FCSTD DOCUMENT  (FreeCAD 0.18R4 (GitTag))
Label: clinica_nuevo_monterreyp1
License: All rights reserved
LicenseURL: http://en.wikipedia.org/wiki/All_rights_reserved
objects: Part::Part2DObjectPython×355, App::Part×206, App::FeaturePython×159, App::DocumentObjectGroup×10, Part::FeaturePython×4
note: 359 computed .brp shape members not serialized (recipe doc carries the construction recipe); baked Part::Feature solids carry a one-line shape summary decoded from their .brp

FEATURE [Part::Part2DObjectPython] Line164  # Draft 2D object (typed FeaturePython)
  ChamferSize = 0
  Closed = false
  End = (0,-100,0)
  FilletRadius = 0
  Length = 200
  MakeFace = true
  Placement = pos=(0,100,0) rot=(0,0,1;0rad)
  Points = (2) [(0,0,0),(0,-200,0)]
  Start = (0,100,0)
  Subdivisions = 0
FEATURE [Part::Part2DObjectPython] Line157  # Draft 2D object (typed FeaturePython)
  ChamferSize = 0
  Closed = false
  End = (-100,3.8e-15,0)
  FilletRadius = 0
  Length = 200
  MakeFace = true
  Placement = pos=(100,1.8e-14,0) rot=(0,0,1;0rad)
  Points = (2) [(0,0,0),(-200,-1.42109e-14,0)]
  Start = (100,1.8e-14,0)
  Subdivisions = 0
FEATURE [Part::Part2DObjectPython] Line156  # Draft 2D object (typed FeaturePython)
  ChamferSize = 0
  Closed = false
  End = (0,-100,0)
  FilletRadius = 0
  Length = 200
  MakeFace = true
  Placement = pos=(0,100,0) rot=(0,0,1;0rad)
  Points = (2) [(0,0,0),(0,-200,0)]
  Start = (0,100,0)
  Subdivisions = 0
FEATURE [Part::Part2DObjectPython] Line166  # Draft 2D object (typed FeaturePython)
  ChamferSize = 0
  Closed = false
  End = (0,-100,0)
  FilletRadius = 0
  Length = 200
  MakeFace = true
  Placement = pos=(0,100,0) rot=(0,0,1;0rad)
  Points = (2) [(0,0,0),(0,-200,0)]
  Start = (0,100,0)
  Subdivisions = 0
FEATURE [Part::Part2DObjectPython] Line161  # Draft 2D object (typed FeaturePython)
  ChamferSize = 0
  Closed = false
  End = (-100,3.8e-15,0)
  FilletRadius = 0
  Length = 200
  MakeFace = true
  Placement = pos=(100,1.8e-14,0) rot=(0,0,1;0rad)
  Points = (2) [(0,0,0),(-200,-1.42109e-14,0)]
  Start = (100,1.8e-14,0)
  Subdivisions = 0
FEATURE [Part::Part2DObjectPython] Circle083  # Draft 2D object (typed FeaturePython)
  FirstAngle = 0
  LastAngle = 0
  MakeFace = true
  Radius = 100
FEATURE [Part::Part2DObjectPython] Line173  # Draft 2D object (typed FeaturePython)
  ChamferSize = 0
  Closed = false
  End = (-100,3.8e-15,0)
  FilletRadius = 0
  Length = 200
  MakeFace = true
  Placement = pos=(100,1.8e-14,0) rot=(0,0,1;0rad)
  Points = (2) [(0,0,0),(-200,-1.42109e-14,0)]
  Start = (100,1.8e-14,0)
  Subdivisions = 0
FEATURE [Part::Part2DObjectPython] Line152  # Draft 2D object (typed FeaturePython)
  ChamferSize = 0
  Closed = false
  End = (0,-100,0)
  FilletRadius = 0
  Length = 200
  MakeFace = true
  Placement = pos=(0,100,0) rot=(0,0,1;0rad)
  Points = (2) [(0,0,0),(0,-200,0)]
  Start = (0,100,0)
  Subdivisions = 0
FEATURE [Part::Part2DObjectPython] Line165  # Draft 2D object (typed FeaturePython)
  ChamferSize = 0
  Closed = false
  End = (-100,3.8e-15,0)
  FilletRadius = 0
  Length = 200
  MakeFace = true
  Placement = pos=(100,1.8e-14,0) rot=(0,0,1;0rad)
  Points = (2) [(0,0,0),(-200,-1.42109e-14,0)]
  Start = (100,1.8e-14,0)
  Subdivisions = 0
FEATURE [Part::Part2DObjectPython] Line170  # Draft 2D object (typed FeaturePython)
  ChamferSize = 0
  Closed = false
  End = (0,-100,0)
  FilletRadius = 0
  Length = 200
  MakeFace = true
  Placement = pos=(0,100,0) rot=(0,0,1;0rad)
  Points = (2) [(0,0,0),(0,-200,0)]
  Start = (0,100,0)
  Subdivisions = 0
FEATURE [Part::Part2DObjectPython] Line158  # Draft 2D object (typed FeaturePython)
  ChamferSize = 0
  Closed = false
  End = (0,-100,0)
  FilletRadius = 0
  Length = 200
  MakeFace = true
  Placement = pos=(0,100,0) rot=(0,0,1;0rad)
  Points = (2) [(0,0,0),(0,-200,0)]
  Start = (0,100,0)
  Subdivisions = 0
FEATURE [Part::Part2DObjectPython] Line155  # Draft 2D object (typed FeaturePython)
  ChamferSize = 0
  Closed = false
  End = (-100,3.8e-15,0)
  FilletRadius = 0
  Length = 200
  MakeFace = true
  Placement = pos=(100,1.8e-14,0) rot=(0,0,1;0rad)
  Points = (2) [(0,0,0),(-200,-1.42109e-14,0)]
  Start = (100,1.8e-14,0)
  Subdivisions = 0
FEATURE [Part::Part2DObjectPython] Circle077  # Draft 2D object (typed FeaturePython)
  FirstAngle = 0
  LastAngle = 0
  MakeFace = true
  Radius = 100
FEATURE [Part::Part2DObjectPython] Line168  # Draft 2D object (typed FeaturePython)
  ChamferSize = 0
  Closed = false
  End = (0,-100,0)
  FilletRadius = 0
  Length = 200
  MakeFace = true
  Placement = pos=(0,100,0) rot=(0,0,1;0rad)
  Points = (2) [(0,0,0),(0,-200,0)]
  Start = (0,100,0)
  Subdivisions = 0
FEATURE [Part::Part2DObjectPython] Circle081  # Draft 2D object (typed FeaturePython)
  FirstAngle = 0
  LastAngle = 0
  MakeFace = true
  Radius = 100
FEATURE [Part::Part2DObjectPython] Line153  # Draft 2D object (typed FeaturePython)
  ChamferSize = 0
  Closed = false
  End = (-100,3.8e-15,0)
  FilletRadius = 0
  Length = 200
  MakeFace = true
  Placement = pos=(100,1.8e-14,0) rot=(0,0,1;0rad)
  Points = (2) [(0,0,0),(-200,-1.42109e-14,0)]
  Start = (100,1.8e-14,0)
  Subdivisions = 0
FEATURE [Part::Part2DObjectPython] Line135  # Draft 2D object (typed FeaturePython)
  ChamferSize = 0
  Closed = false
  End = (-100,3.8e-15,0)
  FilletRadius = 0
  Length = 200
  MakeFace = true
  Placement = pos=(100,1.8e-14,0) rot=(0,0,1;0rad)
  Points = (2) [(0,0,0),(-200,-1.42109e-14,0)]
  Start = (100,1.8e-14,0)
  Subdivisions = 0
FEATURE [Part::Part2DObjectPython] Circle063  # Draft 2D object (typed FeaturePython)
  FirstAngle = 0
  LastAngle = 0
  MakeFace = false
  Radius = 50
FEATURE [Part::Part2DObjectPython] Line074  # Draft 2D object (typed FeaturePython)
  ChamferSize = 0
  Closed = false
  End = (100,100,0)
  FilletRadius = 0
  Length = 91.7357
  MakeFace = false
  Placement = pos=(35.1355,35.1306,0) rot=(0,0,1;0rad)
  Points = (2) [(0,0,0),(64.8645,64.8694,0)]
  Start = (35.1355,35.1306,0)
  Subdivisions = 0
FEATURE [Part::Part2DObjectPython] Line137  # Draft 2D object (typed FeaturePython)
  ChamferSize = 0
  Closed = false
  End = (-100,3.8e-15,0)
  FilletRadius = 0
  Length = 200
  MakeFace = true
  Placement = pos=(100,1.8e-14,0) rot=(0,0,1;0rad)
  Points = (2) [(0,0,0),(-200,-1.42109e-14,0)]
  Start = (100,1.8e-14,0)
  Subdivisions = 0
FEATURE [Part::Part2DObjectPython] Line133  # Draft 2D object (typed FeaturePython)
  ChamferSize = 0
  Closed = false
  End = (-100,3.8e-15,0)
  FilletRadius = 0
  Length = 200
  MakeFace = true
  Placement = pos=(100,1.8e-14,0) rot=(0,0,1;0rad)
  Points = (2) [(0,0,0),(-200,-1.42109e-14,0)]
  Start = (100,1.8e-14,0)
  Subdivisions = 0
FEATURE [Part::Part2DObjectPython] Circle064  # Draft 2D object (typed FeaturePython)
  FirstAngle = 0
  LastAngle = 0
  MakeFace = false
  Radius = 50
FEATURE [Part::Part2DObjectPython] Line130  # Draft 2D object (typed FeaturePython)
  ChamferSize = 0
  Closed = false
  End = (100,100,0)
  FilletRadius = 0
  Length = 91.7357
  MakeFace = false
  Placement = pos=(35.1355,35.1306,0) rot=(0,0,1;0rad)
  Points = (2) [(0,0,0),(64.8645,64.8694,0)]
  Start = (35.1355,35.1306,0)
  Subdivisions = 0
FEATURE [Part::Part2DObjectPython] Line134  # Draft 2D object (typed FeaturePython)
  ChamferSize = 0
  Closed = false
  End = (0,-100,0)
  FilletRadius = 0
  Length = 200
  MakeFace = true
  Placement = pos=(0,100,0) rot=(0,0,1;0rad)
  Points = (2) [(0,0,0),(0,-200,0)]
  Start = (0,100,0)
  Subdivisions = 0
FEATURE [Part::Part2DObjectPython] Line131  # Draft 2D object (typed FeaturePython)
  ChamferSize = 0
  Closed = false
  End = (100,100,0)
  FilletRadius = 0
  Length = 91.7357
  MakeFace = false
  Placement = pos=(35.1355,35.1306,0) rot=(0,0,1;0rad)
  Points = (2) [(0,0,0),(64.8645,64.8694,0)]
  Start = (35.1355,35.1306,0)
  Subdivisions = 0
FEATURE [Part::Part2DObjectPython] Circle066  # Draft 2D object (typed FeaturePython)
  FirstAngle = 0
  LastAngle = 0
  MakeFace = true
  Radius = 100
FEATURE [Part::Part2DObjectPython] Line075  # Draft 2D object (typed FeaturePython)
  ChamferSize = 0
  Closed = false
  End = (100,100,0)
  FilletRadius = 0
  Length = 91.7357
  MakeFace = false
  Placement = pos=(35.1355,35.1306,0) rot=(0,0,1;0rad)
  Points = (2) [(0,0,0),(64.8645,64.8694,0)]
  Start = (35.1355,35.1306,0)
  Subdivisions = 0
FEATURE [Part::Part2DObjectPython] Line139  # Draft 2D object (typed FeaturePython)
  ChamferSize = 0
  Closed = false
  End = (-100,3.8e-15,0)
  FilletRadius = 0
  Length = 200
  MakeFace = true
  Placement = pos=(100,1.8e-14,0) rot=(0,0,1;0rad)
  Points = (2) [(0,0,0),(-200,-1.42109e-14,0)]
  Start = (100,1.8e-14,0)
  Subdivisions = 0
FEATURE [Part::Part2DObjectPython] Line149  # Draft 2D object (typed FeaturePython)
  ChamferSize = 0
  Closed = false
  End = (-100,3.8e-15,0)
  FilletRadius = 0
  Length = 200
  MakeFace = true
  Placement = pos=(100,1.8e-14,0) rot=(0,0,1;0rad)
  Points = (2) [(0,0,0),(-200,-1.42109e-14,0)]
  Start = (100,1.8e-14,0)
  Subdivisions = 0
FEATURE [Part::Part2DObjectPython] Line138  # Draft 2D object (typed FeaturePython)
  ChamferSize = 0
  Closed = false
  End = (0,-100,0)
  FilletRadius = 0
  Length = 200
  MakeFace = true
  Placement = pos=(0,100,0) rot=(0,0,1;0rad)
  Points = (2) [(0,0,0),(0,-200,0)]
  Start = (0,100,0)
  Subdivisions = 0
FEATURE [Part::Part2DObjectPython] Line136  # Draft 2D object (typed FeaturePython)
  ChamferSize = 0
  Closed = false
  End = (0,-100,0)
  FilletRadius = 0
  Length = 200
  MakeFace = true
  Placement = pos=(0,100,0) rot=(0,0,1;0rad)
  Points = (2) [(0,0,0),(0,-200,0)]
  Start = (0,100,0)
  Subdivisions = 0
FEATURE [Part::Part2DObjectPython] Line132  # Draft 2D object (typed FeaturePython)
  ChamferSize = 0
  Closed = false
  End = (0,-100,0)
  FilletRadius = 0
  Length = 200
  MakeFace = true
  Placement = pos=(0,100,0) rot=(0,0,1;0rad)
  Points = (2) [(0,0,0),(0,-200,0)]
  Start = (0,100,0)
  Subdivisions = 0
FEATURE [App::Part] Part095  label="contenido004"
  Group = -> [Circle066,Line132,Line133]
  Origin = -> Origin095
FEATURE [Part::Part2DObjectPython] Circle069  # Draft 2D object (typed FeaturePython)
  FirstAngle = 0
  LastAngle = 0
  MakeFace = true
  Radius = 100
FEATURE [Part::Part2DObjectPython] Circle062  # Draft 2D object (typed FeaturePython)
  FirstAngle = 0
  LastAngle = 0
  MakeFace = false
  Radius = 50
FEATURE [App::Part] Part180  label="contenido048"
  Group = -> [Line074,Circle062]
  Origin = -> Origin179
FEATURE [App::Part] Part189  label="contenido053"
  Group = -> [Circle069,Line138,Line139]
  Origin = -> Origin190
FEATURE [Part::Part2DObjectPython] Circle070  # Draft 2D object (typed FeaturePython)
  FirstAngle = 0
  LastAngle = 0
  MakeFace = true
  Radius = 100
FEATURE [Part::Part2DObjectPython] Line146  # Draft 2D object (typed FeaturePython)
  ChamferSize = 0
  Closed = false
  End = (0,-100,0)
  FilletRadius = 0
  Length = 200
  MakeFace = true
  Placement = pos=(0,100,0) rot=(0,0,1;0rad)
  Points = (2) [(0,0,0),(0,-200,0)]
  Start = (0,100,0)
  Subdivisions = 0
FEATURE [Part::Part2DObjectPython] Circle065  # Draft 2D object (typed FeaturePython)
  FirstAngle = 0
  LastAngle = 0
  MakeFace = false
  Radius = 50
FEATURE [Part::Part2DObjectPython] Rectangle050  label="luz_60x60_cuerpo001"  # Draft 2D object (typed FeaturePython)
  ChamferSize = 0
  Columns = 1
  FilletRadius = 0
  Height = 600
  Length = 600
  MakeFace = true
  Rows = 1
FEATURE [Part::Part2DObjectPython] Circle068  # Draft 2D object (typed FeaturePython)
  FirstAngle = 0
  LastAngle = 0
  MakeFace = true
  Radius = 100
FEATURE [App::Part] Part187  label="contenido052"
  Group = -> [Circle068,Line136,Line137]
  Origin = -> Origin188
FEATURE [App::Part] Part182  label="contenido049"
  Group = -> [Line075,Circle063]
  Origin = -> Origin181
FEATURE [Part::Part2DObjectPython] Circle067  # Draft 2D object (typed FeaturePython)
  FirstAngle = 0
  LastAngle = 0
  MakeFace = true
  Radius = 100
FEATURE [App::Part] Part185  label="contenido051"
  Group = -> [Circle067,Line134,Line135]
  Origin = -> Origin186
FEATURE [Part::Part2DObjectPython] Rectangle051  label="luz_60x60_cuerpo002"  # Draft 2D object (typed FeaturePython)
  ChamferSize = 0
  Columns = 1
  FilletRadius = 0
  Height = 600
  Length = 600
  MakeFace = true
  Rows = 1
FEATURE [App::Part] Part193  label="contenido054"
  Group = -> [Rectangle051]
  Origin = -> Origin193
FEATURE [App::Part] Part184  label="contenido050"
  Group = -> [Line131,Circle065]
  Origin = -> Origin183
FEATURE [Part::Part2DObjectPython] Circle072  # Draft 2D object (typed FeaturePython)
  FirstAngle = 0
  LastAngle = 0
  MakeFace = true
  Radius = 100
FEATURE [Part::Part2DObjectPython] Circle073  # Draft 2D object (typed FeaturePython)
  FirstAngle = 0
  LastAngle = 0
  MakeFace = true
  Radius = 100
FEATURE [Part::Part2DObjectPython] ShapeString068  label="rotulo_dibujo_tecnico__068"  # Draft 2D object (typed FeaturePython)
  FontFile = <path>
  Placement = pos=(0,100,0) rot=(0,0,1;0rad)
  Size = 50
  String = 5
  Tracking = 0
FEATURE [Part::Part2DObjectPython] ShapeString070  label="rotulo_dibujo_tecnico__070"  # Draft 2D object (typed FeaturePython)
  FontFile = <path>
  Placement = pos=(0,100,0) rot=(0,0,1;0rad)
  Size = 50
  String = 10
  Tracking = 0
FEATURE [Part::Part2DObjectPython] ShapeString028  label="rotulo_dibujo_tecnico__028"  # Draft 2D object (typed FeaturePython)
  FontFile = <path>
  Placement = pos=(0,100,0) rot=(0,0,1;0rad)
  Size = 50
  String = 35
  Tracking = 0
FEATURE [Part::Part2DObjectPython] ShapeString065  label="rotulo_dibujo_tecnico__065"  # Draft 2D object (typed FeaturePython)
  FontFile = <path>
  Placement = pos=(0,100,0) rot=(0,0,1;0rad)
  Size = 50
  String = 15
  Tracking = 0
FEATURE [Part::Part2DObjectPython] ShapeString007  label="rotulo_dibujo_tecnico__007"  # Draft 2D object (typed FeaturePython)
  FontFile = <path>
  Placement = pos=(0,150,0) rot=(0,0,1;3.14159rad)
  Size = 50
  String = 10
  Tracking = 0
FEATURE [Part::Part2DObjectPython] Line141  # Draft 2D object (typed FeaturePython)
  ChamferSize = 0
  Closed = false
  End = (-100,3.8e-15,0)
  FilletRadius = 0
  Length = 200
  MakeFace = true
  Placement = pos=(100,1.8e-14,0) rot=(0,0,1;0rad)
  Points = (2) [(0,0,0),(-200,-1.42109e-14,0)]
  Start = (100,1.8e-14,0)
  Subdivisions = 0
FEATURE [Part::Part2DObjectPython] Line145  # Draft 2D object (typed FeaturePython)
  ChamferSize = 0
  Closed = false
  End = (-100,3.8e-15,0)
  FilletRadius = 0
  Length = 200
  MakeFace = true
  Placement = pos=(100,1.8e-14,0) rot=(0,0,1;0rad)
  Points = (2) [(0,0,0),(-200,-1.42109e-14,0)]
  Start = (100,1.8e-14,0)
  Subdivisions = 0
FEATURE [Part::Part2DObjectPython] Rectangle052  label="luz_60x60_cuerpo003"  # Draft 2D object (typed FeaturePython)
  ChamferSize = 0
  Columns = 1
  FilletRadius = 0
  Height = 600
  Length = 600
  MakeFace = true
  Rows = 1
FEATURE [App::Part] Part195  label="contenido055"
  Group = -> [Rectangle052]
  Origin = -> Origin195
FEATURE [Part::Part2DObjectPython] ShapeString018  label="rotulo_dibujo_tecnico__018"  # Draft 2D object (typed FeaturePython)
  FontFile = <path>
  Placement = pos=(0,100,0) rot=(0,0,1;0rad)
  Size = 50
  String = 20
  Tracking = 0
FEATURE [Part::Part2DObjectPython] ShapeString014  label="rotulo_dibujo_tecnico__014"  # Draft 2D object (typed FeaturePython)
  FontFile = <path>
  Placement = pos=(0,100,0) rot=(0,0,1;0rad)
  Size = 50
  String = -
  Tracking = 0
FEATURE [Part::Part2DObjectPython] Line163  # Draft 2D object (typed FeaturePython)
  ChamferSize = 0
  Closed = false
  End = (-100,3.8e-15,0)
  FilletRadius = 0
  Length = 200
  MakeFace = true
  Placement = pos=(100,1.8e-14,0) rot=(0,0,1;0rad)
  Points = (2) [(0,0,0),(-200,-1.42109e-14,0)]
  Start = (100,1.8e-14,0)
  Subdivisions = 0
FEATURE [Part::Part2DObjectPython] Circle080  # Draft 2D object (typed FeaturePython)
  FirstAngle = 0
  LastAngle = 0
  MakeFace = true
  Radius = 100
FEATURE [Part::Part2DObjectPython] Circle086  # Draft 2D object (typed FeaturePython)
  FirstAngle = 0
  LastAngle = 0
  MakeFace = true
  Radius = 100
FEATURE [Part::Part2DObjectPython] Circle082  # Draft 2D object (typed FeaturePython)
  FirstAngle = 0
  LastAngle = 0
  MakeFace = true
  Radius = 100
FEATURE [Part::Part2DObjectPython] ShapeString040  label="rotulo_dibujo_tecnico__040"  # Draft 2D object (typed FeaturePython)
  FontFile = <path>
  Placement = pos=(0,100,0) rot=(0,0,1;0rad)
  Size = 50
  String = 33
  Tracking = 0
FEATURE [Part::Part2DObjectPython] Line183  # Draft 2D object (typed FeaturePython)
  ChamferSize = 0
  Closed = false
  End = (-100,3.8e-15,0)
  FilletRadius = 0
  Length = 200
  MakeFace = true
  Placement = pos=(100,1.8e-14,0) rot=(0,0,1;0rad)
  Points = (2) [(0,0,0),(-200,-1.42109e-14,0)]
  Start = (100,1.8e-14,0)
  Subdivisions = 0
FEATURE [App::FeaturePython] InternalObjectName087  label="smi_propiedades"  # WARN: FeaturePython — macro-defined, semantics opaque (R4)
  altura_desde_piso = 0
  corriente_max_int_a = 7
  estado = ok
  fuente = 0xf14623025ac55d36651701217b5500468671db5aece4180de1e397691b516df76385c49eda21b289d108adb05feff80badbb931b03b018717ff431ab7f54e52b
  id_fuente = 0x324bf51e3ef5d4e0f3fe3b1eeba68c0344bf68769c3a0983c5ffaed9b3cb489a302b4d803ea4e73a8b5257f138b90adbb94e8408ade3e9cefe988441e3d20777
  id_pieza_electronica = 0x2bdee77ba7d76b92ce56d5254b00cfa898381ee476245d19efe06ec407f09a4fa0eb1ba56ac66c04c3f8d748c79be5bb09f0ed32f9261e3d76be9c109a6f5ad5
  nombre_propiedad_exportable = sensor_movimiento_interruptor_propiedades
  tipo_interruptor = Ordinario sencillo
  voltaje_max_ctrl_v = 130
  voltaje_max_int_v = 130
  voltaje_min_ctrl_v = 110
  voltaje_nominal_ctrl_v = 120
FEATURE [App::FeaturePython] InternalObjectName094  label="cbk_propiedades003"  # WARN: FeaturePython — macro-defined, semantics opaque (R4)
  corriente_max_a = 30
  id_fuente = 0xd8f18255180944202b46e0746b77681301b8ee1827dde12bb09dfc227b8e2b7aa3e32cb36b35f2f5ea21653418a074966d5950270e013ac8b44cc1e51a4064aa
  id_pieza_electronica = 0x776b016cecfcf13c1d6d100137757931a6a1d289bd06493bb7e94b538f06d114879d181e063709bddc563f3a421251663f8630c61a62ee22fd9a7ad951ec3dc0
  nombre_propiedad_exportable = disyuntor_propiedades
  num_circuito = B5
  num_tablero_distribucion = 1
  voltaje_max_v = 600
FEATURE [App::FeaturePython] InternalObjectName077  label="luz_8in_props026"  # WARN: FeaturePython — macro-defined, semantics opaque (R4)
  altura_desde_piso = 0
  fuente = 0x77c2f575a9e1860d16eeb77845606b36640c42c814c25ce4582d16db626eb3350dcd1ca6545a4fa9685324c00d2a5d50b3f390506bd7b1112e1a4a206ffe652e
  id_pieza_electronica = 0x21a78dc71108e1883de38b3c6660c0ce4df41a076f2fb97842f82d433e1c8b45aed11dec3fc12d9003cf3404e1ede2f23b5ded1c06c04d94d7887c89e7cd6286
  nombre_propiedad_exportable = luz_propiedades
  potencia_w = 18
  rotulo_dibujo_tecnico = 1
  tipo_luz = Led
  voltaje_max_v = 130
  voltaje_min_v = 95
  voltaje_nominal_v = 110
FEATURE [App::FeaturePython] InternalObjectName019  label="tc_props017"  # WARN: FeaturePython — macro-defined, semantics opaque (R4)
  altura_desde_piso = 1460
  cantidad_puertos = 2
  corriente_max_a = 15
  estado = L, N, G.
  id_fuente = 0xfccb5268be57a3458fe0dacdcb08adef477e64af0ea2a134f7ad34c230bdb54ee052b17ffb07b6f537157d03287af2a27a7c8566c7efd6afa40829e98de8394e
  id_pieza_electronica = 0x896640573fd1b1a4cff97813da3840b8aacd126b0e11d8834f163ccd2acb5a636f8a368cd82d8640d7f44ab5f7e1f1314108d88f894faeb934a75b57b339fe22
  nombre_propiedad_exportable = tomacorriente_propiedades
  num_circuito = A4
  num_tablero_distribucion = 1
  observaciones = Debe ser GFCI.
  rotulo_dibujo_tecnico = 1
  tipo = NEMA 5-15R
  voltaje_max_v = 125
FEATURE [App::FeaturePython] InternalObjectName086  label="cbk_propiedades"  # WARN: FeaturePython — macro-defined, semantics opaque (R4)
  corriente_max_a = 30
  estado = ok
  id_fuente = 0xf14623025ac55d36651701217b5500468671db5aece4180de1e397691b516df76385c49eda21b289d108adb05feff80badbb931b03b018717ff431ab7f54e52b
  id_pieza_electronica = 0x8d4e96eb3a850b9e14bd50efe1ec9cb199d73561933df684fabdf9f62e93ebe301d165a7338d921d131adbbbb1abbb93918a4f032ee787971f13e095ed5221ab
  nombre_propiedad_exportable = disyuntor_propiedades
  num_circuito = B6
  num_tablero_distribucion = 1
  voltaje_max_v = 240
FEATURE [App::FeaturePython] InternalObjectName079  label="luz_8in_props028"  # WARN: FeaturePython — macro-defined, semantics opaque (R4)
  altura_desde_piso = 0
  fuente = 0x4691e5377baf05716203601fc41c00b6afecc1767ec40715de46e7d1d07508fc757dcb58bfd3060d788207d0709fcb2d94a4c594f1d8f44bc2891cf2806e2f10
  id_pieza_electronica = 0x287a68b6af31000f0cabc12a1509fec047bfe37ed8001fadd896d4169b2a171901036650087eb6be7f07f13ec818a69402b0f099375cbb20947a043f7c533692
  nombre_propiedad_exportable = luz_propiedades
  potencia_w = 18
  rotulo_dibujo_tecnico = 2
  tipo_luz = Led
  voltaje_max_v = 130
  voltaje_min_v = 95
  voltaje_nominal_v = 110
FEATURE [App::FeaturePython] InternalObjectName075  label="luz_8in_props024"  # WARN: FeaturePython — macro-defined, semantics opaque (R4)
  altura_desde_piso = 0
  fuente = 0x77c2f575a9e1860d16eeb77845606b36640c42c814c25ce4582d16db626eb3350dcd1ca6545a4fa9685324c00d2a5d50b3f390506bd7b1112e1a4a206ffe652e
  id_pieza_electronica = 0x49f479e12199b4cee3d2b5b5994cacc775549c0e1d225f65596251ba84bd43da0973c88059b5adad9f14404f2a50d42df9def80444c8898f4990c394ade2cd77
  nombre_propiedad_exportable = luz_propiedades
  potencia_w = 18
  rotulo_dibujo_tecnico = 3
  tipo_luz = Led
  voltaje_max_v = 130
  voltaje_min_v = 95
  voltaje_nominal_v = 110
FEATURE [App::FeaturePython] InternalObjectName091  label="cbk_propiedades001"  # WARN: FeaturePython — macro-defined, semantics opaque (R4)
  corriente_max_a = 20
  id_fuente = 0x315a1ca519087612d13fea687ed104ad9e82552b55f78e571223afa4046e4dad2bb5dcb2a475dd9031990531d1454d3ea2dd9a8c6f1f01dd58c93674f19f4e33
  id_pieza_electronica = 0x7a5b1c9c952b25825b5f0d2f75da007d3198afc15604896d64148ec2f645987a60f5976f117effc0c26b18ec179cf9f614b5850eb5c22f90f5bc95e22c7e72fd
  nombre_propiedad_exportable = disyuntor_propiedades
  num_circuito = B8
  num_tablero_distribucion = 1
  voltaje_max_v = 240
FEATURE [App::FeaturePython] InternalObjectName081  label="luz_8in_props030"  # WARN: FeaturePython — macro-defined, semantics opaque (R4)
  altura_desde_piso = 0
  fuente = 0x77c2f575a9e1860d16eeb77845606b36640c42c814c25ce4582d16db626eb3350dcd1ca6545a4fa9685324c00d2a5d50b3f390506bd7b1112e1a4a206ffe652e
  id_pieza_electronica = 0x7bc494f8ef4bef8b21ff157f1f1fe86e624351819009fc23e15904f12a88fd4a55aa0798ca35a2d8a19b50651605767044211e512db4fa317cb047113990f6f4
  nombre_propiedad_exportable = luz_propiedades
  potencia_w = 18
  rotulo_dibujo_tecnico = 4
  tipo_luz = Led
  voltaje_max_v = 130
  voltaje_min_v = 95
  voltaje_nominal_v = 110
FEATURE [App::FeaturePython] InternalObjectName084  label="luz_8in_props033"  # WARN: FeaturePython — macro-defined, semantics opaque (R4)
  altura_desde_piso = 0
  fuente = 0x4691e5377baf05716203601fc41c00b6afecc1767ec40715de46e7d1d07508fc757dcb58bfd3060d788207d0709fcb2d94a4c594f1d8f44bc2891cf2806e2f10
  id_pieza_electronica = 0x118195bce68d95d6d2d6a0d7a95d53ddfdfb6f579e9408626bdf0a5eaf6f86fb0c044407f73211d38c82946fe2dd471e834e1deb0a6f6a5890e490821058715d
  nombre_propiedad_exportable = luz_propiedades
  potencia_w = 18
  rotulo_dibujo_tecnico = 5
  tipo_luz = Led
  voltaje_max_v = 130
  voltaje_min_v = 95
  voltaje_nominal_v = 110
FEATURE [App::FeaturePython] InternalObjectName089  label="extractor_aire_props001"  # WARN: FeaturePython — macro-defined, semantics opaque (R4)
  altura_desde_piso = 0
  id_pieza_electronica = 0x7912be09939a93fcd0adc71f553116b3080f3171aa5dbc748c1be12adb20d2976378cb8b80bcbe50f22ec9bd34862c2a72775d0aa8188ead3dfc40bcfe2dc3a5
  nombre_propiedad_exportable = extractor_aire_propiedades
  potencia_w = 60
  rotulo_dibujo_tecnico = 1
  tipo = Extractor de aire
  voltaje_max_v = 130
  voltaje_min_v = 95
  voltaje_nominal_v = 110
FEATURE [App::FeaturePython] InternalObjectName069  label="luz_8in_props018"  # WARN: FeaturePython — macro-defined, semantics opaque (R4)
  altura_desde_piso = 0
  fuente = 0xe278294e5fd594ca5bf1db021ee32b4f9714d6e66f847416ed29239ba0d5edb499c2a05fb43f4d3d2588dbcc4f87afd6fc02970743af0882acb5c9efd440cf89
  id_pieza_electronica = 0x745c9f994b37b0ed2eb92dc77283523a244d45a178a204e68c429a7ce06f4730fe279fbcc370936ff0f79e35598570529114bc797e1d8d73664249e73107d404
  nombre_propiedad_exportable = luz_propiedades
  potencia_w = 18
  rotulo_dibujo_tecnico = 6
  tipo_luz = Led
  voltaje_max_v = 130
  voltaje_min_v = 95
  voltaje_nominal_v = 110
FEATURE [App::FeaturePython] InternalObjectName080  label="luz_8in_props029"  # WARN: FeaturePython — macro-defined, semantics opaque (R4)
  altura_desde_piso = 0
  fuente = 0x4691e5377baf05716203601fc41c00b6afecc1767ec40715de46e7d1d07508fc757dcb58bfd3060d788207d0709fcb2d94a4c594f1d8f44bc2891cf2806e2f10
  id_pieza_electronica = 0x786115346131de3bf2f695756c40451e3b903d38da54eb249269855a43d66ef62a31289e2d35645762afb0fd45906eba0b380407ca0b438e71c33c91e0a7b621
  nombre_propiedad_exportable = luz_propiedades
  potencia_w = 18
  rotulo_dibujo_tecnico = 7
  tipo_luz = Led
  voltaje_max_v = 130
  voltaje_min_v = 95
  voltaje_nominal_v = 110
FEATURE [App::FeaturePython] InternalObjectName078  label="luz_8in_props027"  # WARN: FeaturePython — macro-defined, semantics opaque (R4)
  altura_desde_piso = 0
  fuente = 0xedfc5bb3aa30eb8bd0709db342119f4dde92e71105b250b3161ed4f19e3a93e66b6ad4c2c072d329844ca216b74895e70a9c625ca2b1a1a934e3f21c3a35e75b
  id_pieza_electronica = 0x2e10ab01b01568ec5cb4e7728bf3dd48955f867596b5eaabfc04348dada0a0fff4ce592f79b6c3e4ec1c4399721d3a9a1161ebd5c8217b2e5cc315f49f3f117d
  nombre_propiedad_exportable = luz_propiedades
  potencia_w = 18
  rotulo_dibujo_tecnico = 8
  tipo_luz = Led
  voltaje_max_v = 130
  voltaje_min_v = 95
  voltaje_nominal_v = 110
FEATURE [App::FeaturePython] InternalObjectName067  label="luz_8in_props016"  # WARN: FeaturePython — macro-defined, semantics opaque (R4)
  altura_desde_piso = 0
  fuente = 0x324bf51e3ef5d4e0f3fe3b1eeba68c0344bf68769c3a0983c5ffaed9b3cb489a302b4d803ea4e73a8b5257f138b90adbb94e8408ade3e9cefe988441e3d20777
  id_pieza_electronica = 0x5bec87812850074afd535c1d395f8999888d0a6512ee2311e19896391ecaa9dc89b51334839adb8231889e5b0858f7fa123e6725f984af79506e3d2c13c219ba
  nombre_propiedad_exportable = luz_propiedades
  potencia_w = 18
  rotulo_dibujo_tecnico = 9
  tipo_luz = Led
  voltaje_max_v = 130
  voltaje_min_v = 95
  voltaje_nominal_v = 110
FEATURE [App::FeaturePython] InternalObjectName074  label="luz_8in_props023"  # WARN: FeaturePython — macro-defined, semantics opaque (R4)
  altura_desde_piso = 0
  fuente = 0xedfc5bb3aa30eb8bd0709db342119f4dde92e71105b250b3161ed4f19e3a93e66b6ad4c2c072d329844ca216b74895e70a9c625ca2b1a1a934e3f21c3a35e75b
  id_pieza_electronica = 0x6b8c940b3c3d0ea73f77986623b2d1adc875618d197224665e553ab96d6a7c997def007ef6ca7471bd7426a188029043793e1bb3b4325d0d128bbe229e6d943d
  nombre_propiedad_exportable = luz_propiedades
  potencia_w = 18
  rotulo_dibujo_tecnico = 10
  tipo_luz = Led
  voltaje_max_v = 130
  voltaje_min_v = 95
  voltaje_nominal_v = 110
FEATURE [App::FeaturePython] InternalObjectName073  label="luz_8in_props022"  # WARN: FeaturePython — macro-defined, semantics opaque (R4)
  altura_desde_piso = 0
  fuente = 0x4691e5377baf05716203601fc41c00b6afecc1767ec40715de46e7d1d07508fc757dcb58bfd3060d788207d0709fcb2d94a4c594f1d8f44bc2891cf2806e2f10
  id_pieza_electronica = 0x749c5c3d34be6d944cfa6f98e263edf4b0f508022a8e361af4f9fdee0290246b2ac584a3f0b9b7c686008aeb3f55ff87737d5baad44bef9e1bcf6c7dfdf28ab1
  nombre_propiedad_exportable = luz_propiedades
  potencia_w = 18
  rotulo_dibujo_tecnico = 11
  tipo_luz = Led
  voltaje_max_v = 130
  voltaje_min_v = 95
  voltaje_nominal_v = 110
FEATURE [App::FeaturePython] InternalObjectName016  label="tc_props014"  # WARN: FeaturePython — macro-defined, semantics opaque (R4)
  altura_desde_piso = 610
  cantidad_puertos = 2
  corriente_max_a = 15
  estado = L, N, G.
  id_fuente = 0x4d33412d6822039de5d946b8e8b4c7d83a32e714f77763e145b40d8f592fc91dcf4427a02de90ac493abeaf956e60ab64302d564398f85eb0db037eef44968cf
  id_pieza_electronica = 0x84cdce75dd914e4356f47bfcc1d4834616b10f37b71a4b02da52a3c03d590bf123dd1b94f256abd95148be140796bc64f996a26565544f6f8d77b6d29d57b35e
  nombre_propiedad_exportable = tomacorriente_propiedades
  num_circuito = B6
  num_tablero_distribucion = 1
  rotulo_dibujo_tecnico = 2
  tipo = NEMA 5-15R
  voltaje_max_v = 125
FEATURE [App::FeaturePython] InternalObjectName083  label="luz_8in_props032"  # WARN: FeaturePython — macro-defined, semantics opaque (R4)
  altura_desde_piso = 0
  fuente = 0xedfc5bb3aa30eb8bd0709db342119f4dde92e71105b250b3161ed4f19e3a93e66b6ad4c2c072d329844ca216b74895e70a9c625ca2b1a1a934e3f21c3a35e75b
  id_pieza_electronica = 0x7073da146feec7d9f17735a9269ed8244c988779a5ee85df9f0d1d1f8bef79c8416aa9d004cee1f98a305085f9f38df06babc34dcaa567ec99b7066d4826ae77
  nombre_propiedad_exportable = luz_propiedades
  potencia_w = 18
  rotulo_dibujo_tecnico = 12
  tipo_luz = Led
  voltaje_max_v = 130
  voltaje_min_v = 95
  voltaje_nominal_v = 110
FEATURE [App::FeaturePython] Text005  # WARN: FeaturePython — macro-defined, semantics opaque (R4)
  Placement = pos=(-12.7272,-15.1048,0) rot=(0,0,1;0rad)
  Text = F
FEATURE [App::FeaturePython] InternalObjectName085  label="luz_8in_props034"  # WARN: FeaturePython — macro-defined, semantics opaque (R4)
  altura_desde_piso = 0
  fuente = 0x4691e5377baf05716203601fc41c00b6afecc1767ec40715de46e7d1d07508fc757dcb58bfd3060d788207d0709fcb2d94a4c594f1d8f44bc2891cf2806e2f10
  id_pieza_electronica = 0x9fb950b3e0bdda4b855aff4f5a00b0b208447d6ac72d6351a1162bb74e40297ba27bcdef01598b7d191dc74c1d6cf8051f8cc44dad81fe7f05f2fd4b3212e58c
  nombre_propiedad_exportable = luz_propiedades
  potencia_w = 18
  rotulo_dibujo_tecnico = 13
  tipo_luz = Led
  voltaje_max_v = 130
  voltaje_min_v = 95
  voltaje_nominal_v = 110
FEATURE [App::FeaturePython] InternalObjectName093  label="cbk3_propiedades"  # WARN: FeaturePython — macro-defined, semantics opaque (R4)
  corriente_max_a = 60
  id_fuente_polo1 = 0x405b3148a8ff4f1b4ec136794db6c0f5b08c3fbbe3f8c8a9e2fba99b06f9e3a6ab165f2cda5d1f05aae373ca95feb573e6ce4fef7b8a3c44642327fe3c198483
  id_fuente_polo2 = 0x1a72ca3048cbadf6e45b2c8ed2ce1c21e39e2f59b8e5711eb97f80a9695fdfa4eec7e7253c0d68ee683f47e71854345346d3d82afebb69b7a22fa319e1c3d7b5
  id_fuente_polo3 = 0xe8e6b78c5a938a970d4cc480ecec14b01a5876ac7c0eb775438375278826207f6c076f58d7d56d2f5648415434c900e795a7921d6b7136612fc837a2d6211b48
  id_pieza_electronica = 0xb76b353265e1667a6b78b2ddcd9180e99eaf5dc75c58403103de631f89d1da2ebcbe582a40d0cae18c4b6d7559c9928ac7af3cdaf981ccee05fc933ad75ddbc2
  nombre_propiedad_exportable = disyuntor3_propiedades
  num_circuito_polo1 = B1
  num_circuito_polo2 = B2
  num_circuito_polo3 = B3
  num_tablero_distribucion = 1
  voltaje_max_v = 240
FEATURE [App::FeaturePython] InternalObjectName088  label="extractor_aire_props"  # WARN: FeaturePython — macro-defined, semantics opaque (R4)
  altura_desde_piso = 0
  id_pieza_electronica = 0x12dadb5d0a557b034b7eba62c244979383a5ed27a10b8b0f9d76adafbee7375c2b9cd0e8c87e8b3f04f2d0d832b2c9c7fbf955bb82227614ae1c000485285949
  nombre_propiedad_exportable = extractor_aire_propiedades
  potencia_w = 60
  rotulo_dibujo_tecnico = 2
  tipo = Extractor de aire
  voltaje_max_v = 130
  voltaje_min_v = 95
  voltaje_nominal_v = 110
FEATURE [App::FeaturePython] InternalObjectName082  label="luz_8in_props031"  # WARN: FeaturePython — macro-defined, semantics opaque (R4)
  altura_desde_piso = 0
  fuente = 0x77c2f575a9e1860d16eeb77845606b36640c42c814c25ce4582d16db626eb3350dcd1ca6545a4fa9685324c00d2a5d50b3f390506bd7b1112e1a4a206ffe652e
  id_pieza_electronica = 0xd9420f45d67526f34a0f09fce3a20a30b01f62064df9196289eb154308eb49371ba9d18f1a7d39d1740cd21ba4c8663cff3c2e5c8ed27ef0b177559e466582a0
  nombre_propiedad_exportable = luz_propiedades
  potencia_w = 18
  rotulo_dibujo_tecnico = 14
  tipo_luz = Led
  voltaje_max_v = 130
  voltaje_min_v = 95
  voltaje_nominal_v = 110
FEATURE [App::FeaturePython] InternalObjectName092  label="cbk_propiedades002"  # WARN: FeaturePython — macro-defined, semantics opaque (R4)
  corriente_max_a = 30
  id_fuente = 0xd9845370d3c69e528b94f2727eb5cb90450e8d50bc3c7b3d1007b105133cddb3e45a481e72977f99cb649fe44c4de4b9b8ee976a16ec875e7ec12c7da3fbeb59
  id_pieza_electronica = 0x37379ab0baeb69e4bbdb22e0bbf0fda528a147077015dc4644cc3955c6b4042808c6b55fe638b3001b949a266e1fd7bcfdf388ca483d9554cba00d0d8b0cd6bf
  nombre_propiedad_exportable = disyuntor_propiedades
  num_circuito = B4
  num_tablero_distribucion = 1
  voltaje_max_v = 240
FEATURE [App::FeaturePython] Text009  # WARN: FeaturePython — macro-defined, semantics opaque (R4)
  Placement = pos=(-12.7272,-15.1048,0) rot=(0,0,1;0rad)
  Text = F
FEATURE [App::FeaturePython] InternalObjectName076  label="luz_8in_props025"  # WARN: FeaturePython — macro-defined, semantics opaque (R4)
  altura_desde_piso = 0
  fuente = 0x77c2f575a9e1860d16eeb77845606b36640c42c814c25ce4582d16db626eb3350dcd1ca6545a4fa9685324c00d2a5d50b3f390506bd7b1112e1a4a206ffe652e
  id_pieza_electronica = 0xa82b3d71f1c4efc3ea603037cf661b8f68e8c92d261b7d87eb686568395f9ed3491218f3a36ba7970544ce0cdb58a0cd19f4b1396137036a4410b10ab9647982
  nombre_propiedad_exportable = luz_propiedades
  potencia_w = 18
  rotulo_dibujo_tecnico = 15
  tipo_luz = Led
  voltaje_max_v = 130
  voltaje_min_v = 95
  voltaje_nominal_v = 110
FEATURE [App::FeaturePython] Dimension035  # Draft dimension (typed FeaturePython)
  Diameter = false
  Dimline = (5300,4500,0)
  Direction = (0,0,0)
  Distance = 1415
  End = (5600,5915,0)
  Normal = (0,0,1)
  Start = (5600,4500,0)
  expr: End.y = Rectangle017.Placement.Base.y
  expr: Start.y = Rectangle016.Placement.Base.y + Rectangle016.Height
FEATURE [App::FeaturePython] InternalObjectName014  label="tc_props012"  # WARN: FeaturePython — macro-defined, semantics opaque (R4)
  altura_desde_piso = 300
  cantidad_puertos = 2
  corriente_max_a = 15
  estado = L, N, sin G.
  id_fuente = 0x3dd4e762a20efd98b3a3b370291335c9b26ee223e5f353bcf6ba7c9603051cb564954890272eebb3a331b24acd0c4bd7740a40ad7a6ba66950ae1b45d0650307
  id_pieza_electronica = 0xe204d680c99eba862ad96ccfb7ee4e4d5296c8e8b7f494943a99e4503ad0a6098d97beedf0e628c6e384872144f13cf28d092e515cd7d0f839e976529e4666de
  nombre_propiedad_exportable = tomacorriente_propiedades
  num_circuito = A1
  num_tablero_distribucion = 1
  rotulo_dibujo_tecnico = 3
  tipo = NEMA 5-15R
  voltaje_max_v = 125
FEATURE [App::FeaturePython] InternalObjectName055  label="luz_6.5in_props"  # WARN: FeaturePython — macro-defined, semantics opaque (R4)
  altura_desde_piso = 0
  id_pieza_electronica = 0xfdc7dd70c12219df1677205de8737aeb7746eec182e965d01889e0d060edc7e4da24c067b6f24bf5051012388a0a22ce1d34e74d873a56d1be55e032f318b34e
  nombre_propiedad_exportable = luz_propiedades
  potencia_w = 18
  rotulo_dibujo_tecnico = 16
  tipo_luz = Led
  voltaje_max_v = 130
  voltaje_min_v = 95
  voltaje_nominal_v = 110
FEATURE [App::FeaturePython] Dimension023  # Draft dimension (typed FeaturePython)
  Diameter = false
  Dimline = (22203.5,4031.5,0)
  Direction = (0,0,0)
  Distance = 4907
  End = (22250,3307,0)
  Normal = (0,0,1)
  Start = (17343,3307,0)
  expr: End.x = Rectangle.Placement.Base.x + Rectangle.Length
  expr: Start.x = Rectangle007.Placement.Base.x + Rectangle007.Length
FEATURE [App::FeaturePython] InternalObjectName020  label="tc_props018"  # WARN: FeaturePython — macro-defined, semantics opaque (R4)
  altura_desde_piso = 1450
  cantidad_puertos = 2
  corriente_max_a = 15
  estado = L, N, G.
  id_fuente = 0xf14522bc9cb87ff6ac08e4d3595e87cc8402391cad286cdc968dfafc2a4b5dc298c451a97e866045cda84f044d0440fbdb9f54b922d203c2ca75718c1a71f01
  id_pieza_electronica = 0xa1f68b6e6c01046839d0e99019d1522a58fb2f0805ef3b7b690919c9d7eb80abb3be3069f2c974caa8b0089fc70d2755ddb0f68825d76764e4bd6125e6bcb8db
  nombre_propiedad_exportable = tomacorriente_propiedades
  num_circuito = A4
  num_tablero_distribucion = 1
  rotulo_dibujo_tecnico = 4
  tipo = NEMA 5-15R
  voltaje_max_v = 125
FEATURE [App::FeaturePython] InternalObjectName013  label="tc_props011"  # WARN: FeaturePython — macro-defined, semantics opaque (R4)
  altura_desde_piso = 310
  cantidad_puertos = 2
  corriente_max_a = 15
  estado = L, N, G.
  id_fuente = 0x874eed9b51bc1fe7d61575ec539bebd42a2265bddafae5e95cb483d897ee958c2790080c2c5cca061fd49379158c2aa2189feef5be8c0f369b63b2205f3f9df2
  id_pieza_electronica = 0xfb4f2502a1a6b925c37e72cec96adbb37e93dfe94711c0ef28ed0328313e7e5efa458a6b0b2a59504850194aed6aa968661228608d987653728708b88cf1e92a
  nombre_propiedad_exportable = tomacorriente_propiedades
  num_circuito = A1
  num_tablero_distribucion = 1
  rotulo_dibujo_tecnico = 5
  tipo = NEMA 5-15R
  voltaje_max_v = 125
FEATURE [App::FeaturePython] Dimension037  # Draft dimension (typed FeaturePython)
  Diameter = false
  Dimline = (6800,4100,0)
  Direction = (0,0,0)
  Distance = 930
  End = (7080,4330,0)
  Normal = (0,0,1)
  Start = (6150,4330,0)
  expr: End.x = Rectangle003.Placement.Base.x + Rectangle003.Length
  expr: Start.x = Rectangle016.Placement.Base.x + Rectangle016.Length
FEATURE [App::FeaturePython] Dimension025  # Draft dimension (typed FeaturePython)
  Diameter = false
  Dimline = (17703.5,8131.5,0)
  Direction = (0,0,0)
  Distance = 22250
  End = (22250,6037,0)
  Normal = (0,0,1)
  Start = (0,6037,0)
FEATURE [App::FeaturePython] Dimension026  # Draft dimension (typed FeaturePython)
  Diameter = false
  Dimline = (0,2050,0)
  Direction = (0,0,0)
  Distance = 2400
  End = (2400,1650,0)
  Normal = (0,0,1)
  Start = (0,1650,0)
  expr: Dimline.y = Rectangle002.Placement.Base.y + Rectangle002.Height + 0.4m
  expr: Dimline.x = 0
  expr: End.x = Rectangle002.Placement.Base.x + Rectangle002.Length
  expr: Start.x = Rectangle002.Placement.Base.x
FEATURE [App::FeaturePython] Dimension033  # Draft dimension (typed FeaturePython)
  Diameter = false
  Dimline = (4200,6300,0)
  Direction = (0,0,0)
  Distance = 1040
  End = (4240,5025,0)
  Normal = (0,0,1)
  Start = (3200,5025,0)
  expr: Start.x = Rectangle014.Placement.Base.x
  expr: End.x = Rectangle013.Placement.Base.x
FEATURE [App::FeaturePython] Dimension006  # Draft dimension (typed FeaturePython)
  Diameter = false
  Dimline = (9210,0,0)
  Direction = (0,0,0)
  Distance = 3560
  End = (9657,3560,0)
  Normal = (0,0,1)
  Start = (9657,0,0)
  expr: Start.y = Rectangle.Placement.Base.y
  expr: Dimline.x = Rectangle004.Placement.Base.x + Rectangle004.Length - 0.4m
  expr: End.y = Rectangle004.Placement.Base.y
  expr: Start.z = 0
FEATURE [App::FeaturePython] InternalObjectName017  label="tc_props015"  # WARN: FeaturePython — macro-defined, semantics opaque (R4)
  altura_desde_piso = 560
  cantidad_puertos = 2
  corriente_max_a = 15
  estado = L, N, G.
  id_fuente = 0xbcf388a876ad59e150db9e649778259711ae8ae001e35f2e9a573368e7d245dbdc751069158494868d8ecadcc65f5e515f1f001bb60d15e2f0a893148ba9819e
  id_pieza_electronica = 0xbb15a5ad5f6e6a70bdc7926645a3a34638abdd15e1b340f6c4f3a0aeb083990bdb8da51e923ce124200ffe66046ae641dd73d9db16f1325a7aa20f4b112c22a4
  nombre_propiedad_exportable = tomacorriente_propiedades
  num_circuito = B6
  num_tablero_distribucion = 1
  rotulo_dibujo_tecnico = 6
  tipo = NEMA 5-15R
  voltaje_max_v = 125
FEATURE [App::FeaturePython] InternalObjectName018  label="tc_props016"  # WARN: FeaturePython — macro-defined, semantics opaque (R4)
  altura_desde_piso = 1460
  cantidad_puertos = 2
  corriente_max_a = 15
  estado = L, N, G.
  id_fuente = 0x65781d0bdb813b1c4541573e93bcf8093fee21c5aa408b90d56de048cf344b8e79b2116f8aeb34d2c38ead9b9912930cd4b151840caf48cb2c07843523b01167
  id_pieza_electronica = 0x3a7e157db590dc06ae7d0872e7fce9f46039487f99c964d4a49b9feb205f8f945f86b5484409a93ca5fd96b8d6cf95ce872e5059485cf4faf984a5b3c669634a
  nombre_propiedad_exportable = tomacorriente_propiedades
  num_circuito = A4
  num_tablero_distribucion = 1
  observaciones = Debe estar concatenada a GFCI tomacorriente__016
  rotulo_dibujo_tecnico = 7
  tipo = NEMA 5-15R
  voltaje_max_v = 125
FEATURE [App::FeaturePython] InternalObjectName002  label="td_props"  # WARN: FeaturePython — macro-defined, semantics opaque (R4)
  altura_desde_piso = 1500
  corriente_max_fase_a = 300
  id_pieza_electronica = 0xc8eb5b6456095df6fce49f58b56a04ebef77d51c42289577dce8e649cbe8494e8bca16199b9c944a3311ba747a9cc8f5a22a85165ec1c01a2fee0261f0afd909
  nombre_propiedad_exportable = tablero_distribucion_propiedades
  num_circuitos = 42
  num_fases = 3
  num_tablero_distribucion = 1
  rotulo_dibujo_tecnico = 1
  voltaje_max_fase_v = 600
FEATURE [App::FeaturePython] Dimension039  # Draft dimension (typed FeaturePython)
  Diameter = false
  Dimline = (8800,3800,0)
  Direction = (0,0,0)
  Distance = 920
  End = (9500,3560,0)
  Normal = (0,0,1)
  Start = (8580,3560,0)
  expr: End.x = Rectangle020.Placement.Base.x
  expr: Start.x = Rectangle021.Placement.Base.x + Rectangle021.Length
FEATURE [App::FeaturePython] InternalObjectName009  label="tc_props007"  # WARN: FeaturePython — macro-defined, semantics opaque (R4)
  altura_desde_piso = 1940
  cantidad_puertos = 2
  corriente_max_a = 15
  estado = L, N, G.
  id_fuente = 0xd7cd30a301d0bcfad3d0d09c11467a3b4d9712a8cba5f0407f809b4594ecb3e498d92282a094c016cfbb7283a7c3b13a77b24c9ce5ccf875f09f666a7010f318
  id_pieza_electronica = 0x2907803bccff507046d2dd98f6cee4191174b9855e80c58d2a661a9da465e506a31e417e556250f6926cc4b505c2c1b08f9bd61682bf2c78c68f60c136512c95
  nombre_propiedad_exportable = tomacorriente_propiedades
  num_circuito = B4
  num_tablero_distribucion = 1
  rotulo_dibujo_tecnico = 8
  tipo = NEMA 5-15R
  voltaje_max_v = 125
FEATURE [App::FeaturePython] InternalObjectName012  label="tc_props010"  # WARN: FeaturePython — macro-defined, semantics opaque (R4)
  altura_desde_piso = 1130
  cantidad_puertos = 2
  corriente_max_a = 15
  estado = L, N, G.
  id_fuente = 0x391af6861389109aca2b8a86a2413ae5f3b028a301bf15e8b66257a3511780bd13f7415946f1e29bf7df61f64158b954dcdc894433adecfe77c90b9c5890a44e
  id_pieza_electronica = 0x2fbb9b132334c07e3c6f573c437eb3c4be08e064c106e9ca926ef32874296023231f59e3dfb1e498e24da17ceb7b56a9a83c08481db3a50a366fa6ea4e60443e
  nombre_propiedad_exportable = tomacorriente_propiedades
  num_circuito = A1
  num_tablero_distribucion = 1
  rotulo_dibujo_tecnico = 9
  tipo = NEMA 5-15R
  voltaje_max_v = 125
FEATURE [App::FeaturePython] Dimension031  # Draft dimension (typed FeaturePython)
  Diameter = false
  Dimline = (21600,400,0)
  Direction = (0,0,0)
  Distance = 4947
  End = (22250,0,0)
  Normal = (0,0,1)
  Start = (17303,0,0)
  expr: End.x = Rectangle.Placement.Base.x + Rectangle.Length
  expr: Start.x = Rectangle010.Placement.Base.x + Rectangle010.Length
FEATURE [App::FeaturePython] Dimension040  # Draft dimension (typed FeaturePython)
  Diameter = false
  Dimline = (8240,3750,0)
  Direction = (0,0,0)
  Distance = 770
  End = (8580,4430,0)
  Normal = (0,0,1)
  Start = (8580,3660,0)
  expr: End.y = Dimension040.Start.y + 0.77m
  expr: Start.y = Rectangle019.Placement.Base.y + Rectangle019.Height
FEATURE [App::FeaturePython] InternalObjectName015  label="tc_props013"  # WARN: FeaturePython — macro-defined, semantics opaque (R4)
  altura_desde_piso = 400
  cantidad_puertos = 2
  corriente_max_a = 15
  estado = L, N, G.
  id_fuente = 0x46eb679a504e8abedad1842e3a9827fa19a1d845559e8ae3a4991782692c715efe55cdb3c58fc8f2c4e585536260dfae30b388fa00295b52a21152e35e55aed8
  id_pieza_electronica = 0xd6b18e7417508fc1700778bf6043c8a204fd115031e719d429036ad5d5eee64575a6171721977c26654ac1b3565d284d231e21da56f692511ad8c527c7a7974c
  nombre_propiedad_exportable = tomacorriente_propiedades
  num_circuito = B6
  num_tablero_distribucion = 1
  rotulo_dibujo_tecnico = 10
  tipo = NEMA 5-15R
  voltaje_max_v = 125
FEATURE [App::FeaturePython] Dimension036  # Draft dimension (typed FeaturePython)
  Diameter = false
  Dimline = (4600,4100,0)
  Direction = (0,0,0)
  Distance = 930
  End = (5300,4330,0)
  Normal = (0,0,1)
  Start = (4370,4330,0)
  expr: End.x = Rectangle013.Placement.Base.x + Rectangle013.Length + 0.93m
  expr: Start.x = Rectangle013.Placement.Base.x + Rectangle013.Length
FEATURE [App::FeaturePython] InternalObjectName008  label="tc_props006"  # WARN: FeaturePython — macro-defined, semantics opaque (R4)
  altura_desde_piso = 330
  cantidad_puertos = 2
  corriente_max_a = 15
  estado = L y N invertidos; G.
  id_fuente = 0xc82bb2e658b0c0870d9e1fe12326ea2e6711b7d61fbeaee59a3e0408c0f863a6d3a007e5beebb8f2f9335436cf782ea32d3dbcbf4bbb4224406d2d8abb27e254
  id_pieza_electronica = 0x8cedbed9f03a11e81b852e0a818513551fe26d7549b02d6d2d57a6efc1f154b8a0e8635c999515e5389d3a8c3900fd33cec0e9ae243b3dceb667594e31ff73b1
  nombre_propiedad_exportable = tomacorriente_propiedades
  num_circuito = A8
  num_tablero_distribucion = 1
  rotulo_dibujo_tecnico = 11
  tipo = NEMA 5-15R
  voltaje_max_v = 125
FEATURE [App::FeaturePython] Dimension032  # Draft dimension (typed FeaturePython)
  Diameter = false
  Dimline = (505,3060,0)
  Direction = (0,0,0)
  Distance = 7080
  End = (7080,3560,0)
  Normal = (0,0,1)
  Start = (0,3560,0)
  expr: End.x = Rectangle004.Placement.Base.x
  expr: Start.x = Rectangle.Placement.Base.x
FEATURE [App::FeaturePython] InternalObjectName021  label="tc_props019"  # WARN: FeaturePython — macro-defined, semantics opaque (R4)
  altura_desde_piso = 1450
  cantidad_puertos = 2
  corriente_max_a = 15
  estado = L, N, G.
  id_fuente = 0x7ab3a101f201de8b218fe28001b359e20ab514fba8d854cb75c0cf63d74699e0cf9d079a2931bb712a8c5a6ee14f164659745af6931058698da72e616e6f505b
  id_pieza_electronica = 0x218d84c6cd05a2575a118b9d529d49268000bbda99ff104bb9ca94c9a4d77f47b4629d1883cdb8abfcd0ec6d918e41dd3cb9ea4d7360c3712dcd7ca890928c67
  nombre_propiedad_exportable = tomacorriente_propiedades
  num_circuito = A4
  num_tablero_distribucion = 1
  rotulo_dibujo_tecnico = 12
  tipo = NEMA 5-15R
  voltaje_max_v = 125
FEATURE [App::FeaturePython] Dimension034  # Draft dimension (typed FeaturePython)
  Diameter = false
  Dimline = (5300,5700,0)
  Direction = (0,0,0)
  Distance = 1260
  End = (5630,5985,0)
  Normal = (0,0,1)
  Start = (4370,5985,0)
  expr: End.x = Rectangle015.Placement.Base.x
  expr: Start.x = Rectangle013.Placement.Base.x + Rectangle013.Length
FEATURE [App::FeaturePython] Dimension038  # Draft dimension (typed FeaturePython)
  Diameter = false
  Dimline = (6900,5600,0)
  Direction = (0,0,0)
  Distance = 1280
  End = (7080,5915,0)
  Normal = (0,0,1)
  Start = (5800,5915,0)
  expr: End.x = Rectangle003.Placement.Base.x + Rectangle003.Length
  expr: Start.x = Rectangle015.Placement.Base.x + Rectangle015.Length
FEATURE [App::FeaturePython] Dimension  # Draft dimension (typed FeaturePython)
  Diameter = false
  Dimline = (4000,5500,0)
  Direction = (0,0,0)
  Distance = 960
  End = (4240,5985,0)
  Normal = (0,0,1)
  Start = (4240,5025,0)
  expr: End.y = Rectangle003.Placement.Base.y + Rectangle003.Height
  expr: Start.y = Rectangle014.Placement.Base.y + Rectangle014.Height
FEATURE [App::FeaturePython] InternalObjectName006  label="tc_props004"  # WARN: FeaturePython — macro-defined, semantics opaque (R4)
  altura_desde_piso = 320
  cantidad_puertos = 2
  corriente_max_a = 15
  estado = L y N invertidos, G.
  id_fuente = 0xfeb35e884f74d422bcd14078d8de34cf825495bc0775f18f06fda2645f8f99639860ee31012fd3ddeb11bf8aa981b506fabce6fa7de41c8e7fbad1322792d227
  id_pieza_electronica = 0xeeffbd10854baaf7f3e64d1a56fcf5cf7913d06dd9fecc448c6c206e7f6e3e6a85bdefb8706aaafc807f5aa2217b7f88f564ae6ba1d23e2aeb1f77d90d41483
  nombre_propiedad_exportable = tomacorriente_propiedades
  num_circuito = B4
  num_tablero_distribucion = 1
  rotulo_dibujo_tecnico = 13
  tipo = NEMA 5-15R
  voltaje_max_v = 125
FEATURE [App::FeaturePython] InternalObjectName003  label="tc_props001"  # WARN: FeaturePython — macro-defined, semantics opaque (R4)
  altura_desde_piso = 330
  cantidad_puertos = 2
  corriente_max_a = 15
  estado = L, N, G
  id_fuente = 0xf5db690303be48231b605651f768d6bac08fe16e07165d508897d6925a6e770ccf0644fced992dd8f38d19914443c5e19313a84c87d8546359154120b8fbf64
  id_pieza_electronica = 0x6ec3591f9aa899c47aafab0921fddc225459d2369249050c8490030ebaa9c0e55f244d4f31af4ef9e53275a11ddf35dea2ff1105acfac40cc303d82886ad2d73
  nombre_propiedad_exportable = tomacorriente_propiedades
  num_circuito = B8
  num_tablero_distribucion = 1
  rotulo_dibujo_tecnico = 14
  tipo = NEMA 5-15R
  voltaje_max_v = 125
FEATURE [App::FeaturePython] InternalObjectName010  label="tc_props008"  # WARN: FeaturePython — macro-defined, semantics opaque (R4)
  altura_desde_piso = 2000
  cantidad_puertos = 2
  corriente_max_a = 15
  estado = L, N, G.
  id_fuente = 0x5e97cbe3fd32d58b4557b161e4c08c111d7f097c1a4b51c6234f1778537cc7bfa57ba3adce652a83ca4642e97e61f5abdd0a071e2491e09196f90621f5156ee9
  id_pieza_electronica = 0x34cd1024556017df514a7c24524733a14391ff35dd5e89ab4aa2c570a026fa6b2f3e4e7aaa955320f517a46ef1a65b604ba62abf201de062aa6ed917ead93c40
  nombre_propiedad_exportable = tomacorriente_propiedades
  num_circuito = B7
  num_tablero_distribucion = 1
  rotulo_dibujo_tecnico = 15
  tipo = NEMA 5-15R
  voltaje_max_v = 125
FEATURE [App::FeaturePython] InternalObjectName005  label="tc_props003"  # WARN: FeaturePython — macro-defined, semantics opaque (R4)
  altura_desde_piso = 330
  cantidad_puertos = 2
  corriente_max_a = 15
  estado = L, N, G
  id_fuente = 0x81f14184a2a4a30d95475c68da8cbd7524e3b82a8c93a557d76401401dc2c9838e7e5af2541cb8f9395928b5ed0d25392655fbb26fe03817e67d673ceb1af445
  id_pieza_electronica = 0x766e4a73579b40b46775585ca4c42fdda5c5a379b29c92b5aaf3a2378ef10f6f09fedf02c0fcae53e7d5032ab12e00193a3bf377616e09ecaa1d9b771313e2ee
  nombre_propiedad_exportable = tomacorriente_propiedades
  num_circuito = B8
  num_tablero_distribucion = 1
  rotulo_dibujo_tecnico = 16
  tipo = NEMA 5-15R
  voltaje_max_v = 125
FEATURE [App::FeaturePython] InternalObjectName007  label="tc_props005"  # WARN: FeaturePython — macro-defined, semantics opaque (R4)
  altura_desde_piso = 410
  cantidad_puertos = 2
  corriente_max_a = 15
  estado = L, N, G.
  id_fuente = 0x665097ff78f46b57a6125891b64b68ca06b431f47543bf54ae6f6808aecf090320c95089b7e84d78fec075a385d7312619f1d9174b0ec80732b238c224be7af5
  id_pieza_electronica = 0x5e45cba10b988935387b2740fd61d080a8f9d3d7eb066e0a2e099b6139bd34dac0f13c20e87a58d33f61391c641cb1d716bc7c9130d0af228a49f05ef9d50f37
  nombre_propiedad_exportable = tomacorriente_propiedades
  num_circuito = B6
  num_tablero_distribucion = 1
  rotulo_dibujo_tecnico = 17
  tipo = NEMA 5-15R
  voltaje_max_v = 125
FEATURE [App::FeaturePython] InternalObjectName  label="tc_props"  # WARN: FeaturePython — macro-defined, semantics opaque (R4)
  altura_desde_piso = 330
  cantidad_puertos = 2
  corriente_max_a = 15
  estado = L, N, G
  id_fuente = 0xfd4944d92f3c6049cdd6926a99967659a9bb1adf1c51b8385cd095234acb666ff5545af3ee4a1f6200dd54c66a2cfac21cf4c99e1da2717207288bfe2d91292b
  id_pieza_electronica = 0xbd44f305e6f17ee24c27be025f6b310706d490e13664639e95096e2e46f3c6c437a012ce6d740acd7b4113321514fa3871599287d92a5dbc4884eb94a4dc209a
  nombre_propiedad_exportable = tomacorriente_propiedades
  num_circuito = B8
  num_tablero_distribucion = 1
  rotulo_dibujo_tecnico = 18
  tipo = NEMA 5-15R
  voltaje_max_v = 125
FEATURE [App::FeaturePython] InternalObjectName011  label="tc_props009"  # WARN: FeaturePython — macro-defined, semantics opaque (R4)
  altura_desde_piso = 330
  cantidad_puertos = 2
  corriente_max_a = 15
  estado = L, N, G.
  id_fuente = 0x5ef3e909c8d3d0a83fbd561c78ea5d1a91853290c2b1fa7fbf866f871238b6684eb1d65d1cf4964a10fa76569c4e534c2e2394a67fd80d5e6dfebbbaa1da4465
  id_pieza_electronica = 0xaa309e69d4a5665d92167e1c602cc2a36fa08646a2ff4768467acc3baa554c3f2c4b0be34b1cb266c0d2cd3784b27bef7eb0938416154e5306cdd2b0f8636629
  nombre_propiedad_exportable = tomacorriente_propiedades
  num_circuito = A1
  num_tablero_distribucion = 1
  rotulo_dibujo_tecnico = 19
  tipo = NEMA 5-15R
  voltaje_max_v = 125
FEATURE [Part::FeaturePython] Point  # WARN: FeaturePython — macro-defined, semantics opaque (R4)
  X = -20
  Y = 10
  Z = 0
FEATURE [Part::FeaturePython] Point002  # WARN: FeaturePython — macro-defined, semantics opaque (R4)
  X = -10
  Y = 0
  Z = 0
FEATURE [Part::FeaturePython] Point003  # WARN: FeaturePython — macro-defined, semantics opaque (R4)
  X = -40
  Y = 0
  Z = 0
FEATURE [Part::FeaturePython] Point001  # WARN: FeaturePython — macro-defined, semantics opaque (R4)
  X = -20
  Y = 0
  Z = 0
FEATURE [Part::Part2DObjectPython] Circle088  # Draft 2D object (typed FeaturePython)
  FirstAngle = 0
  LastAngle = 0
  MakeFace = true
  Radius = 100
FEATURE [Part::Part2DObjectPython] Circle093  # Draft 2D object (typed FeaturePython)
  FirstAngle = 0
  LastAngle = 0
  MakeFace = true
  Radius = 100
FEATURE [Part::Part2DObjectPython] Line182  # Draft 2D object (typed FeaturePython)
  ChamferSize = 0
  Closed = false
  End = (0,-100,0)
  FilletRadius = 0
  Length = 200
  MakeFace = true
  Placement = pos=(0,100,0) rot=(0,0,1;0rad)
  Points = (2) [(0,0,0),(0,-200,0)]
  Start = (0,100,0)
  Subdivisions = 0
FEATURE [Part::Part2DObjectPython] Line197  # Draft 2D object (typed FeaturePython)
  ChamferSize = 0
  Closed = false
  End = (-100,3.8e-15,0)
  FilletRadius = 0
  Length = 200
  MakeFace = true
  Placement = pos=(100,1.8e-14,0) rot=(0,0,1;0rad)
  Points = (2) [(0,0,0),(-200,-1.42109e-14,0)]
  Start = (100,1.8e-14,0)
  Subdivisions = 0
FEATURE [Part::Part2DObjectPython] Line196  # Draft 2D object (typed FeaturePython)
  ChamferSize = 0
  Closed = false
  End = (0,-100,0)
  FilletRadius = 0
  Length = 200
  MakeFace = true
  Placement = pos=(0,100,0) rot=(0,0,1;0rad)
  Points = (2) [(0,0,0),(0,-200,0)]
  Start = (0,100,0)
  Subdivisions = 0
FEATURE [Part::Part2DObjectPython] Line186  # Draft 2D object (typed FeaturePython)
  ChamferSize = 0
  Closed = false
  End = (0,-100,0)
  FilletRadius = 0
  Length = 200
  MakeFace = true
  Placement = pos=(0,100,0) rot=(0,0,1;0rad)
  Points = (2) [(0,0,0),(0,-200,0)]
  Start = (0,100,0)
  Subdivisions = 0
FEATURE [Part::Part2DObjectPython] Circle087  # Draft 2D object (typed FeaturePython)
  FirstAngle = 0
  LastAngle = 0
  MakeFace = true
  Radius = 100
FEATURE [Part::Part2DObjectPython] Circle090  # Draft 2D object (typed FeaturePython)
  FirstAngle = 0
  LastAngle = 0
  MakeFace = true
  Radius = 100
FEATURE [Part::Part2DObjectPython] Line185  # Draft 2D object (typed FeaturePython)
  ChamferSize = 0
  Closed = false
  End = (-100,3.8e-15,0)
  FilletRadius = 0
  Length = 200
  MakeFace = true
  Placement = pos=(100,1.8e-14,0) rot=(0,0,1;0rad)
  Points = (2) [(0,0,0),(-200,-1.42109e-14,0)]
  Start = (100,1.8e-14,0)
  Subdivisions = 0
FEATURE [Part::Part2DObjectPython] Line179  # Draft 2D object (typed FeaturePython)
  ChamferSize = 0
  Closed = false
  End = (-100,3.8e-15,0)
  FilletRadius = 0
  Length = 200
  MakeFace = true
  Placement = pos=(100,1.8e-14,0) rot=(0,0,1;0rad)
  Points = (2) [(0,0,0),(-200,-1.42109e-14,0)]
  Start = (100,1.8e-14,0)
  Subdivisions = 0
FEATURE [Part::Part2DObjectPython] Line178  # Draft 2D object (typed FeaturePython)
  ChamferSize = 0
  Closed = false
  End = (0,-100,0)
  FilletRadius = 0
  Length = 200
  MakeFace = true
  Placement = pos=(0,100,0) rot=(0,0,1;0rad)
  Points = (2) [(0,0,0),(0,-200,0)]
  Start = (0,100,0)
  Subdivisions = 0
FEATURE [Part::Part2DObjectPython] Circle089  # Draft 2D object (typed FeaturePython)
  FirstAngle = 0
  LastAngle = 0
  MakeFace = true
  Radius = 100
FEATURE [App::Part] Part237  label="contenido076"
  Group = -> [Circle089,Line178,Line179]
  Origin = -> Origin237
  Placement = pos=(0,0,0) rot=(0,0,1;0.785398rad)
FEATURE [Part::Part2DObjectPython] Circle099  # Draft 2D object (typed FeaturePython)
  FirstAngle = 0
  LastAngle = 0
  MakeFace = true
  Radius = 100
FEATURE [Part::Part2DObjectPython] Line184  # Draft 2D object (typed FeaturePython)
  ChamferSize = 0
  Closed = false
  End = (0,-100,0)
  FilletRadius = 0
  Length = 200
  MakeFace = true
  Placement = pos=(0,100,0) rot=(0,0,1;0rad)
  Points = (2) [(0,0,0),(0,-200,0)]
  Start = (0,100,0)
  Subdivisions = 0
FEATURE [Part::Part2DObjectPython] Circle092  # Draft 2D object (typed FeaturePython)
  FirstAngle = 0
  LastAngle = 0
  MakeFace = true
  Radius = 100
FEATURE [Part::Part2DObjectPython] Line198  # Draft 2D object (typed FeaturePython)
  ChamferSize = 0
  Closed = false
  End = (0,-100,0)
  FilletRadius = 0
  Length = 200
  MakeFace = true
  Placement = pos=(0,100,0) rot=(0,0,1;0rad)
  Points = (2) [(0,0,0),(0,-200,0)]
  Start = (0,100,0)
  Subdivisions = 0
FEATURE [Part::Part2DObjectPython] Line169  # Draft 2D object (typed FeaturePython)
  ChamferSize = 0
  Closed = false
  End = (-100,3.8e-15,0)
  FilletRadius = 0
  Length = 200
  MakeFace = true
  Placement = pos=(100,1.8e-14,0) rot=(0,0,1;0rad)
  Points = (2) [(0,0,0),(-200,-1.42109e-14,0)]
  Start = (100,1.8e-14,0)
  Subdivisions = 0
FEATURE [Part::Part2DObjectPython] Line176  # Draft 2D object (typed FeaturePython)
  ChamferSize = 0
  Closed = false
  End = (0,-100,0)
  FilletRadius = 0
  Length = 200
  MakeFace = true
  Placement = pos=(0,100,0) rot=(0,0,1;0rad)
  Points = (2) [(0,0,0),(0,-200,0)]
  Start = (0,100,0)
  Subdivisions = 0
FEATURE [Part::Part2DObjectPython] Line160  # Draft 2D object (typed FeaturePython)
  ChamferSize = 0
  Closed = false
  End = (0,-100,0)
  FilletRadius = 0
  Length = 200
  MakeFace = true
  Placement = pos=(0,100,0) rot=(0,0,1;0rad)
  Points = (2) [(0,0,0),(0,-200,0)]
  Start = (0,100,0)
  Subdivisions = 0
FEATURE [App::Part] Part219  label="contenido067"
  Group = -> [Circle080,Line160,Line161]
  Origin = -> Origin219
  Placement = pos=(0,0,0) rot=(0,0,1;0.785398rad)
FEATURE [Part::Part2DObjectPython] Circle084  # Draft 2D object (typed FeaturePython)
  FirstAngle = 0
  LastAngle = 0
  MakeFace = true
  Radius = 100
FEATURE [Part::Part2DObjectPython] Circle091  # Draft 2D object (typed FeaturePython)
  FirstAngle = 0
  LastAngle = 0
  MakeFace = true
  Radius = 100
FEATURE [App::Part] Part241  label="contenido078"
  Group = -> [Circle091,Line182,Line183]
  Origin = -> Origin241
  Placement = pos=(0,0,0) rot=(0,0,1;0.785398rad)
FEATURE [Part::Part2DObjectPython] Line174  # Draft 2D object (typed FeaturePython)
  ChamferSize = 0
  Closed = false
  End = (0,-100,0)
  FilletRadius = 0
  Length = 200
  MakeFace = true
  Placement = pos=(0,100,0) rot=(0,0,1;0rad)
  Points = (2) [(0,0,0),(0,-200,0)]
  Start = (0,100,0)
  Subdivisions = 0
FEATURE [App::Part] Part227  label="contenido071"
  Group = -> [Circle084,Line168,Line169]
  Origin = -> Origin227
  Placement = pos=(0,0,0) rot=(0,0,1;0.785398rad)
FEATURE [Part::Part2DObjectPython] Line181  # Draft 2D object (typed FeaturePython)
  ChamferSize = 0
  Closed = false
  End = (-100,3.8e-15,0)
  FilletRadius = 0
  Length = 200
  MakeFace = true
  Placement = pos=(100,1.8e-14,0) rot=(0,0,1;0rad)
  Points = (2) [(0,0,0),(-200,-1.42109e-14,0)]
  Start = (100,1.8e-14,0)
  Subdivisions = 0
FEATURE [Part::Part2DObjectPython] Line180  # Draft 2D object (typed FeaturePython)
  ChamferSize = 0
  Closed = false
  End = (0,-100,0)
  FilletRadius = 0
  Length = 200
  MakeFace = true
  Placement = pos=(0,100,0) rot=(0,0,1;0rad)
  Points = (2) [(0,0,0),(0,-200,0)]
  Start = (0,100,0)
  Subdivisions = 0
FEATURE [App::Part] Part239  label="contenido077"
  Group = -> [Circle090,Line180,Line181]
  Origin = -> Origin239
  Placement = pos=(0,0,0) rot=(0,0,1;0.785398rad)
FEATURE [Part::Part2DObjectPython] Line172  # Draft 2D object (typed FeaturePython)
  ChamferSize = 0
  Closed = false
  End = (0,-100,0)
  FilletRadius = 0
  Length = 200
  MakeFace = true
  Placement = pos=(0,100,0) rot=(0,0,1;0rad)
  Points = (2) [(0,0,0),(0,-200,0)]
  Start = (0,100,0)
  Subdivisions = 0
FEATURE [App::Part] Part231  label="contenido073"
  Group = -> [Circle086,Line172,Line173]
  Origin = -> Origin231
  Placement = pos=(0,0,0) rot=(0,0,1;0.785398rad)
FEATURE [Part::Part2DObjectPython] Line175  # Draft 2D object (typed FeaturePython)
  ChamferSize = 0
  Closed = false
  End = (-100,3.8e-15,0)
  FilletRadius = 0
  Length = 200
  MakeFace = true
  Placement = pos=(100,1.8e-14,0) rot=(0,0,1;0rad)
  Points = (2) [(0,0,0),(-200,-1.42109e-14,0)]
  Start = (100,1.8e-14,0)
  Subdivisions = 0
FEATURE [App::Part] Part233  label="contenido074"
  Group = -> [Circle087,Line174,Line175]
  Origin = -> Origin233
  Placement = pos=(0,0,0) rot=(0,0,1;0.785398rad)
FEATURE [Part::Part2DObjectPython] Line167  # Draft 2D object (typed FeaturePython)
  ChamferSize = 0
  Closed = false
  End = (-100,3.8e-15,0)
  FilletRadius = 0
  Length = 200
  MakeFace = true
  Placement = pos=(100,1.8e-14,0) rot=(0,0,1;0rad)
  Points = (2) [(0,0,0),(-200,-1.42109e-14,0)]
  Start = (100,1.8e-14,0)
  Subdivisions = 0
FEATURE [App::Part] Part225  label="contenido070"
  Group = -> [Circle083,Line166,Line167]
  Origin = -> Origin225
  Placement = pos=(0,0,0) rot=(0,0,1;0.785398rad)
FEATURE [App::Part] Part223  label="contenido069"
  Group = -> [Circle082,Line164,Line165]
  Origin = -> Origin223
  Placement = pos=(0,0,0) rot=(0,0,1;0.785398rad)
FEATURE [Part::Part2DObjectPython] Line162  # Draft 2D object (typed FeaturePython)
  ChamferSize = 0
  Closed = false
  End = (0,-100,0)
  FilletRadius = 0
  Length = 200
  MakeFace = true
  Placement = pos=(0,100,0) rot=(0,0,1;0rad)
  Points = (2) [(0,0,0),(0,-200,0)]
  Start = (0,100,0)
  Subdivisions = 0
FEATURE [App::Part] Part221  label="contenido068"
  Group = -> [Circle081,Line162,Line163]
  Origin = -> Origin221
  Placement = pos=(0,0,0) rot=(0,0,1;0.785398rad)
FEATURE [Part::Part2DObjectPython] Line171  # Draft 2D object (typed FeaturePython)
  ChamferSize = 0
  Closed = false
  End = (-100,3.8e-15,0)
  FilletRadius = 0
  Length = 200
  MakeFace = true
  Placement = pos=(100,1.8e-14,0) rot=(0,0,1;0rad)
  Points = (2) [(0,0,0),(-200,-1.42109e-14,0)]
  Start = (100,1.8e-14,0)
  Subdivisions = 0
FEATURE [Part::Part2DObjectPython] Line177  # Draft 2D object (typed FeaturePython)
  ChamferSize = 0
  Closed = false
  End = (-100,3.8e-15,0)
  FilletRadius = 0
  Length = 200
  MakeFace = true
  Placement = pos=(100,1.8e-14,0) rot=(0,0,1;0rad)
  Points = (2) [(0,0,0),(-200,-1.42109e-14,0)]
  Start = (100,1.8e-14,0)
  Subdivisions = 0
FEATURE [Part::Part2DObjectPython] Circle085  # Draft 2D object (typed FeaturePython)
  FirstAngle = 0
  LastAngle = 0
  MakeFace = true
  Radius = 100
FEATURE [App::Part] Part229  label="contenido072"
  Group = -> [Circle085,Line170,Line171]
  Origin = -> Origin229
  Placement = pos=(0,0,0) rot=(0,0,1;0.785398rad)
FEATURE [App::Part] Part243  label="contenido079"
  Group = -> [Circle092,Line184,Line185]
  Origin = -> Origin243
  Placement = pos=(0,0,0) rot=(0,0,1;0.785398rad)
FEATURE [Part::Part2DObjectPython] Line187  # Draft 2D object (typed FeaturePython)
  ChamferSize = 0
  Closed = false
  End = (-100,3.8e-15,0)
  FilletRadius = 0
  Length = 200
  MakeFace = true
  Placement = pos=(100,1.8e-14,0) rot=(0,0,1;0rad)
  Points = (2) [(0,0,0),(-200,-1.42109e-14,0)]
  Start = (100,1.8e-14,0)
  Subdivisions = 0
FEATURE [App::Part] Part235  label="contenido075"
  Group = -> [Circle088,Line176,Line177]
  Origin = -> Origin235
  Placement = pos=(0,0,0) rot=(0,0,1;0.785398rad)
FEATURE [App::FeaturePython] InternalObjectName064  label="luz_8in_props013"  # WARN: FeaturePython — macro-defined, semantics opaque (R4)
  altura_desde_piso = 0
  fuente = 0xf14623025ac55d36651701217b5500468671db5aece4180de1e397691b516df76385c49eda21b289d108adb05feff80badbb931b03b018717ff431ab7f54e52b
  id_pieza_electronica = 0x722ebd42f727bc84af8664655eeccbaab1a7e75be228a74c17e4be0e5c624fb4c3772c0a94adb449e3576c9a5c54f6d96052198aa774f4e4fba3205929a74f71
  nombre_propiedad_exportable = luz_propiedades
  potencia_w = 18
  rotulo_dibujo_tecnico = 17
  tipo_luz = Led
  voltaje_max_v = 130
  voltaje_min_v = 95
  voltaje_nominal_v = 110
FEATURE [App::FeaturePython] Text010  # WARN: FeaturePython — macro-defined, semantics opaque (R4)
  Placement = pos=(-12.7272,-15.1048,0) rot=(0,0,1;0rad)
  Text = F
FEATURE [App::FeaturePython] InternalObjectName031  label="tc_props029"  # WARN: FeaturePython — macro-defined, semantics opaque (R4)
  altura_desde_piso = 1460
  cantidad_puertos = 2
  corriente_max_a = 15
  estado = L, N, G.
  id_fuente = 0x8d29896774e416358b3d8bcde893cc70d1fcfd539cab34334f9687549bd7943b4734d231bfb63d16a8cdbfb269dd33458c9fe34f3a3003148e417b1b5182aa1f
  id_pieza_electronica = 0xe305c9b2b9026b46589e4d65fb8df1b84f69eb9a03e51fb328af6296a700f3a0990a92a5b3ea76460b36a277b24cb3fb143be819e9724f5592996e77612f49f0
  nombre_propiedad_exportable = tomacorriente_propiedades
  num_circuito = A4
  num_tablero_distribucion = 1
  rotulo_dibujo_tecnico = 20
  tipo = NEMA 5-15R
  voltaje_max_v = 125
FEATURE [App::FeaturePython] InternalObjectName036  label="i1_propiedades001"  # WARN: FeaturePython — macro-defined, semantics opaque (R4)
  altura_desde_piso = 0
  corriente_max_a = 10
  id_fuente = 0x2e683104a577ce0fb36871dbdc6e69fd6e2ba2171efbcb94766a2679e0037e1f7f0aabcef172b7ad9b437440c65f5852d16d0ee2640fb58a6a9501282559becc
  id_pieza_electronica = 0x7f7a78e97dd208c283cf3c17d35bf91514e53c57256924beb20f68331696ace733aedabdb8386c453e0040712097f728c385fa071799bef12114d8d5a54995cd
  nombre_propiedad_exportable = interruptor_propiedades
  rotulo_dibujo_tecnico = 1
  tipo_interruptor = Ordinario sencillo
  voltaje_max_v = 250
FEATURE [App::FeaturePython] InternalObjectName022  label="tc_props020"  # WARN: FeaturePython — macro-defined, semantics opaque (R4)
  altura_desde_piso = 380
  cantidad_puertos = 2
  corriente_max_a = 15
  estado = L, N, sin G.
  id_fuente = 0x900598c312b6e5f3661b67b87bae7c3d6b4c311721025ef33a18a1cd1e50908e8c9956ab695e032c4f27f5362eb475296a2e04f3c81046d089705f7bd7c24526
  id_pieza_electronica = 0xf1aee878073f9df26a8339284b8ed00c969d03b9ae246d20a23d9495cd4ae02e7981ec3c04a3f629f0c84f00b819d0e27827f57566ace19fba03a2955f458c3b
  nombre_propiedad_exportable = tomacorriente_propiedades
  num_circuito = A4
  num_tablero_distribucion = 1
  rotulo_dibujo_tecnico = 21
  tipo = NEMA 5-15R
  voltaje_max_v = 125
FEATURE [App::FeaturePython] InternalObjectName024  label="tc_props022"  # WARN: FeaturePython — macro-defined, semantics opaque (R4)
  altura_desde_piso = 1450
  cantidad_puertos = 2
  corriente_max_a = 15
  estado = L, N; G débil.
  id_fuente = 0xa6e041fb1ebee132d4bc163e92e9c2a429c2ddad3535bcce09ee14cef530f12a9f3723f9f26e2cc08bf58b9bc2d33b71651a17aa8ed2211a4f4eb372089ebf28
  id_pieza_electronica = 0x79805402daa96690e85a44d2ff0a48bdf4622da61303b5c967dce4d02bebeffcedbaee6ee65678edfdffb054750b3ff67f4cab566c68b546fafb63d77419629d
  nombre_propiedad_exportable = tomacorriente_propiedades
  num_circuito = A5
  num_tablero_distribucion = 1
  rotulo_dibujo_tecnico = 22
  tipo = NEMA 5-15R
  voltaje_max_v = 125
FEATURE [App::FeaturePython] InternalObjectName090  label="extractor_aire_props002"  # WARN: FeaturePython — macro-defined, semantics opaque (R4)
  altura_desde_piso = 0
  fuente = 0xef58752039e4a8f0acecb384f0379304976ef84bd278df85f9b58796f06915d30a1e06d9f628ea5e7d7381c4c95167e2dcd6510dd05e7b11c94ed1ffee9fd841
  id_pieza_electronica = 0x65179ff9fdb64c97c83ac05a7a1e39b6c5f531598e0b8d1b8d9ac632597a99af083414cbf3810481b1c7783489dec89b4bbfd7334ddd2900c6c116fff35d3e7f
  nombre_propiedad_exportable = extractor_aire_propiedades
  potencia_w = 60
  rotulo_dibujo_tecnico = 3
  tipo = Extractor de aire
  voltaje_max_v = 130
  voltaje_min_v = 95
  voltaje_nominal_v = 110
FEATURE [App::FeaturePython] Dimension042  # Draft dimension (typed FeaturePython)
  Diameter = false
  Dimline = (16940,250,0)
  Direction = (0,0,0)
  Distance = 1190
  End = (17193,0,0)
  Normal = (0,0,1)
  Start = (16003,0,0)
  expr: End.x = Rectangle024.Placement.Base.x
  expr: Start.x = Rectangle008.Placement.Base.x + Rectangle008.Length
FEATURE [App::FeaturePython] Dimension043  # Draft dimension (typed FeaturePython)
  Diameter = false
  Dimline = (15640,150,0)
  Direction = (0,0,0)
  Distance = 1120
  End = (16003,0,0)
  Normal = (0,0,1)
  Start = (16003,1120,0)
FEATURE [App::FeaturePython] InternalObjectName038  label="i1_propiedades003"  # WARN: FeaturePython — macro-defined, semantics opaque (R4)
  altura_desde_piso = 0
  corriente_max_a = 10
  id_fuente = 0xcf824308c26b4bc49cd993cbc13ed6852bca3eb1d5bab61a409d8072f694631f5ab20ce62c70424b32a7c0207ae948de3ca1d420f4f2de424a60ad834f8b6e45
  id_pieza_electronica = 0x83d92db75970a29bc798abc1465725255540ece830c242efcfb55aa3d22c6767ff2361f2fe9beb449db8bc9dab12fa4eee8d835aa050335c3495fa4e15cfea2c
  nombre_propiedad_exportable = interruptor_propiedades
  rotulo_dibujo_tecnico = 2
  tipo_interruptor = Ordinario sencillo
  voltaje_max_v = 250
FEATURE [App::FeaturePython] InternalObjectName004  label="i1_propiedades"  # WARN: FeaturePython — macro-defined, semantics opaque (R4)
  altura_desde_piso = 0
  corriente_max_a = 10
  id_fuente = 0x8ed5687683202fcaf4b553b8e1250b5ab0801d50a7dee0820185398325bcd132da3e54b34761ea7b2630f278496c20a566a0e9e8aef6fa40adb70d12986dca36
  id_pieza_electronica = 0x114bfb3fd8442330b17bad5aab63d5af7edd18c4cb1a11418142d24e4a9fe441b731f2f9b3020081b4b5084b91d083f962951e9a0138ce86737e2b0148b74b62
  nombre_propiedad_exportable = interruptor_propiedades
  rotulo_dibujo_tecnico = 3
  tipo_interruptor = Ordinario sencillo
  voltaje_max_v = 250
FEATURE [App::FeaturePython] InternalObjectName026  label="tc_props024"  # WARN: FeaturePython — macro-defined, semantics opaque (R4)
  altura_desde_piso = 1460
  cantidad_puertos = 2
  corriente_max_a = 15
  estado = L, N, G.
  id_fuente = 0x92b7e1da718fa4a7e7c145fbcaa3a955d9e3b4d82d6bf386e3484a26ce74255e19af689467c6d054cda93f1e12e5ff323079ca2d86debccfbc2a5ae14aee79d5
  id_pieza_electronica = 0xeea2432cf1fc712e3de5b04683f7bdc8fd0eab6e522d360ceae81539624cdaf2a20b668e2a870948dc7b3b53321222f9f23d34bdd32f6613252a322477f4b5b3
  nombre_propiedad_exportable = tomacorriente_propiedades
  num_circuito = A5
  num_tablero_distribucion = 1
  rotulo_dibujo_tecnico = 23
  tipo = NEMA 5-15R
  voltaje_max_v = 125
FEATURE [App::FeaturePython] InternalObjectName027  label="tc_props025"  # WARN: FeaturePython — macro-defined, semantics opaque (R4)
  altura_desde_piso = 1460
  cantidad_puertos = 2
  corriente_max_a = 15
  estado = L y N invertidos, G.
  id_fuente = 0xde6c1d7c4d542a625ac05d158f7647a3599b8efebe960a69a4779beff67891243677f45ef24c7cc6b735407c7a889d3803aeee21abc980408bf6cbc691cba65a
  id_pieza_electronica = 0x9dfccd3ef849611e4e2f1035831deccd55fed9847c25acc3bc524c6cac75df157f40918734cf2c57b9662df1110fea13198a0519d9c671c7e4ab5f2ddd845c35
  nombre_propiedad_exportable = tomacorriente_propiedades
  num_circuito = A5
  num_tablero_distribucion = 1
  rotulo_dibujo_tecnico = 24
  tipo = NEMA 5-15R
  voltaje_max_v = 125
FEATURE [App::FeaturePython] InternalObjectName029  label="tc_props027"  # WARN: FeaturePython — macro-defined, semantics opaque (R4)
  altura_desde_piso = 1460
  cantidad_puertos = 2
  corriente_max_a = 15
  estado = L, N; sin G.
  id_fuente = 0x5af78fb257b3afccc5359254e398c4d88f332e26fa727365b7f9133ae29558a7f649f90333bf4bb0406ff6b7076b56c87e149f28af671d34663fd59b9f30f9da
  id_pieza_electronica = 0xc61dd55b852742e8358247cde2e1c300e2f4f92448ecb0a9c95e03a267710fd0b125fd05704210ee9f8fea4a09393b44732859be77703a5137a950b3bef4b14e
  nombre_propiedad_exportable = tomacorriente_propiedades
  num_circuito = A5
  num_tablero_distribucion = 1
  rotulo_dibujo_tecnico = 25
  tipo = NEMA 5-15R
  voltaje_max_v = 125
FEATURE [App::FeaturePython] InternalObjectName028  label="tc_props026"  # WARN: FeaturePython — macro-defined, semantics opaque (R4)
  altura_desde_piso = 1460
  cantidad_puertos = 2
  corriente_max_a = 15
  estado = L, N, G.
  id_fuente = 0x4af4f3df5f4c5b93f19ffbf3bcc3733f5181d8c9f2b38531642c33b4530cf4ed6545cdb8f9965e6be9446edaa7ce6fc165775c7131f2af02ee448cb84b80a45f
  id_pieza_electronica = 0x3e8d771f0e8f3b4ca9ac649291f126221d1c354505e761000b3ecbe31d92356902e29b8e991ecb3854761f6567946f6ca4b2c449f1c6232ff947849bda94c6ac
  nombre_propiedad_exportable = tomacorriente_propiedades
  num_circuito = A5
  num_tablero_distribucion = 1
  rotulo_dibujo_tecnico = 26
  tipo = NEMA 5-15R
  voltaje_max_v = 125
FEATURE [App::FeaturePython] InternalObjectName043  label="i1_propiedades008"  # WARN: FeaturePython — macro-defined, semantics opaque (R4)
  altura_desde_piso = 0
  corriente_max_a = 10
  id_fuente = 0xef58752039e4a8f0acecb384f0379304976ef84bd278df85f9b58796f06915d30a1e06d9f628ea5e7d7381c4c95167e2dcd6510dd05e7b11c94ed1ffee9fd841
  id_pieza_electronica = 0xe203afa9d4d2ca7606c1764f10ed9b93c7a5b14c551ea66a7dd2f0a1b5a9211445ba00bc84a2db279d28daca22dd42532b37a8b18501b2696aeae9492b0731dd
  nombre_propiedad_exportable = interruptor_propiedades
  rotulo_dibujo_tecnico = 4
  tipo_interruptor = Ordinario sencillo
  voltaje_max_v = 250
FEATURE [App::FeaturePython] InternalObjectName035  label="i2_props"  # WARN: FeaturePython — macro-defined, semantics opaque (R4)
  altura_desde_piso = 0
  corriente_max_int1_a = 0
  corriente_max_int2_a = 0
  id_fuente_int1 = 0xa6b747dd543425b3fddbc71975ed6f6c790c91f17e2eeea383e70be2b568e8bfd080fa52381a5773a3fd7c6516a0ce04d2bec9aa10d5f26d3fe61067149434ea
  id_fuente_int2 = 0x2a5ef6aad8df837cd1e8773eee2ea5a31ed24f6fdf59a5283df9cc645620957a7c6dc3a1d72d187bc2b47b420547c8c248d6e1f972ccddad9e0611697ad8f5e
  id_pieza_electronica = 0xa56c510a1a554dc5eeda6ce771e2dec2e31e2d6172213c54be0a4c76c050563e9feda018c93fd5fbdf41ac9f126dcdcb28296fac264e81e5cb1b18dfc1cb0f63
  nombre_propiedad_exportable = interruptor2_propiedades
  rotulo_dibujo_tecnico = 5
  voltaje_max_int1_v = 0
  voltaje_max_int2_v = 0
FEATURE [App::FeaturePython] Dimension041  # Draft dimension (typed FeaturePython)
  Diameter = false
  Dimline = (18840,5750,0)
  Direction = (0,0,0)
  Distance = 1780
  End = (19123,6037,0)
  Normal = (0,0,1)
  Start = (17343,6037,0)
  expr: End.x = Rectangle023.Placement.Base.x
  expr: Start.x = Rectangle007.Placement.Base.x + Rectangle007.Length
FEATURE [App::DocumentObjectGroup] Group004  label="dim_piso1_div"
  Group = -> [Dimension,Dimension033,Dimension034,Dimension035,Dimension036,Dimension037,Dimension038,Dimension039,Dimension040,Dimension041,Dimension042,Dimension043]
FEATURE [App::FeaturePython] InternalObjectName065  label="luz_8in_props014"  # WARN: FeaturePython — macro-defined, semantics opaque (R4)
  altura_desde_piso = 0
  fuente = 0x324bf51e3ef5d4e0f3fe3b1eeba68c0344bf68769c3a0983c5ffaed9b3cb489a302b4d803ea4e73a8b5257f138b90adbb94e8408ade3e9cefe988441e3d20777
  id_pieza_electronica = 0xdfcea24428ed9b672d74a6679325cc9712040a8c9ca1538bd6dcb8e0b5ae4f3746b69f01af7ed5ded724fabe0f87ef106629480a0bd2878843b3b2e71c31d0b2
  nombre_propiedad_exportable = luz_propiedades
  potencia_w = 18
  rotulo_dibujo_tecnico = 18
  tipo_luz = Led
  voltaje_max_v = 130
  voltaje_min_v = 95
  voltaje_nominal_v = 110
FEATURE [App::FeaturePython] InternalObjectName023  label="tc_props021"  # WARN: FeaturePython — macro-defined, semantics opaque (R4)
  altura_desde_piso = 330
  cantidad_puertos = 2
  corriente_max_a = 15
  estado = L, N, G.
  id_fuente = 0x3c00a0776292d81da5cab8f4e0a17d6922922c1ca44b7d4c051b9220bb000d42fc4de96eade343ada9251ab457f0ffa4473dfd25134b08224456cb32e5e189ec
  id_pieza_electronica = 0x259d4ba09154a6b384bddcba824761cd41797cd3b603b4362ef9b731a17e5207b063e919fd59e8cd2c5f13e10eac8d1b74550ec9d431fa63503fd6717dee961f
  nombre_propiedad_exportable = tomacorriente_propiedades
  num_circuito = A4
  num_tablero_distribucion = 1
  rotulo_dibujo_tecnico = 27
  tipo = NEMA 5-15R
  voltaje_max_v = 125
FEATURE [App::FeaturePython] InternalObjectName030  label="tc_props028"  # WARN: FeaturePython — macro-defined, semantics opaque (R4)
  altura_desde_piso = 1460
  cantidad_puertos = 2
  corriente_max_a = 15
  estado = L, N, G.
  id_fuente = 0x73a4b3db56ee835767c67a50425c5e21375cce61da5aef2f4603d8ea07821065ec3c926877f9e3d17d10e0ed00aa981fcc27da7c3e5ed3006a4049348e066c5b
  id_pieza_electronica = 0x34017a964dd063bd4afca7906514bbb7154da9e5d3d0bd2268f8b05fdffe8d2c16de739ed46d540ee41af1fd45a48212936d1863e275932b1058c65dc9f147e0
  nombre_propiedad_exportable = tomacorriente_propiedades
  num_circuito = A4
  num_tablero_distribucion = 1
  rotulo_dibujo_tecnico = 28
  tipo = NEMA 5-15R
  voltaje_max_v = 125
FEATURE [App::FeaturePython] InternalObjectName025  label="tc_props023"  # WARN: FeaturePython — macro-defined, semantics opaque (R4)
  altura_desde_piso = 1450
  cantidad_puertos = 2
  corriente_max_a = 15
  estado = L, N, G.
  id_fuente = 0x8a1dcc3e29fa7c48a88239e3575d2b8ca99f1b4c346697787a56b30526787e403d24790a6612aeb908b3d8d437b2a964eec31d336fad53fa65b6d299f8b38be3
  id_pieza_electronica = 0x49a38a2968f64d856d5fd7524ec53f5f86da1ae080d350117085e13b9e42fbed5b5aef93f5f26757ccbf94e7c4ab9a5a37e196aa4a1ed51693e13e6d87f8b705
  nombre_propiedad_exportable = tomacorriente_propiedades
  num_circuito = A5
  num_tablero_distribucion = 1
  rotulo_dibujo_tecnico = 29
  tipo = NEMA 5-15R
  voltaje_max_v = 125
FEATURE [App::FeaturePython] InternalObjectName034  label="tc_props032"  # WARN: FeaturePython — macro-defined, semantics opaque (R4)
  altura_desde_piso = 330
  cantidad_puertos = 2
  corriente_max_a = 15
  estado = L, N, G.
  id_fuente = 0xdcd0f227c349705158e018758dc05623024dc27524540a34d65e0523d7e3c2f85bd8968ff5dc051573f3e386d5ce708dca2b7ee5c868e9c6978b9168ad386219
  id_pieza_electronica = 0xa78ebe09f65c93a7059c98f675d735b2a7f3e51df4dada2e004eb025effb4abd04c7d8dbfad163c45ded0924ae8b613840f7f41ce1449bfb8ae23a507682b259
  nombre_propiedad_exportable = tomacorriente_propiedades
  num_circuito = A5
  num_tablero_distribucion = 1
  rotulo_dibujo_tecnico = 30
  tipo = NEMA 5-15R
  voltaje_max_v = 125
FEATURE [App::FeaturePython] InternalObjectName101  label="cbk_propiedades010"  # WARN: FeaturePython — macro-defined, semantics opaque (R4)
  corriente_max_a = 20
  id_fuente = 0x27294f90193d014635c04ea591c2a96fdfe65c3c986f27f233f19e31e30b65147e58e37c77dbef785a3502e786fb3c284dd2fc1fa59e2e4cb1ade3b4afdb1344
  id_pieza_electronica = 0xa76a2c54644282cfb5bc0e8adf21923dccec8ed1752c1dce9843cfdf3d49fff344dca86f855909a63e33101d2d7046bbb69d4446fbd81ca53cd143abf86d9534
  nombre_propiedad_exportable = disyuntor_propiedades
  num_circuito = B14
  num_tablero_distribucion = 1
  voltaje_max_v = 240
FEATURE [App::FeaturePython] InternalObjectName048  label="luz_8in_props002"  # WARN: FeaturePython — macro-defined, semantics opaque (R4)
  altura_desde_piso = 0
  id_pieza_electronica = 0xaa4b80f4ac73126ddf5cc19aee38e02b20a7f41e4b70bb08e2ada3dd82ffcf7c5c33c13012bf6d0a84d6c736ac07b88af273e35ef80d750b32796fdca822ab5f
  nombre_propiedad_exportable = luz_propiedades
  potencia_w = 18
  rotulo_dibujo_tecnico = 19
  tipo_luz = Led
  voltaje_max_v = 130
  voltaje_min_v = 95
  voltaje_nominal_v = 110
FEATURE [App::FeaturePython] InternalObjectName049  label="luz_8in_props003"  # WARN: FeaturePython — macro-defined, semantics opaque (R4)
  altura_desde_piso = 0
  id_pieza_electronica = 0xe2b3b845620f4e17e36eecbd08209db9f34c1fad5866b6adacb72eb28fe79f245d2745cc4a373e5a9ac0f6d67a07ff90b2fffb4692ae409bbd21ea0217750d98
  nombre_propiedad_exportable = luz_propiedades
  potencia_w = 18
  rotulo_dibujo_tecnico = 20
  tipo_luz = Led
  voltaje_max_v = 130
  voltaje_min_v = 95
  voltaje_nominal_v = 110
FEATURE [App::Part] Part190  label="luz_8in__003"
  Group = -> [InternalObjectName049,Part189,ShapeString018]
  Origin = -> Origin189
  Placement = pos=(2330,5040,0) rot=(0,0,1;0.785398rad)
  expr: Placement.Base.y = Rectangle002.Placement.Base.y + Rectangle002.Height + 339cm
  expr: Placement.Base.x = Rectangle.Placement.Base.x + 233cm
FEATURE [App::FeaturePython] InternalObjectName109  label="cbk_propiedades018"  # WARN: FeaturePython — macro-defined, semantics opaque (R4)
  corriente_max_a = 10
  id_fuente = 0xdc2c9400ceea300459fc0bbc2f3e61302184d4b722518312a9116abfacd82265b808c3d333ef6add3efbda8760545a7bc2ca4ab06f531230690979a2c221e8df
  id_pieza_electronica = 0x8fd4618657afe198802cb51414a7e8b5661496891a25216d049ac32d0fcb0d86816e8f1be82fcfeeea9d1f32389161b6078263275e478dc764febf1130b775a1
  nombre_propiedad_exportable = disyuntor_propiedades
  num_circuito = A6
  num_tablero_distribucion = 1
  voltaje_max_v = 240
FEATURE [App::FeaturePython] InternalObjectName099  label="cbk_propiedades008"  # WARN: FeaturePython — macro-defined, semantics opaque (R4)
  corriente_max_a = 20
  id_fuente = 0xa9a77dd1f92524feba5814ac2fbf7f8be872f02a4be909fba4d82ae49fa48e6825a9a2c6b30459faa4f7f5107a7b4ea6a81f55e6ed1ad09d8de6ba31292843ee
  id_pieza_electronica = 0x6b16f1f55fa6522ae2888149b520fb1de3839c7b5f8e8bdf3d1eaa6798104089b679f53bd883bbca1cc833408a0c0afc5c7792e7f59a9815aea15c204f2ba2e4
  nombre_propiedad_exportable = disyuntor_propiedades
  num_circuito = B12
  num_tablero_distribucion = 1
  voltaje_max_v = 240
FEATURE [App::FeaturePython] InternalObjectName106  label="cbk_propiedades015"  # WARN: FeaturePython — macro-defined, semantics opaque (R4)
  corriente_max_a = 10
  id_fuente = 0x3e1bffc4e85c7e6d3b0a7aca413956e50e523939b968639bff40170567262aeac32b1faca6131eebe102c215ce97a4e97aa0ed493f2c6df2555748fa3c39990d
  id_pieza_electronica = 0xe5455cb033194872e6d72824b953fa416e347642384497a082d9ad1448a07c75af65562f6eaf1b263b1efa8e62d0fc8d501f2bfeb8aa1597e150da51317a32d0
  nombre_propiedad_exportable = disyuntor_propiedades
  num_circuito = A3
  num_tablero_distribucion = 1
  voltaje_max_v = 240
FEATURE [App::FeaturePython] InternalObjectName095  label="cbk_propiedades004"  # WARN: FeaturePython — macro-defined, semantics opaque (R4)
  corriente_max_a = 20
  id_fuente = 0x178bc69bbf2285e322ca909c3247dffb26130b5d0d07d2c6627075581541f101ce48f6f14b134468dc0d8e1b17852ff06023b1322b39651a4cd7a58ca1f4b8b0
  id_pieza_electronica = 0xc93d7b6cef5bad231111f9e78e996d2b81be50f04041ebe7aa0d0b8cb32211b0f6e7d07d6734414d622e9d95493f322be1419c65e1ba858c87dfc440f878378a
  nombre_propiedad_exportable = disyuntor_propiedades
  num_circuito = B7
  num_tablero_distribucion = 1
  voltaje_max_v = 240
FEATURE [App::FeaturePython] InternalObjectName050  label="luz_60x60_props"  # WARN: FeaturePython — macro-defined, semantics opaque (R4)
  altura_desde_piso = 0
  id_pieza_electronica = 0x165428dd9ab5cafd0e3293b8546c01314fd58ffac1e9f85f85fe9a783c74b2bce08111f96193331006740e303f714a7b69acf8468cbcaed41265877a79cc3593
  nombre_propiedad_exportable = luz_propiedades
  potencia_w = 0
  rotulo_dibujo_tecnico = 21
  voltaje_max_v = 130
  voltaje_min_v = 95
  voltaje_nominal_v = 110
FEATURE [App::FeaturePython] InternalObjectName114  label="cbk2_propiedades002"  # WARN: FeaturePython — macro-defined, semantics opaque (R4)
  corriente_max_a = 30
  id_fuente_polo1 = 0xd4d80834d1a795b1360f173edac4b983cfdc9000df524021d992745a8307e2cfe1f2f10f4724b435301d14beee14db63c4488a32840234cad267c59a36da312d
  id_fuente_polo2 = 0x32686a20a51c87b172ba3198303d1647aa673f41f2bae0ac72c80bdcf32a85a8cbf61019c902845f3aae3b71bbcd0b0dc4acfbb1e762b637ccd0c33fc12dd44d
  id_pieza_electronica = 0x820253bfeab3acd8f8303dfd13177940833d7a917cf816230fdf7313cda440536a23f015a101963f969bd2f8aa27dfb297f004e99348b3ac5a6b6d324205fd8
  nombre_propiedad_exportable = disyuntor2_propiedades
  num_circuito_polo1 = A13
  num_circuito_polo2 = A14
  num_tablero_distribucion = 1
  voltaje_max_v = 240
FEATURE [App::FeaturePython] InternalObjectName096  label="cbk_propiedades005"  # WARN: FeaturePython — macro-defined, semantics opaque (R4)
  corriente_max_a = 20
  id_fuente = 0xd83da0b5fcfc5403499050e69312e104d9319948fde5f10ed8d10f05b125de48b3cdc323a086e839701be18dcb8b7ab118495ce323847dc0d5b4554812b179b3
  id_pieza_electronica = 0xdff1eb74c0f05d50bc49926fc36c41d8b52e1d8f2cd7a51a9f961907706785b58f114ada5d4ff48a592fbc3201d877f77326cf82fea32b6227af569d5ab79f68
  nombre_propiedad_exportable = disyuntor_propiedades
  num_circuito = B9
  num_tablero_distribucion = 1
  voltaje_max_v = 240
FEATURE [App::FeaturePython] InternalObjectName102  label="cbk_propiedades011"  # WARN: FeaturePython — macro-defined, semantics opaque (R4)
  corriente_max_a = 20
  id_fuente = 0xc3bffb5c95566877bd76eaa02eba8418ce475a4040a120fe713e42c981b544278a8c278c818fdf3780b3222a9cb90e0e0cf38b04783b47ade46b9603e1763c21
  id_pieza_electronica = 0xf1f43acca193a4ad707a631ec4b20ab90792214504c5252e29846e88489cf47e4d891958e49aeade9c14a8b682a03ab1f2929981267cf1493a84714838f02ffd
  nombre_propiedad_exportable = disyuntor_propiedades
  num_circuito = B15
  num_tablero_distribucion = 1
  voltaje_max_v = 240
FEATURE [App::FeaturePython] InternalObjectName097  label="cbk_propiedades006"  # WARN: FeaturePython — macro-defined, semantics opaque (R4)
  corriente_max_a = 20
  id_fuente = 0xb61717ccb59cff8d1431799d961dbfd3f1ca7e863d5be129a818c7d354a11b85e1486f914bc702a56b0bdddea1f37104f92d665d0d755b44f4dd1cb02b87c908
  id_pieza_electronica = 0xde36751806653536a3a0d696307b421c6e8af64b93f3a1b4526cf812a51184ab08939e93648bf3c8ba165d2c851669ad6ffbcf3cb9ca7b146b2748bfd1b194cd
  nombre_propiedad_exportable = disyuntor_propiedades
  num_circuito = B10
  num_tablero_distribucion = 1
  voltaje_max_v = 240
FEATURE [App::FeaturePython] InternalObjectName115  label="cbk2_propiedades003"  # WARN: FeaturePython — macro-defined, semantics opaque (R4)
  corriente_max_a = 30
  id_fuente_polo1 = 0x81b49181a829d0c338b14a3764c65e4cae71b44b6fdcbb2b9cc488f9475155d85fa9eb96f6702f05df47a8f28effe1854aed298196c9802814a516c1c97140f4
  id_fuente_polo2 = 0xe0fc066be1fc9ee6a258c2b089cd0c17a42c59a0776def932afcec8468ba4327fc554b63a88610923b2689c741448fc7feab0eb3f7429b189688ee5ebad618ba
  id_pieza_electronica = 0xa9ac2973da61cf9d2bf01965138c505b1d47b41c266546f65ba688468f9a2323aa9435cbf7eb474db91f9920a8bd2295a9eb3350e944a1fcc75bc32f4276dae8
  nombre_propiedad_exportable = disyuntor2_propiedades
  num_circuito_polo1 = A15
  num_circuito_polo2 = A16
  num_tablero_distribucion = 1
  voltaje_max_v = 240
FEATURE [App::FeaturePython] InternalObjectName110  label="cbk_propiedades019"  # WARN: FeaturePython — macro-defined, semantics opaque (R4)
  corriente_max_a = 10
  id_fuente = 0x1737b04c9f544aad42719ee9cbaa8cf3a899acb5285a1aa41459e4d4d96d0fc5bffa1ee0cfa3e3ca4874a51eb7c949020915ba5f610f88ed93b7d2715611361a
  id_pieza_electronica = 0x7a086f683ec6db7a092a7ca5c6a47649f461a0a72e6a29bc18866e2ddc32d0f89e15937ff3072c8d691a38b374d126f3317188cd56966868c08bbf21ea87c140
  nombre_propiedad_exportable = disyuntor_propiedades
  num_circuito = A7
  num_tablero_distribucion = 1
  voltaje_max_v = 240
FEATURE [App::FeaturePython] InternalObjectName047  label="luz_8in_props001"  # WARN: FeaturePython — macro-defined, semantics opaque (R4)
  altura_desde_piso = 0
  id_pieza_electronica = 0x8eceb58fc409f117b4640a662594d64559c1b62f57fc33b03e27c7e661c0da6441494c4ec05179e0781cf6fa713aa878ece3c4a193ee675b3c0270060ad7ac86
  nombre_propiedad_exportable = luz_propiedades
  potencia_w = 18
  rotulo_dibujo_tecnico = 22
  tipo_luz = Led
  voltaje_max_v = 130
  voltaje_min_v = 95
  voltaje_nominal_v = 110
FEATURE [App::FeaturePython] InternalObjectName108  label="cbk_propiedades017"  # WARN: FeaturePython — macro-defined, semantics opaque (R4)
  corriente_max_a = 10
  id_fuente = 0x1b8d3d24cb9c25610dbf13c16406f83eb168fefacaab2a1851a88911f67ddcb33d1e812987dafbd9cf6efac8df656a96d4ef239b093d608bfce4f475b3e7e4f5
  id_pieza_electronica = 0x8632bd938c22cc79e0e78515a6cf626c4c3f517355b50a1ebce801a7b808101b1058fe238d446c8125e6e694e07962282c9b1be806f172773776680284c9e201
  nombre_propiedad_exportable = disyuntor_propiedades
  num_circuito = A5
  num_tablero_distribucion = 1
  voltaje_max_v = 240
FEATURE [App::FeaturePython] InternalObjectName113  label="cbk2_propiedades001"  # WARN: FeaturePython — macro-defined, semantics opaque (R4)
  corriente_max_a = 30
  id_fuente_polo1 = 0x880af842e503cafa2ad5e7242a8156e49bbf456ff04269fea7dab06e7d9c2f2d8bdfa68350a357262fbbef40b40d678a6ef31277012ebc70107847ffaffe285
  id_fuente_polo2 = 0x248e07292ddeb9cbb491720d539fd115ce41a68089789ce3ad49bbaf7e9e88993d3ad74d43da17e99dcc1f06618791d9899cd3eb93540b62af699bc632a6e3bc
  id_pieza_electronica = 0xc0cacf327b53a50560027bcfed865d7732c996ed08b4f0487b117441b20dc7d899442375c8a0bc07685517f21a59918e474187882402e7294b7860f85880fe00
  nombre_propiedad_exportable = disyuntor2_propiedades
  num_circuito_polo1 = A11
  num_circuito_polo2 = A12
  num_tablero_distribucion = 1
  voltaje_max_v = 240
FEATURE [App::FeaturePython] InternalObjectName051  label="luz_60x60_props001"  # WARN: FeaturePython — macro-defined, semantics opaque (R4)
  altura_desde_piso = 0
  id_pieza_electronica = 0x4ec1a6cb89f15bc64418ce53d63b2d34dea636dc71435fecf858ef5eba671358a988247c2009f979f484e788202ba9ebb53e74ec4255c319b584a844848f46c2
  nombre_propiedad_exportable = luz_propiedades
  potencia_w = 0
  rotulo_dibujo_tecnico = 23
  voltaje_max_v = 130
  voltaje_min_v = 95
  voltaje_nominal_v = 110
FEATURE [App::FeaturePython] InternalObjectName111  label="cbk_propiedades020"  # WARN: FeaturePython — macro-defined, semantics opaque (R4)
  corriente_max_a = 10
  id_fuente = 0xa6c0e23f74b4f600a0e99a9452e376d053a1706a74673c33f95801a7954969fab2cf7b5e3d0e9e27ab940a7947e466641ff17125f8c40a11bccf56d45d1ced47
  id_pieza_electronica = 0x5023a6c4803e6b3ff4436713d6002f3213880d0b252c0fd61500ea4e001f8c4ce9cee77ada6e3f03a1d5cbdc40a54a6778b2ebb951e053c7ad7dcc64e9c032e5
  nombre_propiedad_exportable = disyuntor_propiedades
  num_circuito = A8
  num_tablero_distribucion = 1
  voltaje_max_v = 240
FEATURE [App::FeaturePython] InternalObjectName112  label="cbk2_propiedades"  # WARN: FeaturePython — macro-defined, semantics opaque (R4)
  corriente_max_a = 30
  id_fuente_polo1 = 0x2717c838997e670334477659d68e9f3acb5bdae1a56b617ffb349e56db5947d4ce21a7ae33f6e319cb57227552cabe4c2c14b2d858602aa68e7d35bedf5a4b6c
  id_fuente_polo2 = 0x57f80e2886f9d6363eed0b7fb81e9ce7272b1fdb89ada728a4c8ab8925fd57ccd4759a881ae725e1360e97d9770e06358c0ca4f6453912ba1263c831bb0fb8db
  id_pieza_electronica = 0x60449310fc24e632d167ec2968a3b84ac024f515ab8456bb26296fe238b5df957289da2a2cc28639881c59256958b9ca8d98569fb4f9d368d94e46e9f00f2b1f
  nombre_propiedad_exportable = disyuntor2_propiedades
  num_circuito_polo1 = A9
  num_circuito_polo2 = A10
  num_tablero_distribucion = 1
  voltaje_max_v = 240
FEATURE [App::FeaturePython] InternalObjectName104  label="cbk_propiedades013"  # WARN: FeaturePython — macro-defined, semantics opaque (R4)
  corriente_max_a = 10
  id_fuente = 0x259d67b3b3f0d6580eca533897155e5ea2e965de68a868bc3e8ce93daef8426fb094e85b86cc8386af3762ae01c32767658998477d6358bcebad6a6490f82106
  id_pieza_electronica = 0xdb8332d752c9e48281371f3542bf60758c345c79033a8b5343afcda2690fc1f76f7be309f16a0fd1c0ec358a0892060be21c3aedbed4e5f636ea5e5f72bb717d
  nombre_propiedad_exportable = disyuntor_propiedades
  num_circuito = A1
  num_tablero_distribucion = 1
  voltaje_max_v = 240
FEATURE [App::FeaturePython] InternalObjectName116  label="cbk2_propiedades004"  # WARN: FeaturePython — macro-defined, semantics opaque (R4)
  corriente_max_a = 30
  id_fuente_polo1 = 0x66adeb836b8c3b17b30a247274fd7e3d65c850cc170c8f80294f6536be4bcd3317d98fce48e6ea147c15d25b0408453e10ef1a222568bed24ca985a39ddc98ea
  id_fuente_polo2 = 0x536f7a78430960068564f81233f67170859e8cf842443ece3869579d92d8b6ab005a3341e565de111a017b619208f48be20f09cf168e0abbaf5b49ddbda73133
  id_pieza_electronica = 0x6c5564b398258bfd426f055596ec26918b52cc7357d38cb88b0e70524e9ab509bb4cf3bdf4ae40785c7a56759683c41d5985470470a69150cccd8ba7b568ffb8
  nombre_propiedad_exportable = disyuntor2_propiedades
  num_circuito_polo1 = A17
  num_circuito_polo2 = A18
  num_tablero_distribucion = 1
  voltaje_max_v = 240
FEATURE [App::FeaturePython] InternalObjectName100  label="cbk_propiedades009"  # WARN: FeaturePython — macro-defined, semantics opaque (R4)
  corriente_max_a = 20
  id_fuente = 0xb8eb1c8bfae92ccfd1bafc5d9759b03895172c8ecc605e62a24d5100758021c1876595ac29a3582ed1fc07b859233d2abc1b45690b6c1ac7cb01c67fefc65204
  id_pieza_electronica = 0xc797bcfb84c239412433a1350c82c02759b7af6aa0002f7fbd50976d0c4d9809200b9bbb2fc4d3d268b93c36e7ed98db837fea277e1eed4d4c466fb85ffdf13
  nombre_propiedad_exportable = disyuntor_propiedades
  num_circuito = B13
  num_tablero_distribucion = 1
  voltaje_max_v = 240
FEATURE [App::FeaturePython] InternalObjectName041  label="i1_propiedades006"  # WARN: FeaturePython — macro-defined, semantics opaque (R4)
  altura_desde_piso = 0
  corriente_max_a = 10
  id_fuente = 0xe278294e5fd594ca5bf1db021ee32b4f9714d6e66f847416ed29239ba0d5edb499c2a05fb43f4d3d2588dbcc4f87afd6fc02970743af0882acb5c9efd440cf89
  id_pieza_electronica = 0x8f9993d40f814ac8235d4bc800df7f5ecd1d522dc2326359b0f802cb1c76249a15ce110fa4b65712e2404b06110a95b0a731db3b2c56327cb3333bbb3eede8d6
  nombre_propiedad_exportable = interruptor_propiedades
  rotulo_dibujo_tecnico = 6
  tipo_interruptor = Ordinario sencillo
  voltaje_max_v = 250
FEATURE [App::FeaturePython] InternalObjectName042  label="i1_propiedades007"  # WARN: FeaturePython — macro-defined, semantics opaque (R4)
  altura_desde_piso = 0
  corriente_max_a = 10
  id_fuente = 0x3f58199353572579cb4edf0d783a01fe4952d764e93c7abe8f9dd57f115134142b8936b760b40752c463bc1ec981e6385621361a064444e71a59002ca4ecffcd
  id_pieza_electronica = 0x34900d09b8fb9279194c77bfb14e7abe39a2c70ac5a69efc1413fcb5928ff09f820edf6e5ad15f0350d463387514aa63c42ceba5fc9b628e33040f37cea7b124
  nombre_propiedad_exportable = interruptor_propiedades
  rotulo_dibujo_tecnico = 7
  tipo_interruptor = Ordinario sencillo
  voltaje_max_v = 250
FEATURE [App::FeaturePython] InternalObjectName107  label="cbk_propiedades016"  # WARN: FeaturePython — macro-defined, semantics opaque (R4)
  corriente_max_a = 10
  id_fuente = 0xe826a53abd9c5b464145e8423820204017ddb96200dbda0e28b314f9be76f14d0c6e10cbaf16d2795310a2d745dab5d41402b0e3afb15a4d83faf7f8831998b8
  id_pieza_electronica = 0xa8fb9d798b357577050efc6767add72abc1c851cf4a09a85961995949ad26bba7d74a2925e82ed4ae61ad1b70371f25449781fb4ae034610c0c67e1967da47e3
  nombre_propiedad_exportable = disyuntor_propiedades
  num_circuito = A4
  num_tablero_distribucion = 1
  voltaje_max_v = 240
FEATURE [App::FeaturePython] InternalObjectName103  label="cbk_propiedades012"  # WARN: FeaturePython — macro-defined, semantics opaque (R4)
  corriente_max_a = 20
  id_fuente = 0x1b978a44dcb72fdcb74f8a6e37d7825d4dfbf8b52fe6b1ede3759aa70a9848cfa62795024085ad6e3a8b4d9758547fb35ed8f437ebfb19837bcca222b8cf7e6f
  id_pieza_electronica = 0xadfc4f1158a92daf17f0adac030a7ee0331369cdcf3bc56506023295252bb05a2778b4efb989e7c3e609da973ebe91f7ad83dc654f71539e0238af0d8c719855
  nombre_propiedad_exportable = disyuntor_propiedades
  num_circuito = B16
  num_tablero_distribucion = 1
  voltaje_max_v = 240
FEATURE [App::FeaturePython] InternalObjectName098  label="cbk_propiedades007"  # WARN: FeaturePython — macro-defined, semantics opaque (R4)
  corriente_max_a = 20
  id_fuente = 0x495358514e10ac99aeca343bbe1313f7be11651fab91a9af974ddcb45922c56f7002d5d38e7263d6ee366affd4129691818f7faa4a877b0c453f2a0011f2523
  id_pieza_electronica = 0x8bd1af9cf3d6fd36c4a3b20bcc786bca6af8c40952b03272e9916f4d3c3d14d88b9b6544ef28b8da1a2807ea72c48852d94ab769200999714a9f16305f292270
  nombre_propiedad_exportable = disyuntor_propiedades
  num_circuito = B11
  num_tablero_distribucion = 1
  voltaje_max_v = 240
FEATURE [App::FeaturePython] InternalObjectName105  label="cbk_propiedades014"  # WARN: FeaturePython — macro-defined, semantics opaque (R4)
  corriente_max_a = 10
  id_fuente = 0x4a8341e1cac148c7a63cdc3a0c9155171862dcd18a29a6bd917ce0ccc4a66bd926f81b5e2446978894ce72f928dfdce4f706b96c73c1e41d05d41e60636a201a
  id_pieza_electronica = 0xa9ce3300848357d433071196d32696031371cabdce269c73f445ef5b622ca519eaf59c051808792ec018c97eec2d7d61dbb9b1fff5ae53b559c7c05aa05af429
  nombre_propiedad_exportable = disyuntor_propiedades
  num_circuito = A2
  num_tablero_distribucion = 1
  voltaje_max_v = 240
FEATURE [App::FeaturePython] InternalObjectName062  label="luz_8in_props011"  # WARN: FeaturePython — macro-defined, semantics opaque (R4)
  altura_desde_piso = 0
  fuente = 0x3f58199353572579cb4edf0d783a01fe4952d764e93c7abe8f9dd57f115134142b8936b760b40752c463bc1ec981e6385621361a064444e71a59002ca4ecffcd
  id_pieza_electronica = 0x1a1f5fd6fda22ba7b3702195fdb47f303620717d21f7fb9e8a1926aee7c41de86994efa4f016c9475d2df5b6c7e328a63685e5e5c6f629caa61aabbd9d040383
  nombre_propiedad_exportable = luz_propiedades
  potencia_w = 18
  rotulo_dibujo_tecnico = 24
  tipo_luz = Led
  voltaje_max_v = 130
  voltaje_min_v = 95
  voltaje_nominal_v = 110
FEATURE [App::FeaturePython] InternalObjectName072  label="luz_8in_props021"  # WARN: FeaturePython — macro-defined, semantics opaque (R4)
  altura_desde_piso = 0
  fuente = 0xef58752039e4a8f0acecb384f0379304976ef84bd278df85f9b58796f06915d30a1e06d9f628ea5e7d7381c4c95167e2dcd6510dd05e7b11c94ed1ffee9fd841
  id_pieza_electronica = 0xb019d177801a49bd4a749b72393295e58661d94981609144b3f112bfb5dcef1fa3cc7230a57789adca3b9ba4f916e8a0ccf9bcc0634540936faa47d4ac8cb21b
  nombre_propiedad_exportable = luz_propiedades
  potencia_w = 18
  rotulo_dibujo_tecnico = 25
  tipo_luz = Led
  voltaje_max_v = 130
  voltaje_min_v = 95
  voltaje_nominal_v = 110
FEATURE [App::FeaturePython] InternalObjectName070  label="luz_8in_props019"  # WARN: FeaturePython — macro-defined, semantics opaque (R4)
  altura_desde_piso = 0
  fuente = 0xe278294e5fd594ca5bf1db021ee32b4f9714d6e66f847416ed29239ba0d5edb499c2a05fb43f4d3d2588dbcc4f87afd6fc02970743af0882acb5c9efd440cf89
  id_pieza_electronica = 0x8c22128c8667199233f10d708df0574ded4139a0c94601653d4458549c77d1e725b55753360a57d248ada8602acd589337b683f691929a18d1fd2bd7eca01a88
  nombre_propiedad_exportable = luz_propiedades
  potencia_w = 18
  rotulo_dibujo_tecnico = 26
  tipo_luz = Led
  voltaje_max_v = 130
  voltaje_min_v = 95
  voltaje_nominal_v = 110
FEATURE [App::FeaturePython] InternalObjectName066  label="luz_8in_props015"  # WARN: FeaturePython — macro-defined, semantics opaque (R4)
  altura_desde_piso = 0
  fuente = 0x324bf51e3ef5d4e0f3fe3b1eeba68c0344bf68769c3a0983c5ffaed9b3cb489a302b4d803ea4e73a8b5257f138b90adbb94e8408ade3e9cefe988441e3d20777
  id_pieza_electronica = 0xc8e187b3645f87fea3f0795ecfb3f8c6ae993948fdb3af7959a38c29e2e219d98c8a16a65fcdca991c857318b3748b8541c8bd1fab33904548d531a005f6e684
  nombre_propiedad_exportable = luz_propiedades
  potencia_w = 18
  rotulo_dibujo_tecnico = 27
  tipo_luz = Led
  voltaje_max_v = 130
  voltaje_min_v = 95
  voltaje_nominal_v = 110
FEATURE [App::FeaturePython] InternalObjectName063  label="luz_8in_props012"  # WARN: FeaturePython — macro-defined, semantics opaque (R4)
  altura_desde_piso = 0
  fuente = 0x3f58199353572579cb4edf0d783a01fe4952d764e93c7abe8f9dd57f115134142b8936b760b40752c463bc1ec981e6385621361a064444e71a59002ca4ecffcd
  id_pieza_electronica = 0x66b9c3b81827d9175ab9f1c6a62c3e1f9169e239ed8521cf42dfad32e56b8678c5165663c4663e4bd202802c1771b63b68114eb04cd5207a6ce005c1d78b4ba5
  nombre_propiedad_exportable = luz_propiedades
  potencia_w = 18
  rotulo_dibujo_tecnico = 28
  tipo_luz = Led
  voltaje_max_v = 130
  voltaje_min_v = 95
  voltaje_nominal_v = 110
FEATURE [App::FeaturePython] InternalObjectName068  label="luz_8in_props017"  # WARN: FeaturePython — macro-defined, semantics opaque (R4)
  altura_desde_piso = 0
  fuente = 0xe278294e5fd594ca5bf1db021ee32b4f9714d6e66f847416ed29239ba0d5edb499c2a05fb43f4d3d2588dbcc4f87afd6fc02970743af0882acb5c9efd440cf89
  id_pieza_electronica = 0xeb5a3238681a338c5badd48159a42692b85b4be5039c34b9ed203ae6a1ec14e7392acd44734ace74859d48c0b1adb5f87cc3895e6cb688f2475e40190ce65b91
  nombre_propiedad_exportable = luz_propiedades
  potencia_w = 18
  rotulo_dibujo_tecnico = 29
  tipo_luz = Led
  voltaje_max_v = 130
  voltaje_min_v = 95
  voltaje_nominal_v = 110
FEATURE [App::FeaturePython] Dimension021  # Draft dimension (typed FeaturePython)
  Diameter = false
  Dimline = (15473,831.5,0)
  Direction = (0,0,0)
  Distance = 2110
  End = (15873,2110,0)
  Normal = (0,0,1)
  Start = (15873,0,0)
  expr: Dimline.x = Rectangle008.Placement.Base.x - 0.4m
  expr: End.y = Rectangle008.Placement.Base.y + Rectangle008.Height
  expr: Start.y = Rectangle008.Placement.Base.y
FEATURE [App::FeaturePython] Text004  # WARN: FeaturePython — macro-defined, semantics opaque (R4)
  Placement = pos=(100,0,0) rot=(0,0,1;0rad)
  Text = x3
FEATURE [App::DocumentObjectGroup] Group016  label="interruptor_gen003"
  Group = -> [Line130,Text004,Circle064]
FEATURE [App::FeaturePython] Dimension009  # Draft dimension (typed FeaturePython)
  Diameter = false
  Dimline = (10010,3900,0)
  Direction = (0,0,0)
  Distance = 1000
  End = (9657,3560,0)
  Normal = (0,0,1)
  Start = (9657,4560,0)
  expr: Dimline.x = Rectangle004.Placement.Base.x + Rectangle004.Length + 0.4m
  expr: Start.y = Rectangle004.Placement.Base.y + Rectangle004.Height
  expr: End.y = Rectangle004.Placement.Base.y
FEATURE [App::FeaturePython] InternalObjectName060  label="luz_8in_props009"  # WARN: FeaturePython — macro-defined, semantics opaque (R4)
  altura_desde_piso = 0
  fuente = 0x55876f5196a1cfafdc1a24a0ed5cce5b592f0984a4dac79d6670435344794837f9f85b65072aa5fab7988351a30da20644ba8dd4323cb0aa3a3fdc18d423a51f
  id_pieza_electronica = 0x2f414f9e6d2b72f146f36eb2336759bed212e80d9c434103fe5bb93f6148061fe19bac46caef6fb02a55f4e52c08fadb6aeb1d01ccf971516346c3bc9c369259
  nombre_propiedad_exportable = luz_propiedades
  potencia_w = 18
  rotulo_dibujo_tecnico = 30
  tipo_luz = Led
  voltaje_max_v = 130
  voltaje_min_v = 95
  voltaje_nominal_v = 110
FEATURE [App::FeaturePython] Dimension024  # Draft dimension (typed FeaturePython)
  Diameter = false
  Dimline = (23303.5,1031.5,0)
  Direction = (0,0,0)
  Distance = 6037
  End = (22250,0,0)
  Normal = (0,0,1)
  Start = (22250,6037,0)
FEATURE [App::FeaturePython] Dimension027  # Draft dimension (typed FeaturePython)
  Diameter = false
  Dimline = (2800,500,0)
  Direction = (0,0,0)
  Distance = 1650
  End = (2400,1650,0)
  Normal = (0,0,1)
  Start = (2400,0,0)
  expr: Dimline.x = Rectangle002.Placement.Base.x + Rectangle002.Length + 0.4m
  expr: End.x = Rectangle002.Placement.Base.x + Rectangle002.Length
  expr: End.y = Rectangle002.Placement.Base.y + Rectangle002.Height
  expr: Start.y = Rectangle002.Placement.Base.y
  expr: Start.x = Rectangle002.Placement.Base.x + Rectangle002.Length
FEATURE [App::FeaturePython] Dimension019  # Draft dimension (typed FeaturePython)
  Diameter = false
  Dimline = (17603.5,5610,0)
  Direction = (0,0,0)
  Distance = 4430
  End = (17220,6000,0)
  Normal = (0,0,1)
  Start = (12790,6000,0)
  expr: Dimline.y = Rectangle005.Placement.Base.y + Rectangle005.Height - 0.4m
  expr: End.x = Rectangle007.Placement.Base.x
  expr: Start.x = Rectangle005.Placement.Base.x + Rectangle005.Length
FEATURE [App::FeaturePython] Dimension013  # Draft dimension (typed FeaturePython)
  Diameter = false
  Dimline = (8703.5,31.5,0)
  Direction = (0,0,0)
  Distance = 2370
  End = (8350,2370,0)
  Normal = (0,0,1)
  Start = (8350,0,0)
  expr: End.y = Rectangle006.Placement.Base.y + Rectangle006.Height
  expr: Start.y = Rectangle006.Placement.Base.y
FEATURE [App::FeaturePython] Dimension015  # Draft dimension (typed FeaturePython)
  Diameter = false
  Dimline = (9703.5,3160,0)
  Direction = (0,0,0)
  Distance = 2530
  End = (9610,3560,0)
  Normal = (0,0,1)
  Start = (7080,3560,0)
  expr: Dimline.y = Rectangle004.Placement.Base.y - 0.4m
  expr: End.x = Rectangle004.Placement.Base.x + Rectangle004.Length
  expr: Start.x = Rectangle004.Placement.Base.x
FEATURE [App::FeaturePython] Dimension029  # Draft dimension (typed FeaturePython)
  Diameter = false
  Dimline = (9000,6000,0)
  Direction = (0,0,0)
  Distance = 1197
  End = (9670,5757,0)
  Normal = (0,0,1)
  Start = (9670,4560,0)
  expr: End.y = Rectangle011.Placement.Base.y
  expr: Start.y = Rectangle004.Placement.Base.y + Rectangle004.Height
FEATURE [App::FeaturePython] InternalObjectName045  label="i1_propiedades009"  # WARN: FeaturePython — macro-defined, semantics opaque (R4)
  altura_desde_piso = 0
  corriente_max_a = 10
  id_fuente = 0xc4d097ea02880fe8f913cb2f19b1ca93169b2448f836de2ac3d3e46be4110de8539df76bd2044d4b630fef2b481b1f5acf593af844b458f1f9bd1931a4712d94
  id_pieza_electronica = 0x3fca306ab6b05292868877bc4ebf0d886519e026309183c59c4ee244d7c43d3cad9e0c7c5d05d5b5ac1709958d948255119b19fc2f9b5ec3e590bd2040b39308
  nombre_propiedad_exportable = interruptor_propiedades
  rotulo_dibujo_tecnico = 8
  tipo_interruptor = Ordinario sencillo
  voltaje_max_v = 250
FEATURE [App::FeaturePython] Dimension030  # Draft dimension (typed FeaturePython)
  Diameter = false
  Dimline = (10700,600,0)
  Direction = (0,0,0)
  Distance = 5757
  End = (10880,5757,0)
  Normal = (0,0,1)
  Start = (10880,0,0)
  expr: End.y = Rectangle011.Placement.Base.y
  expr: Start.y = Rectangle.Placement.Base.y
FEATURE [App::FeaturePython] InternalObjectName056  label="luz_8in_props005"  # WARN: FeaturePython — macro-defined, semantics opaque (R4)
  altura_desde_piso = 0
  id_pieza_electronica = 0x1d4c5481f4f85464eb16b5619993c22a651985bf5081aafcc254f1f1d31089efb86ccf75f16fbfe1a86f736545b99cbb7775722e5d7d2e6d8529d71d67c96384
  nombre_propiedad_exportable = luz_propiedades
  potencia_w = 18
  rotulo_dibujo_tecnico = 31
  tipo_luz = Led
  voltaje_max_v = 130
  voltaje_min_v = 95
  voltaje_nominal_v = 110
FEATURE [App::FeaturePython] InternalObjectName046  label="luz_8in_props"  # WARN: FeaturePython — macro-defined, semantics opaque (R4)
  altura_desde_piso = 0
  id_pieza_electronica = 0xf4c062f8b682c39f64d4bd3f6d1542b9bc87dd1a44d38d64850150aa7b04baff5f40e74cef79966381a731e0101471d2631aa9e3a8339af5c6a7602031eccdb2
  nombre_propiedad_exportable = luz_propiedades
  potencia_w = 18
  rotulo_dibujo_tecnico = 32
  tipo_luz = Led
  voltaje_max_v = 130
  voltaje_min_v = 95
  voltaje_nominal_v = 110
FEATURE [App::FeaturePython] InternalObjectName032  label="tc_props030"  # WARN: FeaturePython — macro-defined, semantics opaque (R4)
  altura_desde_piso = 330
  cantidad_puertos = 1
  corriente_max_a = 50
  estado = A, B, C. Exceso de pintura.
  id_fuente = 0x36c2d4e5fcb03326e5e69d20e236e1097a48677aefa338a0fbf1679d39c30518c42c6d011b48bfa8dd361f02bb1566565d68611c3db7771262e5b8a0bbbaf53b
  id_pieza_electronica = 0x8b2cfabd7a953005c1bd8b4468493ea4dbacabcd809db2592645d6995730ba0916ff2eea633de73d1a88deded7f057b42b724b267504cabe501d1f5577836012
  nombre_propiedad_exportable = tomacorriente_propiedades
  num_circuito = [A1, A2, A3]
  num_tablero_distribucion = 1
  rotulo_dibujo_tecnico = 31
  tipo = NEMA 10-50R
  voltaje_max_v = 250
FEATURE [App::FeaturePython] InternalObjectName071  label="luz_8in_props020"  # WARN: FeaturePython — macro-defined, semantics opaque (R4)
  altura_desde_piso = 0
  fuente = 0xedfc5bb3aa30eb8bd0709db342119f4dde92e71105b250b3161ed4f19e3a93e66b6ad4c2c072d329844ca216b74895e70a9c625ca2b1a1a934e3f21c3a35e75b
  id_pieza_electronica = 0x534dd9457f77dc3936dc84b2bcb376e19e684f5382f4a47b4a9d3359d5e19bfdf9156c4b9ed1fe6ed3371b1a1394be0b37f4db98c0ae6abeab171d1f76fbb13b
  nombre_propiedad_exportable = luz_propiedades
  potencia_w = 18
  rotulo_dibujo_tecnico = 33
  tipo_luz = Led
  voltaje_max_v = 130
  voltaje_min_v = 95
  voltaje_nominal_v = 110
FEATURE [App::Part] Part232  label="luz_8in__020"
  Group = -> [InternalObjectName071,Part233,ShapeString040]
  Origin = -> Origin232
  Placement = pos=(16713,1910,0) rot=(0,0,1;0rad)
  expr: Placement.Base.y = Rectangle025.Placement.Base.y + Rectangle025.Height + 65cm
  expr: Placement.Base.x = Rectangle008.Placement.Base.x + Rectangle008.Length + 71cm
FEATURE [App::FeaturePython] Dimension014  # Draft dimension (typed FeaturePython)
  Diameter = false
  Dimline = (7103.5,3930,0)
  Direction = (0,0,0)
  Distance = 3880
  End = (7080,4330,0)
  Normal = (0,0,1)
  Start = (3200,4330,0)
  expr: Dimline.y = Rectangle003.Placement.Base.y - 0.4m
  expr: End.x = Rectangle003.Placement.Base.x + Rectangle003.Length
  expr: Start.x = Rectangle003.Placement.Base.x
FEATURE [App::FeaturePython] InternalObjectName037  label="i1_propiedades002"  # WARN: FeaturePython — macro-defined, semantics opaque (R4)
  altura_desde_piso = 0
  corriente_max_a = 10
  id_fuente = 0x35a7edf470d588801c428d22616e45bda78260bf507dd7e3f2c5903492ea83d4db2b0a2f4f8b1fb885fb05ad8d5165b209df575b5803592ef059f0e68e445cf1
  id_pieza_electronica = 0x443f8c002ca4d2a22ad428c8a923ce54daf896ac7e6ad969b20831700e892e636d345cde942fa15f60d010f5d004f21e1f7f1059d7ffa61bbe44de5fe9f8f30d
  nombre_propiedad_exportable = interruptor_propiedades
  rotulo_dibujo_tecnico = 9
  tipo_interruptor = Ordinario sencillo
  voltaje_max_v = 250
FEATURE [App::FeaturePython] InternalObjectName061  label="luz_8in_props010"  # WARN: FeaturePython — macro-defined, semantics opaque (R4)
  altura_desde_piso = 0
  fuente = 0x324bf51e3ef5d4e0f3fe3b1eeba68c0344bf68769c3a0983c5ffaed9b3cb489a302b4d803ea4e73a8b5257f138b90adbb94e8408ade3e9cefe988441e3d20777
  id_pieza_electronica = 0xb71f3b8807e30e3940f7bbfacf98d9230e9eec93fc6e4eb2c87e38ea72b1eb0a613b49e907a5947e48900c6d84d2da75b97d38e22d7ab93e2f948f656364d38
  nombre_propiedad_exportable = luz_propiedades
  potencia_w = 18
  rotulo_dibujo_tecnico = 34
  tipo_luz = Led
  voltaje_max_v = 130
  voltaje_min_v = 95
  voltaje_nominal_v = 110
FEATURE [App::FeaturePython] Dimension020  # Draft dimension (typed FeaturePython)
  Diameter = false
  Dimline = (13903.5,400,0)
  Direction = (0,0,0)
  Distance = 7520
  End = (15873,0,0)
  Normal = (0,0,1)
  Start = (8353,0,0)
  expr: Dimline.y = Rectangle006.Placement.Base.y + 0.4m
  expr: End.x = Rectangle008.Placement.Base.x
  expr: Start.x = Rectangle006.Placement.Base.x + Rectangle006.Length
FEATURE [App::FeaturePython] InternalObjectName033  label="tc_props031"  # WARN: FeaturePython — macro-defined, semantics opaque (R4)
  altura_desde_piso = 1190
  cantidad_puertos = 2
  corriente_max_a = 15
  estado = L, N, G débil
  id_fuente = 0xe3f4c5401be30d965ff1624c8b622d9a6afa9af4ffe6eeafd7546078b64e1eeb96bb7aba828fe13ff498860b1e9555bca804dd3134197d3f5bfa341096cf3fa8
  id_pieza_electronica = 0x8e38339fdf250e2d16405b9213f8abf6e439b409ed3af0370d22034857403371d3999cb04ecb1d98faeef5916b9969185656c41b4cca2e32d63ad2ccf3695dcf
  nombre_propiedad_exportable = tomacorriente_propiedades
  num_circuito = B6
  num_tablero_distribucion = 1
  observaciones = Debe ser GFCI, mín 15 A.
  rotulo_dibujo_tecnico = 32
  tipo = NEMA 5-15R
  voltaje_max_v = 125
FEATURE [App::FeaturePython] Dimension022  # Draft dimension (typed FeaturePython)
  Diameter = false
  Dimline = (16903.5,1660,0)
  Direction = (0,0,0)
  Distance = 1300
  End = (17303,1260,0)
  Normal = (0,0,1)
  Start = (16003,1260,0)
  expr: Dimline.y = Rectangle010.Placement.Base.y + Rectangle010.Height + 0.4m
  expr: End.x = Rectangle010.Placement.Base.x + Rectangle010.Length
  expr: Start.x = Rectangle010.Placement.Base.x
FEATURE [App::FeaturePython] Dimension028  # Draft dimension (typed FeaturePython)
  Diameter = false
  Dimline = (6680,0,0)
  Direction = (0,0,0)
  Distance = 770
  End = (7140,4330,0)
  Normal = (0,0,1)
  Start = (7140,3560,0)
  expr: Dimline.x = Rectangle004.Placement.Base.x - 0.4m
  expr: Dimline.y = 0
  expr: End.y = Rectangle003.Placement.Base.y
  expr: Start.y = Rectangle004.Placement.Base.y
FEATURE [App::FeaturePython] InternalObjectName039  label="i1_propiedades004"  # WARN: FeaturePython — macro-defined, semantics opaque (R4)
  altura_desde_piso = 0
  corriente_max_a = 10
  estado = Está dañado.
  id_fuente = 0xba315ab22a890dc4c16bccaa90cda51054e74ae6ea82e64542e10d9e140a7794ac1c9b9fdc33f883fb0a3636053106b5afd326fdce792b873a72e6aa11efb76a
  id_pieza_electronica = 0x865806b2fd80f9d3d41f1d13caf22cb33be29bc8adaa97244c4017329321ff68c85f19399d774f13e350e10ddb8a11db4531072c58c377057ea4058f97fe5819
  nombre_propiedad_exportable = interruptor_propiedades
  rotulo_dibujo_tecnico = 10
  tipo_interruptor = Ordinario sencillo
  voltaje_max_v = 250
FEATURE [App::FeaturePython] InternalObjectName059  label="luz_8in_props008"  # WARN: FeaturePython — macro-defined, semantics opaque (R4)
  altura_desde_piso = 0
  color = 6500k
  estado = ok
  fuente = 0x55876f5196a1cfafdc1a24a0ed5cce5b592f0984a4dac79d6670435344794837f9f85b65072aa5fab7988351a30da20644ba8dd4323cb0aa3a3fdc18d423a51f
  id_pieza_electronica = 0x32d872addb43d5ebb37e2e3591704bc764272a0d95c83b0472e09d1f3c3c7c022ebcc86f2b9d9a34f153b15df2dca51f5c061e335e1b9a8d464e2af2e803baba
  nombre_propiedad_exportable = luz_propiedades
  potencia_w = 18
  rotulo_dibujo_tecnico = 35
  tipo_luz = Led
  voltaje_max_v = 130
  voltaje_min_v = 95
  voltaje_nominal_v = 110
FEATURE [App::FeaturePython] InternalObjectName054  label="luz_8in_props004"  # WARN: FeaturePython — macro-defined, semantics opaque (R4)
  altura_desde_piso = 0
  id_pieza_electronica = 0xcdef32c4397304ef4feaafde7f39f33da4e00bb0d0ea0b3dc6ab32062512d407f9f224b05108f1ce7a359a28141b8fa1b2a5ed5b42aeacc6f3e1089fcafa44e4
  nombre_propiedad_exportable = luz_propiedades
  potencia_w = 18
  rotulo_dibujo_tecnico = 36
  tipo_luz = Led
  voltaje_max_v = 130
  voltaje_min_v = 95
  voltaje_nominal_v = 110
FEATURE [App::FeaturePython] InternalObjectName058  label="luz_8in_props007"  # WARN: FeaturePython — macro-defined, semantics opaque (R4)
  altura_desde_piso = 0
  estado = No conectada
  id_pieza_electronica = 0xdbcb97e8915119bea2b8f30ceb891af4d39abb612b7cd828f3657ab1fc61426a09034d6c5abfca295681571af4f9af9ca441c8dc98457d837220a5cb9b5a28e5
  nombre_propiedad_exportable = luz_propiedades
  potencia_w = 18
  rotulo_dibujo_tecnico = 37
  tipo_luz = Led
  voltaje_max_v = 130
  voltaje_min_v = 95
  voltaje_nominal_v = 110
FEATURE [App::FeaturePython] InternalObjectName040  label="i1_propiedades005"  # WARN: FeaturePython — macro-defined, semantics opaque (R4)
  altura_desde_piso = 0
  corriente_max_a = 10
  id_fuente = 0x55876f5196a1cfafdc1a24a0ed5cce5b592f0984a4dac79d6670435344794837f9f85b65072aa5fab7988351a30da20644ba8dd4323cb0aa3a3fdc18d423a51f
  id_pieza_electronica = 0x34508c8811542981b2a9f313d5183e4e596ebacbd8615f6feade046dbf7e380eb34b47116118ccc18e0934221da8437cbbbe3a12c3207b82abdce4f3b17b2665
  nombre_propiedad_exportable = interruptor_propiedades
  rotulo_dibujo_tecnico = 11
  tipo_interruptor = Ordinario sencillo
  voltaje_max_v = 250
FEATURE [App::FeaturePython] Text003  # WARN: FeaturePython — macro-defined, semantics opaque (R4)
  Placement = pos=(100,100,0) rot=(0,0,1;0rad)
  Text = x2
FEATURE [App::FeaturePython] InternalObjectName044  label="i3_props"  # WARN: FeaturePython — macro-defined, semantics opaque (R4)
  altura_desde_piso = 0
  corriente_max_int1_a = 0
  corriente_max_int2_a = 0
  corriente_max_int3_a = 0
  id_fuente_int1 = 0x77c2f575a9e1860d16eeb77845606b36640c42c814c25ce4582d16db626eb3350dcd1ca6545a4fa9685324c00d2a5d50b3f390506bd7b1112e1a4a206ffe652e
  id_fuente_int2 = 0xedfc5bb3aa30eb8bd0709db342119f4dde92e71105b250b3161ed4f19e3a93e66b6ad4c2c072d329844ca216b74895e70a9c625ca2b1a1a934e3f21c3a35e75b
  id_fuente_int3 = 0x4691e5377baf05716203601fc41c00b6afecc1767ec40715de46e7d1d07508fc757dcb58bfd3060d788207d0709fcb2d94a4c594f1d8f44bc2891cf2806e2f10
  id_pieza_electronica = 0x4eb0c19f0fe41f0cf606875f5278d1653a560636c225e9d681680abe28b0ef4d7ec61c5d6d10c02cbf8d9394d04ad5d65393e7a1a1f3d2fab8c5a10aea25a0c7
  nombre_propiedad_exportable = interruptor3_propiedades
  rotulo_dibujo_tecnico = 12
  voltaje_max_int1_v = 0
  voltaje_max_int2_v = 0
  voltaje_max_int3_v = 0
FEATURE [App::FeaturePython] Dimension017  # Draft dimension (typed FeaturePython)
  Diameter = false
  Dimline = (12703.5,3170,0)
  Direction = (0,0,0)
  Distance = 1970
  End = (12790,3570,0)
  Normal = (0,0,1)
  Start = (10820,3570,0)
  expr: Dimline.y = Rectangle005.Placement.Base.y - 0.4m
  expr: End.x = Rectangle005.Placement.Base.x + Rectangle005.Length
  expr: Start.x = Rectangle005.Placement.Base.x
FEATURE [App::FeaturePython] Dimension012  # Draft dimension (typed FeaturePython)
  Diameter = false
  Dimline = (7203.5,400,0)
  Direction = (0,0,0)
  Distance = 5820
  End = (8220,0,0)
  Normal = (0,0,1)
  Start = (2400,0,0)
  expr: Dimline.y = Rectangle002.Placement.Base.y + 0.4m
  expr: End.x = Rectangle006.Placement.Base.x
  expr: Start.x = Rectangle002.Placement.Base.x + Rectangle002.Length
FEATURE [App::FeaturePython] Dimension018  # Draft dimension (typed FeaturePython)
  Diameter = false
  Dimline = (13190,3931.5,0)
  Direction = (0,0,0)
  Distance = 2440
  End = (12850,6010,0)
  Normal = (0,0,1)
  Start = (12850,3570,0)
  expr: Dimline.x = Rectangle005.Placement.Base.x + Rectangle005.Length + 0.4m
  expr: End.y = Rectangle005.Placement.Base.y + Rectangle005.Height
  expr: Start.y = Rectangle005.Placement.Base.y
FEATURE [App::FeaturePython] InternalObjectName053  label="luz_60x60_props003"  # WARN: FeaturePython — macro-defined, semantics opaque (R4)
  altura_desde_piso = 0
  id_pieza_electronica = 0xd2a1c062a0a414f50ba20ba542315e3875c4020814709fc59fb2597df964528a2f17ddaac8bae9b8e15f06ca979b4bf061395a8c7bc9627d1c9a8917807f4af9
  nombre_propiedad_exportable = luz_propiedades
  potencia_w = 0
  rotulo_dibujo_tecnico = 38
  voltaje_max_v = 130
  voltaje_min_v = 95
  voltaje_nominal_v = 110
FEATURE [App::FeaturePython] Dimension005  # Draft dimension (typed FeaturePython)
  Diameter = false
  Dimline = (12390,0,0)
  Direction = (0,0,0)
  Distance = 3570
  End = (12000,3570,0)
  Normal = (0,0,1)
  Start = (12000,0,0)
  expr: Dimline.x = Rectangle005.Placement.Base.x + Rectangle005.Length - 0.4m
  expr: End.y = Rectangle005.Placement.Base.y
  expr: Start.y = Rectangle.Placement.Base.y
FEATURE [App::FeaturePython] Dimension016  # Draft dimension (typed FeaturePython)
  Diameter = false
  Dimline = (9610,3160,0)
  Direction = (0,0,0)
  Distance = 1210
  End = (10820,3560,0)
  Normal = (0,0,1)
  Start = (9610,3560,0)
  expr: Dimline.x = Rectangle004.Placement.Base.x + Rectangle004.Length
  expr: Dimline.y = Rectangle004.Placement.Base.y - 0.4m
  expr: End.x = Rectangle005.Placement.Base.x
  expr: Start.x = Rectangle004.Placement.Base.x + Rectangle004.Length
FEATURE [App::FeaturePython] InternalObjectName052  label="luz_60x60_props002"  # WARN: FeaturePython — macro-defined, semantics opaque (R4)
  altura_desde_piso = 0
  id_pieza_electronica = 0x3a0de0213860a0e07210db22d9ddd045723e1338cdcb322eeac41fee87bb72e6be7da60bdfdc21caa851f3aa3345d45aed53e625a7e556bf04c9bf563c329965
  nombre_propiedad_exportable = luz_propiedades
  potencia_w = 0
  rotulo_dibujo_tecnico = 39
  voltaje_max_v = 130
  voltaje_min_v = 95
  voltaje_nominal_v = 110
FEATURE [App::FeaturePython] InternalObjectName057  label="luz_8in_props006"  # WARN: FeaturePython — macro-defined, semantics opaque (R4)
  altura_desde_piso = 0
  id_pieza_electronica = 0x489e90357558783d5bd86ef3661d0ae400e03add297d66a8b0c95a7ee9b64520d7931661c2a608ab53f0ba79220a94d54cedde036090b8660f19943d99c2e123
  nombre_propiedad_exportable = luz_propiedades
  potencia_w = 18
  rotulo_dibujo_tecnico = 40
  tipo_luz = Led
  voltaje_max_v = 130
  voltaje_min_v = 95
  voltaje_nominal_v = 110
FEATURE [App::FeaturePython] Dimension010  # Draft dimension (typed FeaturePython)
  Diameter = false
  Dimline = (2800,4731.5,0)
  Direction = (0,0,0)
  Distance = 1655
  End = (3270,4330,0)
  Normal = (0,0,1)
  Start = (3270,5985,0)
  expr: Dimline.x = Rectangle003.Placement.Base.x - 0.4m
  expr: Start.y = Rectangle003.Height + Rectangle003.Placement.Base.y
  expr: End.y = Rectangle003.Placement.Base.y
FEATURE [App::FeaturePython] Dimension011  # Draft dimension (typed FeaturePython)
  Diameter = false
  Dimline = (3600,31.5,0)
  Direction = (0,0,0)
  Distance = 4330
  End = (3270,4330,0)
  Normal = (0,0,1)
  Start = (3270,0,0)
  expr: Dimline.x = Rectangle003.Placement.Base.x + 0.4m
  expr: End.y = Rectangle003.Placement.Base.y
  expr: Start.y = Rectangle.Placement.Base.y
FEATURE [App::DocumentObjectGroup] Group  label="piso1_dim"
  Group = -> [Dimension022,Dimension023,Dimension026,Dimension027,Dimension028,Dimension020,Dimension021,Dimension019,Dimension012,Dimension013,Dimension014,Dimension015,Dimension016,Dimension017,Dimension018,Dimension005,Dimension006,Dimension009,Dimension010,Dimension011,Dimension029,Dimension030,Dimension031,Dimension032]
FEATURE [Part::Part2DObjectPython] Line037  # Draft 2D object (typed FeaturePython)
  ChamferSize = 0
  Closed = false
  End = (-48.9007,10,0)
  FilletRadius = 0
  Length = 128.901
  MakeFace = false
  Placement = pos=(80,10,0) rot=(0,0,1;0rad)
  Points = (2) [(0,0,0),(-128.901,-3.55271e-15,0)]
  Start = (80,10,0)
  Subdivisions = 0
FEATURE [Part::Part2DObjectPython] Line031  # Draft 2D object (typed FeaturePython)
  ChamferSize = 0
  Closed = false
  End = (-48.8237,-10,0)
  FilletRadius = 0
  Length = 128.824
  MakeFace = false
  Placement = pos=(80,-10,0) rot=(0,0,1;0rad)
  Points = (2) [(0,-5.32907e-15,0),(-128.824,-3.55271e-15,0)]
  Start = (80,-10,0)
  Subdivisions = 0
FEATURE [Part::Part2DObjectPython] Circle  # Draft 2D object (typed FeaturePython)
  FirstAngle = 0
  LastAngle = 0
  MakeFace = false
  Radius = 50
FEATURE [Part::Part2DObjectPython] Line011  # Draft 2D object (typed FeaturePython)
  ChamferSize = 0
  Closed = false
  End = (-48.9007,10,0)
  FilletRadius = 0
  Length = 128.901
  MakeFace = false
  Placement = pos=(80,10,0) rot=(0,0,1;0rad)
  Points = (2) [(0,0,0),(-128.901,-3.55271e-15,0)]
  Start = (80,10,0)
  Subdivisions = 0
FEATURE [Part::Part2DObjectPython] Circle020  # Draft 2D object (typed FeaturePython)
  FirstAngle = 0
  LastAngle = 0
  MakeFace = false
  Radius = 50
FEATURE [Part::Part2DObjectPython] Rectangle023  # Draft 2D object (typed FeaturePython)
  ChamferSize = 0
  Columns = 1
  FilletRadius = 0
  Height = 630
  Length = 90
  MakeFace = true
  Placement = pos=(19123,5407,0) rot=(0,0,1;0rad)
  Rows = 1
  expr: Placement.Base.x = Rectangle007.Placement.Base.x + Rectangle007.Length + 1.78m
  expr: Placement.Base.y = Rectangle.Placement.Base.y + Rectangle.Height - Rectangle023.Height
FEATURE [Part::Part2DObjectPython] Circle018  # Draft 2D object (typed FeaturePython)
  FirstAngle = 0
  LastAngle = 0
  MakeFace = false
  Radius = 50
FEATURE [Part::Part2DObjectPython] Circle019  # Draft 2D object (typed FeaturePython)
  FirstAngle = 0
  LastAngle = 0
  MakeFace = false
  Radius = 50
FEATURE [Part::Part2DObjectPython] Circle003  # Draft 2D object (typed FeaturePython)
  FirstAngle = 0
  LastAngle = 0
  MakeFace = false
  Radius = 50
FEATURE [Part::Part2DObjectPython] Circle026  # Draft 2D object (typed FeaturePython)
  FirstAngle = 0
  LastAngle = 0
  MakeFace = false
  Radius = 50
FEATURE [Part::Part2DObjectPython] Circle016  # Draft 2D object (typed FeaturePython)
  FirstAngle = 0
  LastAngle = 0
  MakeFace = false
  Radius = 50
FEATURE [Part::Part2DObjectPython] Circle005  # Draft 2D object (typed FeaturePython)
  FirstAngle = 0
  LastAngle = 0
  MakeFace = false
  Radius = 50
FEATURE [Part::Part2DObjectPython] Circle017  # Draft 2D object (typed FeaturePython)
  FirstAngle = 0
  LastAngle = 0
  MakeFace = false
  Radius = 50
FEATURE [Part::Part2DObjectPython] Line040  # Draft 2D object (typed FeaturePython)
  ChamferSize = 0
  Closed = false
  End = (-48.8237,-10,0)
  FilletRadius = 0
  Length = 128.824
  MakeFace = false
  Placement = pos=(80,-10,0) rot=(0,0,1;0rad)
  Points = (2) [(0,-5.32907e-15,0),(-128.824,-3.55271e-15,0)]
  Start = (80,-10,0)
  Subdivisions = 0
FEATURE [Part::Part2DObjectPython] Line039  # Draft 2D object (typed FeaturePython)
  ChamferSize = 0
  Closed = false
  End = (-48.8237,-10,0)
  FilletRadius = 0
  Length = 128.824
  MakeFace = false
  Placement = pos=(80,-10,0) rot=(0,0,1;0rad)
  Points = (2) [(0,-5.32907e-15,0),(-128.824,-3.55271e-15,0)]
  Start = (80,-10,0)
  Subdivisions = 0
FEATURE [Part::Part2DObjectPython] Line033  # Draft 2D object (typed FeaturePython)
  ChamferSize = 0
  Closed = false
  End = (-48.8237,-10,0)
  FilletRadius = 0
  Length = 128.824
  MakeFace = false
  Placement = pos=(80,-10,0) rot=(0,0,1;0rad)
  Points = (2) [(0,-5.32907e-15,0),(-128.824,-3.55271e-15,0)]
  Start = (80,-10,0)
  Subdivisions = 0
FEATURE [Part::Part2DObjectPython] Line032  # Draft 2D object (typed FeaturePython)
  ChamferSize = 0
  Closed = false
  End = (-48.9007,10,0)
  FilletRadius = 0
  Length = 128.901
  MakeFace = false
  Placement = pos=(80,10,0) rot=(0,0,1;0rad)
  Points = (2) [(0,0,0),(-128.901,-3.55271e-15,0)]
  Start = (80,10,0)
  Subdivisions = 0
FEATURE [App::Part] Part133  label="contenido025"
  Group = -> [Circle016,Line032,Line033]
  Origin = -> Origin133
FEATURE [Part::Part2DObjectPython] Line006  # Draft 2D object (typed FeaturePython)
  ChamferSize = 0
  Closed = false
  End = (-48.8237,-10,0)
  FilletRadius = 0
  Length = 128.824
  MakeFace = false
  Placement = pos=(80,-10,0) rot=(0,0,1;0rad)
  Points = (2) [(0,-5.32907e-15,0),(-128.824,-3.55271e-15,0)]
  Start = (80,-10,0)
  Subdivisions = 0
FEATURE [Part::Part2DObjectPython] Line051  # Draft 2D object (typed FeaturePython)
  ChamferSize = 0
  Closed = false
  End = (-48.9007,10,0)
  FilletRadius = 0
  Length = 128.901
  MakeFace = false
  Placement = pos=(80,10,0) rot=(0,0,1;0rad)
  Points = (2) [(0,0,0),(-128.901,-3.55271e-15,0)]
  Start = (80,10,0)
  Subdivisions = 0
FEATURE [Part::Part2DObjectPython] Line053  # Draft 2D object (typed FeaturePython)
  ChamferSize = 0
  Closed = false
  End = (-48.8237,-10,0)
  FilletRadius = 0
  Length = 128.824
  MakeFace = false
  Placement = pos=(80,-10,0) rot=(0,0,1;0rad)
  Points = (2) [(0,-5.32907e-15,0),(-128.824,-3.55271e-15,0)]
  Start = (80,-10,0)
  Subdivisions = 0
FEATURE [Part::Part2DObjectPython] Line052  # Draft 2D object (typed FeaturePython)
  ChamferSize = 0
  Closed = false
  End = (-48.9007,10,0)
  FilletRadius = 0
  Length = 128.901
  MakeFace = false
  Placement = pos=(80,10,0) rot=(0,0,1;0rad)
  Points = (2) [(0,0,0),(-128.901,-3.55271e-15,0)]
  Start = (80,10,0)
  Subdivisions = 0
FEATURE [Part::Part2DObjectPython] Line054  # Draft 2D object (typed FeaturePython)
  ChamferSize = 0
  Closed = false
  End = (-48.9007,10,0)
  FilletRadius = 0
  Length = 128.901
  MakeFace = false
  Placement = pos=(80,10,0) rot=(0,0,1;0rad)
  Points = (2) [(0,0,0),(-128.901,-3.55271e-15,0)]
  Start = (80,10,0)
  Subdivisions = 0
FEATURE [Part::Part2DObjectPython] Line036  # Draft 2D object (typed FeaturePython)
  ChamferSize = 0
  Closed = false
  End = (-48.8237,-10,0)
  FilletRadius = 0
  Length = 128.824
  MakeFace = false
  Placement = pos=(80,-10,0) rot=(0,0,1;0rad)
  Points = (2) [(0,-5.32907e-15,0),(-128.824,-3.55271e-15,0)]
  Start = (80,-10,0)
  Subdivisions = 0
FEATURE [App::Part] Part137  label="contenido027"
  Group = -> [Circle018,Line037,Line036]
  Origin = -> Origin136
FEATURE [Part::Part2DObjectPython] Line059  # Draft 2D object (typed FeaturePython)
  ChamferSize = 0
  Closed = false
  End = (-48.8237,-10,0)
  FilletRadius = 0
  Length = 128.824
  MakeFace = false
  Placement = pos=(80,-10,0) rot=(0,0,1;0rad)
  Points = (2) [(0,-5.32907e-15,0),(-128.824,-3.55271e-15,0)]
  Start = (80,-10,0)
  Subdivisions = 0
FEATURE [Part::Part2DObjectPython] Line042  # Draft 2D object (typed FeaturePython)
  ChamferSize = 0
  Closed = false
  End = (-48.8237,-10,0)
  FilletRadius = 0
  Length = 128.824
  MakeFace = false
  Placement = pos=(80,-10,0) rot=(0,0,1;0rad)
  Points = (2) [(0,-5.32907e-15,0),(-128.824,-3.55271e-15,0)]
  Start = (80,-10,0)
  Subdivisions = 0
FEATURE [Part::Part2DObjectPython] Line048  # Draft 2D object (typed FeaturePython)
  ChamferSize = 0
  Closed = false
  End = (-48.8237,-10,0)
  FilletRadius = 0
  Length = 128.824
  MakeFace = false
  Placement = pos=(80,-10,0) rot=(0,0,1;0rad)
  Points = (2) [(0,-5.32907e-15,0),(-128.824,-3.55271e-15,0)]
  Start = (80,-10,0)
  Subdivisions = 0
FEATURE [Part::Part2DObjectPython] Line047  # Draft 2D object (typed FeaturePython)
  ChamferSize = 0
  Closed = false
  End = (-48.9007,10,0)
  FilletRadius = 0
  Length = 128.901
  MakeFace = false
  Placement = pos=(80,10,0) rot=(0,0,1;0rad)
  Points = (2) [(0,0,0),(-128.901,-3.55271e-15,0)]
  Start = (80,10,0)
  Subdivisions = 0
FEATURE [Part::Part2DObjectPython] Line044  # Draft 2D object (typed FeaturePython)
  ChamferSize = 0
  Closed = false
  End = (-48.8237,-10,0)
  FilletRadius = 0
  Length = 128.824
  MakeFace = false
  Placement = pos=(80,-10,0) rot=(0,0,1;0rad)
  Points = (2) [(0,-5.32907e-15,0),(-128.824,-3.55271e-15,0)]
  Start = (80,-10,0)
  Subdivisions = 0
FEATURE [Part::Part2DObjectPython] Line049  # Draft 2D object (typed FeaturePython)
  ChamferSize = 0
  Closed = false
  End = (-48.9007,10,0)
  FilletRadius = 0
  Length = 128.901
  MakeFace = false
  Placement = pos=(80,10,0) rot=(0,0,1;0rad)
  Points = (2) [(0,0,0),(-128.901,-3.55271e-15,0)]
  Start = (80,10,0)
  Subdivisions = 0
FEATURE [Part::Part2DObjectPython] Line046  # Draft 2D object (typed FeaturePython)
  ChamferSize = 0
  Closed = false
  End = (-48.8237,-10,0)
  FilletRadius = 0
  Length = 128.824
  MakeFace = false
  Placement = pos=(80,-10,0) rot=(0,0,1;0rad)
  Points = (2) [(0,-5.32907e-15,0),(-128.824,-3.55271e-15,0)]
  Start = (80,-10,0)
  Subdivisions = 0
FEATURE [App::Part] Part153  label="contenido035"
  Group = -> [Circle026,Line052,Line053]
  Origin = -> Origin152
FEATURE [Part::Part2DObjectPython] Circle023  # Draft 2D object (typed FeaturePython)
  FirstAngle = 0
  LastAngle = 0
  MakeFace = false
  Radius = 50
FEATURE [Part::Part2DObjectPython] Circle021  # Draft 2D object (typed FeaturePython)
  FirstAngle = 0
  LastAngle = 0
  MakeFace = false
  Radius = 50
FEATURE [Part::Part2DObjectPython] ShapeString019  label="rotulo_dibujo_tecnico__019"  # Draft 2D object (typed FeaturePython)
  FontFile = <path>
  Placement = pos=(0,100,0) rot=(0,0,1;0rad)
  Size = 50
  String = 36
  Tracking = 0
FEATURE [Part::Part2DObjectPython] ShapeString016  label="rotulo_dibujo_tecnico__016"  # Draft 2D object (typed FeaturePython)
  FontFile = <path>
  Placement = pos=(0,100,0) rot=(0,0,1;0rad)
  Size = 50
  String = 22
  Tracking = 0
FEATURE [App::Part] Part186  label="luz_8in__001"
  Group = -> [InternalObjectName047,Part185,ShapeString016]
  Origin = -> Origin185
  Placement = pos=(660,5040,0) rot=(0,0,1;0.785398rad)
  expr: Placement.Base.y = Rectangle002.Placement.Base.y + Rectangle002.Height + 339cm
  expr: Placement.Base.x = Rectangle.Placement.Base.x + 66cm
FEATURE [Part::Part2DObjectPython] ShapeString024  label="rotulo_dibujo_tecnico__024"  # Draft 2D object (typed FeaturePython)
  FontFile = <path>
  Placement = pos=(0,100,0) rot=(0,0,1;0rad)
  Size = 50
  String = 16
  Tracking = 0
FEATURE [Part::Part2DObjectPython] ShapeString052  label="rotulo_dibujo_tecnico__052"  # Draft 2D object (typed FeaturePython)
  FontFile = <path>
  Placement = pos=(0,100,0) rot=(0,0,1;0rad)
  Size = 50
  String = 12
  Tracking = 0
FEATURE [Part::Part2DObjectPython] Line041  # Draft 2D object (typed FeaturePython)
  ChamferSize = 0
  Closed = false
  End = (-48.9007,10,0)
  FilletRadius = 0
  Length = 128.901
  MakeFace = false
  Placement = pos=(80,10,0) rot=(0,0,1;0rad)
  Points = (2) [(0,0,0),(-128.901,-3.55271e-15,0)]
  Start = (80,10,0)
  Subdivisions = 0
FEATURE [Part::Part2DObjectPython] Line045  # Draft 2D object (typed FeaturePython)
  ChamferSize = 0
  Closed = false
  End = (-48.9007,10,0)
  FilletRadius = 0
  Length = 128.901
  MakeFace = false
  Placement = pos=(80,10,0) rot=(0,0,1;0rad)
  Points = (2) [(0,0,0),(-128.901,-3.55271e-15,0)]
  Start = (80,10,0)
  Subdivisions = 0
FEATURE [Part::Part2DObjectPython] ShapeString002  label="rotulo_dibujo_tecnico__002"  # Draft 2D object (typed FeaturePython)
  FontFile = <path>
  Placement = pos=(100,100,0) rot=(0,0,1;0rad)
  Size = 50
  String = 3
  Tracking = 0
FEATURE [Part::Part2DObjectPython] ShapeString034  label="rotulo_dibujo_tecnico__034"  # Draft 2D object (typed FeaturePython)
  FontFile = <path>
  Placement = pos=(0,100,0) rot=(0,0,1;0rad)
  Size = 50
  String = 18
  Tracking = 0
FEATURE [App::Part] Part220  label="luz_8in__014"
  Group = -> [InternalObjectName065,Part221,ShapeString034]
  Origin = -> Origin220
  Placement = pos=(11233,2960,0) rot=(0,0,1;0rad)
  expr: Placement.Base.y = Part218.Placement.Base.y
  expr: Placement.Base.x = Part218.Placement.Base.x + 250cm
FEATURE [Part::Part2DObjectPython] Line050  # Draft 2D object (typed FeaturePython)
  ChamferSize = 0
  Closed = false
  End = (-48.8237,-10,0)
  FilletRadius = 0
  Length = 128.824
  MakeFace = false
  Placement = pos=(80,-10,0) rot=(0,0,1;0rad)
  Points = (2) [(0,-5.32907e-15,0),(-128.824,-3.55271e-15,0)]
  Start = (80,-10,0)
  Subdivisions = 0
FEATURE [Part::Part2DObjectPython] ShapeString046  label="rotulo_dibujo_tecnico__046"  # Draft 2D object (typed FeaturePython)
  FontFile = <path>
  Placement = pos=(0,100,0) rot=(0,0,1;0rad)
  Size = 50
  String = 1
  Tracking = 0
FEATURE [Part::Part2DObjectPython] ShapeString003  label="rotulo_dibujo_tecnico__003"  # Draft 2D object (typed FeaturePython)
  FontFile = <path>
  Placement = pos=(-100,100,0) rot=(0,0,1;0rad)
  Size = 50
  String = 5
  Tracking = 0
FEATURE [Part::Part2DObjectPython] ShapeString012  label="rotulo_dibujo_tecnico__012"  # Draft 2D object (typed FeaturePython)
  FontFile = <path>
  Placement = pos=(0,100,0) rot=(0,0,1;0rad)
  Size = 50
  String = 12
  Tracking = 0
FEATURE [App::Part] Part090  label="interruptor_triple__"
  Group = -> [Line130,Group016,Text004,InternalObjectName044,Circle064,ShapeString012]
  Origin = -> Origin090
  Placement = pos=(17393,3747,0) rot=(0,0,1;0rad)
  expr: Placement.Base.y = Rectangle007.Placement.Base.y + 440mm
  expr: Placement.Base.x = Rectangle007.Placement.Base.x + Rectangle007.Length + 50mm
FEATURE [Part::Part2DObjectPython] ShapeString049  label="rotulo_dibujo_tecnico__049"  # Draft 2D object (typed FeaturePython)
  FontFile = <path>
  Placement = pos=(0,100,0) rot=(0,0,1;0rad)
  Size = 50
  String = 7
  Tracking = 0
FEATURE [Part::Part2DObjectPython] Line058  # Draft 2D object (typed FeaturePython)
  ChamferSize = 0
  Closed = false
  End = (-48.9007,10,0)
  FilletRadius = 0
  Length = 128.901
  MakeFace = false
  Placement = pos=(80,10,0) rot=(0,0,1;0rad)
  Points = (2) [(0,0,0),(-128.901,-3.55271e-15,0)]
  Start = (80,10,0)
  Subdivisions = 0
FEATURE [Part::Part2DObjectPython] ShapeString004  label="rotulo_dibujo_tecnico__004"  # Draft 2D object (typed FeaturePython)
  FontFile = <path>
  Placement = pos=(0,150,0) rot=(0,0,1;3.14159rad)
  Size = 50
  String = 1
  Tracking = 0
FEATURE [Part::Part2DObjectPython] ShapeString045  label="rotulo_dibujo_tecnico__045"  # Draft 2D object (typed FeaturePython)
  FontFile = <path>
  Placement = pos=(0,100,0) rot=(0,0,1;0rad)
  Size = 50
  String = 15
  Tracking = 0
FEATURE [App::Part] Part242  label="luz_8in__025"
  Group = -> [InternalObjectName076,Part243,ShapeString045]
  Origin = -> Origin242
  Placement = pos=(19730,5157,0) rot=(0,0,1;0rad)
  expr: Placement.Base.y = Part240.Placement.Base.y
  expr: Placement.Base.x = Part246.Placement.Base.x
FEATURE [Part::Part2DObjectPython] ShapeString067  label="rotulo_dibujo_tecnico__067"  # Draft 2D object (typed FeaturePython)
  FontFile = <path>
  Placement = pos=(0,100,0) rot=(0,0,1;0rad)
  Size = 50
  String = 9
  Tracking = 0
FEATURE [Part::Part2DObjectPython] ShapeString029  label="rotulo_dibujo_tecnico__029"  # Draft 2D object (typed FeaturePython)
  FontFile = <path>
  Placement = pos=(0,100,0) rot=(0,0,1;0rad)
  Size = 50
  String = 30
  Tracking = 0
FEATURE [Part::Part2DObjectPython] Circle025  # Draft 2D object (typed FeaturePython)
  FirstAngle = 0
  LastAngle = 0
  MakeFace = false
  Radius = 50
FEATURE [Part::Part2DObjectPython] Circle027  # Draft 2D object (typed FeaturePython)
  FirstAngle = 0
  LastAngle = 0
  MakeFace = false
  Radius = 50
FEATURE [Part::Part2DObjectPython] ShapeString064  label="rotulo_dibujo_tecnico__064"  # Draft 2D object (typed FeaturePython)
  FontFile = <path>
  Placement = pos=(0,-150,0) rot=(0,0,1;0rad)
  Size = 50
  String = 8
  Tracking = 0
FEATURE [Part::Part2DObjectPython] ShapeString076  label="rotulo_dibujo_tecnico__076"  # Draft 2D object (typed FeaturePython)
  FontFile = <path>
  Placement = pos=(0,-150,0) rot=(0,0,1;0rad)
  Size = 50
  String = 12
  Tracking = 0
FEATURE [Part::Part2DObjectPython] Rectangle022  # Draft 2D object (typed FeaturePython)
  ChamferSize = 0
  Columns = 1
  FilletRadius = 0
  Height = 100
  Length = 920
  MakeFace = true
  Placement = pos=(8580,4430,0) rot=(0,0,1;0rad)
  Rows = 1
  expr: Length = Rectangle020.Placement.Base.x - Rectangle021.Placement.Base.x - Rectangle021.Length
  expr: Placement.Base.y = Dimension040.End.y
  expr: Placement.Base.x = Rectangle021.Placement.Base.x + Rectangle021.Length
FEATURE [Part::Part2DObjectPython] ShapeString027  label="rotulo_dibujo_tecnico__027"  # Draft 2D object (typed FeaturePython)
  FontFile = <path>
  Placement = pos=(0,100,0) rot=(0,0,1;0rad)
  Size = 50
  String = 37
  Tracking = 0
FEATURE [Part::Part2DObjectPython] ShapeString025  label="rotulo_dibujo_tecnico__025"  # Draft 2D object (typed FeaturePython)
  FontFile = <path>
  Placement = pos=(0,100,0) rot=(0,0,1;0rad)
  Size = 50
  String = 31
  Tracking = 0
FEATURE [Part::Part2DObjectPython] ShapeString062  label="rotulo_dibujo_tecnico__062"  # Draft 2D object (typed FeaturePython)
  FontFile = <path>
  Placement = pos=(0,100,0) rot=(0,0,1;0rad)
  Size = 50
  String = 17
  Tracking = 0
FEATURE [Part::Part2DObjectPython] ShapeString037  label="rotulo_dibujo_tecnico__037"  # Draft 2D object (typed FeaturePython)
  FontFile = <path>
  Placement = pos=(0,100,0) rot=(0,0,1;0rad)
  Size = 50
  String = 29
  Tracking = 0
FEATURE [App::Part] Part226  label="luz_8in__017"
  Group = -> [InternalObjectName068,Part227,ShapeString037]
  Origin = -> Origin226
  Placement = pos=(13680,4867,0) rot=(0,0,1;0rad)
  expr: Placement.Base.x = Rectangle005.Placement.Base.x + Rectangle005.Length + 89cm
  expr: Placement.Base.y = Rectangle.Placement.Base.y + Rectangle.Height - 117cm
FEATURE [Part::Part2DObjectPython] ShapeString026  label="rotulo_dibujo_tecnico__026"  # Draft 2D object (typed FeaturePython)
  FontFile = <path>
  Placement = pos=(0,100,0) rot=(0,0,1;0rad)
  Size = 50
  String = 40
  Tracking = 0
FEATURE [Part::Part2DObjectPython] ShapeString075  label="rotulo_dibujo_tecnico__075"  # Draft 2D object (typed FeaturePython)
  FontFile = <path>
  Placement = pos=(0,100,0) rot=(0,0,1;0rad)
  Size = 50
  String = 4
  Tracking = 0
FEATURE [Part::Part2DObjectPython] ShapeString036  label="rotulo_dibujo_tecnico__036"  # Draft 2D object (typed FeaturePython)
  FontFile = <path>
  Placement = pos=(0,100,0) rot=(0,0,1;0rad)
  Size = 50
  String = 9
  Tracking = 0
FEATURE [App::Part] Part224  label="luz_8in__016"
  Group = -> [InternalObjectName067,Part225,ShapeString036]
  Origin = -> Origin224
  Placement = pos=(16633,2960,0) rot=(0,0,1;0rad)
  expr: Placement.Base.y = Part218.Placement.Base.y
  expr: Placement.Base.x = Part222.Placement.Base.x + 260cm
FEATURE [Part::Part2DObjectPython] Line013  # Draft 2D object (typed FeaturePython)
  ChamferSize = 0
  Closed = false
  End = (-48.9007,10,0)
  FilletRadius = 0
  Length = 128.901
  MakeFace = false
  Placement = pos=(80,10,0) rot=(0,0,1;0rad)
  Points = (2) [(0,0,0),(-128.901,-3.55271e-15,0)]
  Start = (80,10,0)
  Subdivisions = 0
FEATURE [Part::Part2DObjectPython] Circle024  # Draft 2D object (typed FeaturePython)
  FirstAngle = 0
  LastAngle = 0
  MakeFace = false
  Radius = 50
FEATURE [App::Part] Part149  label="contenido033"
  Group = -> [Circle024,Line049,Line048]
  Origin = -> Origin149
FEATURE [Part::Part2DObjectPython] Circle022  # Draft 2D object (typed FeaturePython)
  FirstAngle = 0
  LastAngle = 0
  MakeFace = false
  Radius = 50
FEATURE [Part::Part2DObjectPython] Line014  # Draft 2D object (typed FeaturePython)
  ChamferSize = 0
  Closed = false
  End = (-48.8237,-10,0)
  FilletRadius = 0
  Length = 128.824
  MakeFace = false
  Placement = pos=(80,-10,0) rot=(0,0,1;0rad)
  Points = (2) [(0,-5.32907e-15,0),(-128.824,-3.55271e-15,0)]
  Start = (80,-10,0)
  Subdivisions = 0
FEATURE [Part::Part2DObjectPython] Rectangle019  # Draft 2D object (typed FeaturePython)
  ChamferSize = 0
  Columns = 1
  FilletRadius = 0
  Height = 100
  Length = 310
  MakeFace = true
  Placement = pos=(8450,3560,0) rot=(0,0,1;0rad)
  Rows = 1
  expr: Placement.Base.x = Rectangle021.Placement.Base.x + Rectangle021.Length - Rectangle019.Length + 0.18m
  expr: Placement.Base.y = Rectangle004.Placement.Base.y
FEATURE [Part::Part2DObjectPython] Rectangle021  # Draft 2D object (typed FeaturePython)
  ChamferSize = 0
  Columns = 1
  FilletRadius = 0
  Height = 1000
  Length = 120
  MakeFace = true
  Placement = pos=(8460,3560,0) rot=(0,0,1;0rad)
  Rows = 1
  expr: Height = Rectangle004.Height
  expr: Placement.Base.x = Rectangle020.Placement.Base.x - 0.92m - Rectangle021.Length
FEATURE [Part::Part2DObjectPython] Rectangle020  # Draft 2D object (typed FeaturePython)
  ChamferSize = 0
  Columns = 1
  FilletRadius = 0
  Height = 1000
  Length = 110
  MakeFace = true
  Placement = pos=(9500,3560,0) rot=(0,0,1;0rad)
  Rows = 1
  expr: Height = Rectangle004.Height
  expr: Placement.Base.y = Rectangle004.Placement.Base.y
FEATURE [App::Part] Part141  label="contenido029"
  Group = -> [Circle020,Line041,Line040]
  Origin = -> Origin141
FEATURE [Part::Part2DObjectPython] Line055  # Draft 2D object (typed FeaturePython)
  ChamferSize = 0
  Closed = false
  End = (-48.8237,-10,0)
  FilletRadius = 0
  Length = 128.824
  MakeFace = false
  Placement = pos=(80,-10,0) rot=(0,0,1;0rad)
  Points = (2) [(0,-5.32907e-15,0),(-128.824,-3.55271e-15,0)]
  Start = (80,-10,0)
  Subdivisions = 0
FEATURE [App::Part] Part154  label="contenido036"
  Group = -> [Circle027,Line054,Line055]
  Origin = -> Origin155
FEATURE [App::Part] Part150  label="contenido034"
  Group = -> [Circle025,Line051,Line050]
  Origin = -> Origin151
FEATURE [App::Part] Part147  label="contenido032"
  Group = -> [Circle023,Line047,Line046]
  Origin = -> Origin147
FEATURE [Part::Part2DObjectPython] Rectangle013  # Draft 2D object (typed FeaturePython)
  ChamferSize = 0
  Columns = 1
  FilletRadius = 0
  Height = 1655
  Length = 130
  MakeFace = true
  Placement = pos=(4240,4330,0) rot=(0,0,1;0rad)
  Rows = 1
  expr: Height = Rectangle003.Height
  expr: Placement.Base.y = Rectangle003.Placement.Base.y
  expr: Placement.Base.x = Rectangle003.Placement.Base.x + 1.04m
FEATURE [Part::Part2DObjectPython] Rectangle015  # Draft 2D object (typed FeaturePython)
  ChamferSize = 0
  Columns = 1
  FilletRadius = 0
  Height = 1655
  Length = 170
  MakeFace = true
  Placement = pos=(5630,4330,0) rot=(0,0,1;0rad)
  Rows = 1
  expr: Height = Rectangle003.Height
  expr: Placement.Base.y = Rectangle003.Placement.Base.y
  expr: Placement.Base.x = Rectangle013.Placement.Base.x + Rectangle013.Length + 1.26m
FEATURE [Part::Part2DObjectPython] Circle007  # Draft 2D object (typed FeaturePython)
  FirstAngle = 0
  LastAngle = 0
  MakeFace = false
  Radius = 50
FEATURE [Part::Part2DObjectPython] Line043  # Draft 2D object (typed FeaturePython)
  ChamferSize = 0
  Closed = false
  End = (-48.9007,10,0)
  FilletRadius = 0
  Length = 128.901
  MakeFace = false
  Placement = pos=(80,10,0) rot=(0,0,1;0rad)
  Points = (2) [(0,0,0),(-128.901,-3.55271e-15,0)]
  Start = (80,10,0)
  Subdivisions = 0
FEATURE [App::Part] Part143  label="contenido030"
  Group = -> [Circle021,Line043,Line042]
  Origin = -> Origin143
FEATURE [Part::Part2DObjectPython] Line015  # Draft 2D object (typed FeaturePython)
  ChamferSize = 0
  Closed = false
  End = (-48.9007,10,0)
  FilletRadius = 0
  Length = 128.901
  MakeFace = false
  Placement = pos=(80,10,0) rot=(0,0,1;0rad)
  Points = (2) [(0,0,0),(-128.901,-3.55271e-15,0)]
  Start = (80,10,0)
  Subdivisions = 0
FEATURE [App::Part] Part115  label="contenido016"
  Group = -> [Circle007,Line015,Line014]
  Origin = -> Origin114
FEATURE [App::Part] Part114  label="tomacorriente__007"
  Group = -> [InternalObjectName009,Part115,ShapeString064]
  Origin = -> Origin115
  Placement = pos=(3600,5935,0) rot=(0,0,1;0rad)
  expr: Placement.Base.x = Rectangle013.Placement.Base.x - 0.64m
FEATURE [App::Part] Part145  label="contenido031"
  Group = -> [Circle022,Line045,Line044]
  Origin = -> Origin145
FEATURE [App::Part] Part272  label="cbk3__"
  Group = -> [InternalObjectName093]
  Origin = -> Origin272
FEATURE [App::Part] Part245  label="contenido080"
  Group = -> [Circle093,Line186,Line187]
  Origin = -> Origin245
  Placement = pos=(0,0,0) rot=(0,0,1;0.785398rad)
FEATURE [Part::Part2DObjectPython] Line189  # Draft 2D object (typed FeaturePython)
  ChamferSize = 0
  Closed = false
  End = (-100,3.8e-15,0)
  FilletRadius = 0
  Length = 200
  MakeFace = true
  Placement = pos=(100,1.8e-14,0) rot=(0,0,1;0rad)
  Points = (2) [(0,0,0),(-200,-1.42109e-14,0)]
  Start = (100,1.8e-14,0)
  Subdivisions = 0
FEATURE [Part::Part2DObjectPython] Circle098  # Draft 2D object (typed FeaturePython)
  FirstAngle = 0
  LastAngle = 0
  MakeFace = true
  Radius = 100
FEATURE [Part::Part2DObjectPython] Line190  # Draft 2D object (typed FeaturePython)
  ChamferSize = 0
  Closed = false
  End = (0,-100,0)
  FilletRadius = 0
  Length = 200
  MakeFace = true
  Placement = pos=(0,100,0) rot=(0,0,1;0rad)
  Points = (2) [(0,0,0),(0,-200,0)]
  Start = (0,100,0)
  Subdivisions = 0
FEATURE [App::Part] Part244  label="luz_8in__026"
  Group = -> [InternalObjectName077,Part245,ShapeString046]
  Origin = -> Origin244
  Placement = pos=(19730,4147,0) rot=(0,0,1;0rad)
  expr: Placement.Base.y = Part242.Placement.Base.y - 101cm
  expr: Placement.Base.x = Part246.Placement.Base.x
FEATURE [Part::Part2DObjectPython] Circle095  # Draft 2D object (typed FeaturePython)
  FirstAngle = 0
  LastAngle = 0
  MakeFace = true
  Radius = 100
FEATURE [Part::Part2DObjectPython] Line202  # Draft 2D object (typed FeaturePython)
  ChamferSize = 0
  Closed = false
  End = (0,-100,0)
  FilletRadius = 0
  Length = 200
  MakeFace = true
  Placement = pos=(0,100,0) rot=(0,0,1;0rad)
  Points = (2) [(0,0,0),(0,-200,0)]
  Start = (0,100,0)
  Subdivisions = 0
FEATURE [Part::Part2DObjectPython] ShapeString079  label="rotulo_dibujo_tecnico__079"  # Draft 2D object (typed FeaturePython)
  FontFile = <path>
  Placement = pos=(0,-150,0) rot=(0,0,1;0rad)
  Size = 50
  String = 22
  Tracking = 0
FEATURE [App::Part] Part144  label="tomacorriente__022"
  Group = -> [InternalObjectName024,Part145,ShapeString079]
  Origin = -> Origin144
  Placement = pos=(22200,4467,0) rot=(0,0,1;1.5708rad)
  expr: Placement.Base.y = Rectangle.Placement.Base.y + Rectangle.Height - 1.57m
  expr: Placement.Base.x = Rectangle.Placement.Base.x + Rectangle.Length - 0.05m
FEATURE [Part::Part2DObjectPython] ShapeString085  label="rotulo_dibujo_tecnico__085"  # Draft 2D object (typed FeaturePython)
  FontFile = <path>
  Placement = pos=(0,100,0) rot=(0,0,1;0rad)
  Size = 50
  String = 28
  Tracking = 0
FEATURE [Part::Part2DObjectPython] ShapeString035  label="rotulo_dibujo_tecnico__035"  # Draft 2D object (typed FeaturePython)
  FontFile = <path>
  Placement = pos=(0,100,0) rot=(0,0,1;0rad)
  Size = 50
  String = 27
  Tracking = 0
FEATURE [App::Part] Part222  label="luz_8in__015"
  Group = -> [InternalObjectName066,Part223,ShapeString035]
  Origin = -> Origin222
  Placement = pos=(14033,2960,0) rot=(0,0,1;0rad)
  expr: Placement.Base.y = Part218.Placement.Base.y
  expr: Placement.Base.x = Part220.Placement.Base.x + 280cm
FEATURE [Part::Part2DObjectPython] Circle097  # Draft 2D object (typed FeaturePython)
  FirstAngle = 0
  LastAngle = 0
  MakeFace = true
  Radius = 100
FEATURE [Part::Part2DObjectPython] Circle094  # Draft 2D object (typed FeaturePython)
  FirstAngle = 0
  LastAngle = 0
  MakeFace = true
  Radius = 100
FEATURE [Part::Part2DObjectPython] Line195  # Draft 2D object (typed FeaturePython)
  ChamferSize = 0
  Closed = false
  End = (-100,3.8e-15,0)
  FilletRadius = 0
  Length = 200
  MakeFace = true
  Placement = pos=(100,1.8e-14,0) rot=(0,0,1;0rad)
  Points = (2) [(0,0,0),(-200,-1.42109e-14,0)]
  Start = (100,1.8e-14,0)
  Subdivisions = 0
FEATURE [Part::Part2DObjectPython] Line191  # Draft 2D object (typed FeaturePython)
  ChamferSize = 0
  Closed = false
  End = (-100,3.8e-15,0)
  FilletRadius = 0
  Length = 200
  MakeFace = true
  Placement = pos=(100,1.8e-14,0) rot=(0,0,1;0rad)
  Points = (2) [(0,0,0),(-200,-1.42109e-14,0)]
  Start = (100,1.8e-14,0)
  Subdivisions = 0
FEATURE [App::Part] Part249  label="contenido082"
  Group = -> [Circle095,Line190,Line191]
  Origin = -> Origin249
  Placement = pos=(0,0,0) rot=(0,0,1;0.785398rad)
FEATURE [App::Part] Part104  label="cbk__"
  Group = -> [InternalObjectName086]
  Origin = -> Origin104
FEATURE [Part::Part2DObjectPython] Circle096  # Draft 2D object (typed FeaturePython)
  FirstAngle = 0
  LastAngle = 0
  MakeFace = true
  Radius = 100
FEATURE [Part::Part2DObjectPython] Line194  # Draft 2D object (typed FeaturePython)
  ChamferSize = 0
  Closed = false
  End = (0,-100,0)
  FilletRadius = 0
  Length = 200
  MakeFace = true
  Placement = pos=(0,100,0) rot=(0,0,1;0rad)
  Points = (2) [(0,0,0),(0,-200,0)]
  Start = (0,100,0)
  Subdivisions = 0
FEATURE [App::Part] Part253  label="contenido084"
  Group = -> [Circle097,Line194,Line195]
  Origin = -> Origin253
  Placement = pos=(0,0,0) rot=(0,0,1;0.785398rad)
FEATURE [Part::Part2DObjectPython] Line188  # Draft 2D object (typed FeaturePython)
  ChamferSize = 0
  Closed = false
  End = (0,-100,0)
  FilletRadius = 0
  Length = 200
  MakeFace = true
  Placement = pos=(0,100,0) rot=(0,0,1;0rad)
  Points = (2) [(0,0,0),(0,-200,0)]
  Start = (0,100,0)
  Subdivisions = 0
FEATURE [App::Part] Part247  label="contenido081"
  Group = -> [Circle094,Line188,Line189]
  Origin = -> Origin247
  Placement = pos=(0,0,0) rot=(0,0,1;0.785398rad)
FEATURE [Part::Part2DObjectPython] Line199  # Draft 2D object (typed FeaturePython)
  ChamferSize = 0
  Closed = false
  End = (-100,3.8e-15,0)
  FilletRadius = 0
  Length = 200
  MakeFace = true
  Placement = pos=(100,1.8e-14,0) rot=(0,0,1;0rad)
  Points = (2) [(0,0,0),(-200,-1.42109e-14,0)]
  Start = (100,1.8e-14,0)
  Subdivisions = 0
FEATURE [Part::Part2DObjectPython] Line193  # Draft 2D object (typed FeaturePython)
  ChamferSize = 0
  Closed = false
  End = (-100,3.8e-15,0)
  FilletRadius = 0
  Length = 200
  MakeFace = true
  Placement = pos=(100,1.8e-14,0) rot=(0,0,1;0rad)
  Points = (2) [(0,0,0),(-200,-1.42109e-14,0)]
  Start = (100,1.8e-14,0)
  Subdivisions = 0
FEATURE [Part::Part2DObjectPython] Line192  # Draft 2D object (typed FeaturePython)
  ChamferSize = 0
  Closed = false
  End = (0,-100,0)
  FilletRadius = 0
  Length = 200
  MakeFace = true
  Placement = pos=(0,100,0) rot=(0,0,1;0rad)
  Points = (2) [(0,0,0),(0,-200,0)]
  Start = (0,100,0)
  Subdivisions = 0
FEATURE [App::Part] Part251  label="contenido083"
  Group = -> [Circle096,Line192,Line193]
  Origin = -> Origin251
  Placement = pos=(0,0,0) rot=(0,0,1;0.785398rad)
FEATURE [App::Part] Part250  label="luz_8in__029"
  Group = -> [InternalObjectName080,Part251,ShapeString049]
  Origin = -> Origin250
  Placement = pos=(19730,1020,0) rot=(0,0,1;0rad)
  expr: Placement.Base.y = Part236.Placement.Base.y - 4cm
  expr: Placement.Base.x = Part246.Placement.Base.x
FEATURE [App::Part] Part255  label="contenido085"
  Group = -> [Circle098,Line196,Line197]
  Origin = -> Origin255
  Placement = pos=(0,0,0) rot=(0,0,1;0.785398rad)
FEATURE [Part::Part2DObjectPython] Circle102  # Draft 2D object (typed FeaturePython)
  FirstAngle = 0
  LastAngle = 0
  MakeFace = true
  Radius = 50
FEATURE [Part::Part2DObjectPython] Circle103  # Draft 2D object (typed FeaturePython)
  FirstAngle = 0
  LastAngle = 0
  MakeFace = true
  Radius = 50
FEATURE [Part::Part2DObjectPython] Line200  # Draft 2D object (typed FeaturePython)
  ChamferSize = 0
  Closed = false
  End = (0,-100,0)
  FilletRadius = 0
  Length = 200
  MakeFace = true
  Placement = pos=(0,100,0) rot=(0,0,1;0rad)
  Points = (2) [(0,0,0),(0,-200,0)]
  Start = (0,100,0)
  Subdivisions = 0
FEATURE [Part::Part2DObjectPython] Line201  # Draft 2D object (typed FeaturePython)
  ChamferSize = 0
  Closed = false
  End = (-100,3.8e-15,0)
  FilletRadius = 0
  Length = 200
  MakeFace = true
  Placement = pos=(100,1.8e-14,0) rot=(0,0,1;0rad)
  Points = (2) [(0,0,0),(-200,-1.42109e-14,0)]
  Start = (100,1.8e-14,0)
  Subdivisions = 0
FEATURE [App::Part] Part274  label="cbk__004"
  Group = -> [InternalObjectName095]
  Origin = -> Origin274
FEATURE [Part::Part2DObjectPython] Arc004  # Draft 2D object (typed FeaturePython)
  FirstAngle = -90
  LastAngle = 90
  MakeFace = true
  Placement = pos=(20,0,0) rot=(0,0,1;0rad)
  Radius = 10
FEATURE [App::Part] Part273  label="cbk__003"
  Group = -> [InternalObjectName094]
  Origin = -> Origin273
FEATURE [App::Part] Part270  label="cbk__001"
  Group = -> [InternalObjectName091]
  Origin = -> Origin270
FEATURE [Part::Part2DObjectPython] Line203  # Draft 2D object (typed FeaturePython)
  ChamferSize = 0
  Closed = false
  End = (-100,3.8e-15,0)
  FilletRadius = 0
  Length = 200
  MakeFace = true
  Placement = pos=(100,1.8e-14,0) rot=(0,0,1;0rad)
  Points = (2) [(0,0,0),(-200,-1.42109e-14,0)]
  Start = (100,1.8e-14,0)
  Subdivisions = 0
FEATURE [Part::Part2DObjectPython] Circle101  # Draft 2D object (typed FeaturePython)
  FirstAngle = 0
  LastAngle = 0
  MakeFace = true
  Radius = 100
FEATURE [App::Part] Part261  label="contenido088"
  Group = -> [Circle101,Line202,Line203]
  Origin = -> Origin261
  Placement = pos=(0,0,0) rot=(0,0,1;0.785398rad)
FEATURE [Part::Part2DObjectPython] Arc005  # Draft 2D object (typed FeaturePython)
  FirstAngle = -90
  LastAngle = 90
  MakeFace = true
  Placement = pos=(10,0,0) rot=(0,0,1;0rad)
  Radius = 10
FEATURE [App::Part] Part257  label="contenido086"
  Group = -> [Circle099,Line198,Line199]
  Origin = -> Origin257
  Placement = pos=(0,0,0) rot=(0,0,1;0.785398rad)
FEATURE [App::Part] Part256  label="luz_8in__032"
  Group = -> [InternalObjectName083,Part257,ShapeString052]
  Origin = -> Origin256
  Placement = pos=(21000,3087,0) rot=(0,0,1;0rad)
  expr: Placement.Base.y = Part246.Placement.Base.y
  expr: Placement.Base.x = Part252.Placement.Base.x
FEATURE [Part::Part2DObjectPython] Circle104  # Draft 2D object (typed FeaturePython)
  FirstAngle = 0
  LastAngle = 0
  MakeFace = true
  Radius = 50
FEATURE [App::Part] Part267  label="contenido090"
  Group = -> [Circle104,Text009]
  Origin = -> Origin267
FEATURE [App::Part] Part275  label="cbk__005"
  Group = -> [InternalObjectName096]
  Origin = -> Origin275
FEATURE [Part::Part2DObjectPython] Line206  # Draft 2D object (typed FeaturePython)
  ChamferSize = 0
  Closed = false
  End = (-40,0,0)
  FilletRadius = 0
  Length = 10
  MakeFace = true
  Placement = pos=(-30,0,0) rot=(0,0,1;0rad)
  Points = (2) [(0,0,0),(-10,0,0)]
  Start = (-30,0,0)
  Subdivisions = 0
FEATURE [Part::Part2DObjectPython] Circle100  # Draft 2D object (typed FeaturePython)
  FirstAngle = 0
  LastAngle = 0
  MakeFace = true
  Radius = 100
FEATURE [Part::Part2DObjectPython] Circle105  # Draft 2D object (typed FeaturePython)
  FirstAngle = 0
  LastAngle = 0
  MakeFace = true
  Radius = 50
FEATURE [App::Part] Part283  label="cbk__013"
  Group = -> [InternalObjectName104]
  Origin = -> Origin283
FEATURE [Part::Part2DObjectPython] Line204  # Draft 2D object (typed FeaturePython)
  ChamferSize = 0
  Closed = false
  End = (-10,0,0)
  FilletRadius = 0
  Length = 10
  MakeFace = true
  Placement = pos=(-20,0,0) rot=(0,0,1;0rad)
  Points = (2) [(0,0,0),(10,0,0)]
  Start = (-20,0,0)
  Subdivisions = 0
FEATURE [App::Part] Part259  label="contenido087"
  Group = -> [Circle100,Line200,Line201]
  Origin = -> Origin259
  Placement = pos=(0,0,0) rot=(0,0,1;0.785398rad)
FEATURE [App::Part] Part271  label="cbk__002"
  Group = -> [InternalObjectName092]
  Origin = -> Origin271
FEATURE [App::Part] Part280  label="cbk__010"
  Group = -> [InternalObjectName101]
  Origin = -> Origin280
FEATURE [App::Part] Part284  label="cbk__014"
  Group = -> [InternalObjectName105]
  Origin = -> Origin284
FEATURE [App::Part] Part265  label="contenido089"
  Group = -> [Circle103,Text005]
  Origin = -> Origin265
FEATURE [App::Part] Part289  label="cbk__019"
  Group = -> [InternalObjectName110]
  Origin = -> Origin289
FEATURE [Part::Part2DObjectPython] Rectangle010  # Draft 2D object (typed FeaturePython)
  ChamferSize = 0
  Columns = 1
  FilletRadius = 0
  Height = 1260
  Length = 1300
  MakeFace = false
  Placement = pos=(16003,0,0) rot=(0,0,1;0rad)
  Rows = 1
FEATURE [Part::Part2DObjectPython] Rectangle003  # Draft 2D object (typed FeaturePython)
  ChamferSize = 0
  Columns = 1
  FilletRadius = 0
  Height = 1655
  Length = 3880
  MakeFace = false
  Placement = pos=(3200,4330,0) rot=(0,0,1;0rad)
  Rows = 1
  expr: Placement.Base.x = Rectangle004.Placement.Base.x - 3.88m
FEATURE [App::Part] Part279  label="cbk__009"
  Group = -> [InternalObjectName100]
  Origin = -> Origin279
FEATURE [Part::Part2DObjectPython] Rectangle005  # Draft 2D object (typed FeaturePython)
  ChamferSize = 0
  Columns = 1
  FilletRadius = 0
  Height = 2440
  Length = 1970
  MakeFace = true
  Placement = pos=(10820,3570,0) rot=(0,0,1;0rad)
  Rows = 1
FEATURE [App::Part] Part288  label="cbk__018"
  Group = -> [InternalObjectName109]
  Origin = -> Origin288
FEATURE [App::Part] Part281  label="cbk__011"
  Group = -> [InternalObjectName102]
  Origin = -> Origin281
FEATURE [Part::Part2DObjectPython] Line035  # Draft 2D object (typed FeaturePython)
  ChamferSize = 0
  Closed = false
  End = (-48.9007,10,0)
  FilletRadius = 0
  Length = 128.901
  MakeFace = false
  Placement = pos=(80,10,0) rot=(0,0,1;0rad)
  Points = (2) [(0,0,0),(-128.901,-3.55271e-15,0)]
  Start = (80,10,0)
  Subdivisions = 0
FEATURE [App::Part] Part291  label="cbk2__001"
  Group = -> [InternalObjectName113]
  Origin = -> Origin291
FEATURE [Part::Part2DObjectPython] Rectangle004  # Draft 2D object (typed FeaturePython)
  ChamferSize = 0
  Columns = 1
  FilletRadius = 0
  Height = 1000
  Length = 2530
  MakeFace = false
  Placement = pos=(7080,3560,0) rot=(0,0,1;0rad)
  Rows = 1
FEATURE [App::Part] Part287  label="cbk__017"
  Group = -> [InternalObjectName108]
  Origin = -> Origin287
FEATURE [App::Part] Part290  label="cbk__020"
  Group = -> [InternalObjectName111]
  Origin = -> Origin290
FEATURE [Part::Part2DObjectPython] Rectangle008  # Draft 2D object (typed FeaturePython)
  ChamferSize = 0
  Columns = 1
  FilletRadius = 0
  Height = 2110
  Length = 130
  MakeFace = true
  Placement = pos=(15873,0,0) rot=(0,0,1;0rad)
  Rows = 1
FEATURE [App::Part] Part105  label="cbk2__"
  Group = -> [InternalObjectName112]
  Origin = -> Origin105
FEATURE [App::Part] Part277  label="cbk__007"
  Group = -> [InternalObjectName098]
  Origin = -> Origin277
FEATURE [App::Part] Part269  label="contenido091"
  Group = -> [Circle105,Text010]
  Origin = -> Origin269
FEATURE [Part::Part2DObjectPython] Rectangle  # Draft 2D object (typed FeaturePython)
  ChamferSize = 0
  Columns = 1
  FilletRadius = 0
  Height = 6037
  Length = 22250
  MakeFace = false
  Rows = 1
FEATURE [Part::Part2DObjectPython] Wire001  # Draft 2D object (typed FeaturePython)
  ChamferSize = 0
  Closed = true
  End = (300,100,0)
  FilletRadius = 0
  Length = 716.228
  MakeFace = true
  Points = (3) [(0,0,0),(300,9.18485e-15,0),(300,100,0)]
  Start = (0,0,0)
  Subdivisions = 0
FEATURE [App::Part] Part276  label="cbk__006"
  Group = -> [InternalObjectName097]
  Origin = -> Origin276
FEATURE [Part::Part2DObjectPython] Line205  # Draft 2D object (typed FeaturePython)
  ChamferSize = 0
  Closed = false
  End = (-20,10,0)
  FilletRadius = 0
  Length = 14.1421
  MakeFace = true
  Placement = pos=(-30,0,0) rot=(0,0,1;0rad)
  Points = (2) [(0,0,0),(10,10,0)]
  Start = (-30,0,0)
  Subdivisions = 0
FEATURE [App::Part] Part263  label="contenido011"
  Group = -> [Circle102,Arc004,Arc005,Line205,Line206,Line204,Point,Point001,Point002,Point003]
  Origin = -> Origin262
FEATURE [App::Part] Part262  label="sensor_movimiento_interruptor"
  Group = -> [Part263,InternalObjectName087,ShapeString014]
  Origin = -> Origin263
  Placement = pos=(8733,2730,0) rot=(0,0,1;0rad)
  expr: Placement.Base.y = Part218.Placement.Base.y - 23cm
  expr: Placement.Base.x = Part218.Placement.Base.x
FEATURE [Part::Part2DObjectPython] Rectangle006  # Draft 2D object (typed FeaturePython)
  ChamferSize = 0
  Columns = 1
  FilletRadius = 0
  Height = 2370
  Length = 133
  MakeFace = true
  Placement = pos=(8220,0,0) rot=(0,0,1;0rad)
  Rows = 1
FEATURE [App::Part] Part282  label="cbk__012"
  Group = -> [InternalObjectName103]
  Origin = -> Origin282
FEATURE [App::Part] Part286  label="cbk__016"
  Group = -> [InternalObjectName107]
  Origin = -> Origin286
FEATURE [App::Part] Part292  label="cbk2__002"
  Group = -> [InternalObjectName114]
  Origin = -> Origin292
FEATURE [App::Part] Part294  label="cbk2__004"
  Group = -> [InternalObjectName116]
  Origin = -> Origin294
FEATURE [App::Part] Part278  label="cbk__008"
  Group = -> [InternalObjectName099]
  Origin = -> Origin278
FEATURE [App::Part] Part285  label="cbk__015"
  Group = -> [InternalObjectName106]
  Origin = -> Origin285
FEATURE [App::Part] Part293  label="cbk2__003"
  Group = -> [InternalObjectName115]
  Origin = -> Origin293
FEATURE [Part::Part2DObjectPython] Rectangle002  # Draft 2D object (typed FeaturePython)
  ChamferSize = 0
  Columns = 1
  FilletRadius = 0
  Height = 1650
  Length = 2400
  MakeFace = true
  Rows = 1
FEATURE [Part::Part2DObjectPython] Rectangle011  # Draft 2D object (typed FeaturePython)
  ChamferSize = 0
  Columns = 1
  FilletRadius = 0
  Height = 280
  Length = 3740
  MakeFace = true
  Placement = pos=(7080,5757,0) rot=(0,0,1;0rad)
  Rows = 1
  expr: Placement.Base.y = Rectangle.Placement.Base.y + Rectangle.Height - Rectangle011.Height
  expr: Placement.Base.x = Rectangle003.Placement.Base.x + Rectangle003.Length
  expr: Length = Rectangle005.Placement.Base.x - (Rectangle003.Placement.Base.x + Rectangle003.Length)
FEATURE [Part::Part2DObjectPython] Rectangle007  # Draft 2D object (typed FeaturePython)
  ChamferSize = 0
  Columns = 1
  FilletRadius = 0
  Height = 2730
  Length = 123
  MakeFace = true
  Placement = pos=(17220,3307,0) rot=(0,0,1;0rad)
  Rows = 1
FEATURE [App::DocumentObjectGroup] Group001  label="piso1_arq_inicial"
  Group = -> [Rectangle002,Rectangle003,Rectangle004,Rectangle005,Rectangle006,Rectangle007,Rectangle008,Rectangle010,Rectangle011]
FEATURE [App::Part] Part001  label="region_trabajo"
  Group = -> [Rectangle,Dimension024,Dimension025]
  Origin = -> Origin001
FEATURE [Part::Part2DObjectPython] Rectangle025  # Draft 2D object (typed FeaturePython)
  ChamferSize = 0
  Columns = 1
  FilletRadius = 0
  Height = 140
  Length = 380
  MakeFace = true
  Placement = pos=(16003,1120,0) rot=(0,0,1;0rad)
  Rows = 1
FEATURE [Part::Part2DObjectPython] Circle054  # Draft 2D object (typed FeaturePython)
  FirstAngle = 0
  LastAngle = 0
  MakeFace = false
  Radius = 50
FEATURE [Part::Part2DObjectPython] Rectangle024  # Draft 2D object (typed FeaturePython)
  ChamferSize = 0
  Columns = 1
  FilletRadius = 0
  Height = 1260
  Length = 110
  MakeFace = true
  Placement = pos=(17193,0,0) rot=(0,0,1;0rad)
  Rows = 1
  expr: Height = Rectangle010.Height
  expr: Placement.Base.y = Rectangle.Placement.Base.x
  expr: Placement.Base.x = Rectangle010.Placement.Base.x + Rectangle010.Length - Rectangle024.Length
FEATURE [Part::Part2DObjectPython] Circle056  # Draft 2D object (typed FeaturePython)
  FirstAngle = 0
  LastAngle = 0
  MakeFace = false
  Radius = 50
FEATURE [Part::Part2DObjectPython] Line066  # Draft 2D object (typed FeaturePython)
  ChamferSize = 0
  Closed = false
  End = (100,100,0)
  FilletRadius = 0
  Length = 91.7357
  MakeFace = false
  Placement = pos=(35.1355,35.1306,0) rot=(0,0,1;0rad)
  Points = (2) [(0,0,0),(64.8645,64.8694,0)]
  Start = (35.1355,35.1306,0)
  Subdivisions = 0
FEATURE [Part::Part2DObjectPython] Circle059  # Draft 2D object (typed FeaturePython)
  FirstAngle = 0
  LastAngle = 0
  MakeFace = false
  Radius = 50
FEATURE [Part::Part2DObjectPython] Line064  # Draft 2D object (typed FeaturePython)
  ChamferSize = 0
  Closed = false
  End = (-48.8237,-10,0)
  FilletRadius = 0
  Length = 128.824
  MakeFace = false
  Placement = pos=(80,-10,0) rot=(0,0,1;0rad)
  Points = (2) [(0,-5.32907e-15,0),(-128.824,-3.55271e-15,0)]
  Start = (80,-10,0)
  Subdivisions = 0
FEATURE [Part::Part2DObjectPython] Circle032  # Draft 2D object (typed FeaturePython)
  FirstAngle = 0
  LastAngle = 0
  MakeFace = false
  Radius = 50
FEATURE [Part::Part2DObjectPython] Line065  # Draft 2D object (typed FeaturePython)
  ChamferSize = 0
  Closed = false
  End = (-48.9007,10,0)
  FilletRadius = 0
  Length = 128.901
  MakeFace = false
  Placement = pos=(80,10,0) rot=(0,0,1;0rad)
  Points = (2) [(0,0,0),(-128.901,-3.55271e-15,0)]
  Start = (80,10,0)
  Subdivisions = 0
FEATURE [Part::Part2DObjectPython] Circle057  # Draft 2D object (typed FeaturePython)
  FirstAngle = 0
  LastAngle = 0
  MakeFace = false
  Radius = 50
FEATURE [App::Part] Part164  label="contenido041"
  Group = -> [Circle032,Line065,Line064]
  Origin = -> Origin165
FEATURE [Part::Part2DObjectPython] Line069  # Draft 2D object (typed FeaturePython)
  ChamferSize = 0
  Closed = false
  End = (100,100,0)
  FilletRadius = 0
  Length = 91.7357
  MakeFace = false
  Placement = pos=(35.1355,35.1306,0) rot=(0,0,1;0rad)
  Points = (2) [(0,0,0),(64.8645,64.8694,0)]
  Start = (35.1355,35.1306,0)
  Subdivisions = 0
FEATURE [App::Part] Part170  label="contenido043"
  Group = -> [Line069,Circle057]
  Origin = -> Origin170
FEATURE [Part::Part2DObjectPython] Line062  # Draft 2D object (typed FeaturePython)
  ChamferSize = 0
  Closed = false
  End = (-48.8237,-10,0)
  FilletRadius = 0
  Length = 128.824
  MakeFace = false
  Placement = pos=(80,-10,0) rot=(0,0,1;0rad)
  Points = (2) [(0,-5.32907e-15,0),(-128.824,-3.55271e-15,0)]
  Start = (80,-10,0)
  Subdivisions = 0
FEATURE [Part::Part2DObjectPython] Circle029  # Draft 2D object (typed FeaturePython)
  FirstAngle = 0
  LastAngle = 0
  MakeFace = false
  Radius = 50
FEATURE [Part::Part2DObjectPython] Line061  # Draft 2D object (typed FeaturePython)
  ChamferSize = 0
  Closed = false
  End = (-48.8237,-10,0)
  FilletRadius = 0
  Length = 128.824
  MakeFace = false
  Placement = pos=(80,-10,0) rot=(0,0,1;0rad)
  Points = (2) [(0,-5.32907e-15,0),(-128.824,-3.55271e-15,0)]
  Start = (80,-10,0)
  Subdivisions = 0
FEATURE [Part::Part2DObjectPython] Circle031  # Draft 2D object (typed FeaturePython)
  FirstAngle = 0
  LastAngle = 0
  MakeFace = false
  Radius = 50
FEATURE [Part::Part2DObjectPython] Line068  # Draft 2D object (typed FeaturePython)
  ChamferSize = 0
  Closed = false
  End = (100,100,0)
  FilletRadius = 0
  Length = 91.7357
  MakeFace = false
  Placement = pos=(35.1355,35.1306,0) rot=(0,0,1;0rad)
  Points = (2) [(0,0,0),(64.8645,64.8694,0)]
  Start = (35.1355,35.1306,0)
  Subdivisions = 0
FEATURE [App::Part] Part168  label="contenido042"
  Group = -> [Line068,Circle056]
  Origin = -> Origin167
FEATURE [App::Part] Part167  label="interruptor_sencillo__001"
  Group = -> [InternalObjectName036,Part168,ShapeString004]
  Origin = -> Origin168
  Placement = pos=(3910,5935,0) rot=(0,0,1;3.14159rad)
  expr: Placement.Base.x = Rectangle013.Placement.Base.x - 0.33m
  expr: Placement.Base.y = Rectangle003.Placement.Base.y + Rectangle003.Height - 50mm
FEATURE [Part::Part2DObjectPython] Circle028  # Draft 2D object (typed FeaturePython)
  FirstAngle = 0
  LastAngle = 0
  MakeFace = false
  Radius = 50
FEATURE [Part::Part2DObjectPython] Line067  # Draft 2D object (typed FeaturePython)
  ChamferSize = 0
  Closed = false
  End = (100,100,0)
  FilletRadius = 0
  Length = 91.7357
  MakeFace = false
  Placement = pos=(35.1355,35.1306,0) rot=(0,0,1;0rad)
  Points = (2) [(0,0,0),(64.8645,64.8694,0)]
  Start = (35.1355,35.1306,0)
  Subdivisions = 0
FEATURE [Part::Part2DObjectPython] Circle060  # Draft 2D object (typed FeaturePython)
  FirstAngle = 0
  LastAngle = 0
  MakeFace = false
  Radius = 50
FEATURE [Part::Part2DObjectPython] Circle061  # Draft 2D object (typed FeaturePython)
  FirstAngle = 0
  LastAngle = 0
  MakeFace = false
  Radius = 50
FEATURE [Part::Part2DObjectPython] Circle055  # Draft 2D object (typed FeaturePython)
  FirstAngle = 0
  LastAngle = 0
  MakeFace = false
  Radius = 50
FEATURE [App::Part] Part094  label="contenido003"
  Group = -> [Line067,Text003,Circle055]
  Origin = -> Origin094
FEATURE [Part::Part2DObjectPython] ShapeString042  label="rotulo_dibujo_tecnico__042"  # Draft 2D object (typed FeaturePython)
  FontFile = <path>
  Placement = pos=(0,100,0) rot=(0,0,1;0rad)
  Size = 50
  String = 11
  Tracking = 0
FEATURE [App::Part] Part236  label="luz_8in__022"
  Group = -> [InternalObjectName073,Part237,ShapeString042]
  Origin = -> Origin236
  Placement = pos=(18010,1060,0) rot=(0,0,1;0rad)
  expr: Placement.Base.x = Rectangle007.Placement.Base.x + 79cm
  expr: Placement.Base.y = Rectangle.Placement.Base.x + 106cm
FEATURE [Part::Part2DObjectPython] ShapeString050  label="rotulo_dibujo_tecnico__050"  # Draft 2D object (typed FeaturePython)
  FontFile = <path>
  Placement = pos=(0,100,0) rot=(0,0,1;0rad)
  Size = 50
  String = 4
  Tracking = 0
FEATURE [App::Part] Part252  label="luz_8in__030"
  Group = -> [InternalObjectName081,Part253,ShapeString050]
  Origin = -> Origin252
  Placement = pos=(21000,5157,0) rot=(0,0,1;0rad)
  expr: Placement.Base.y = Part242.Placement.Base.y
  expr: Placement.Base.x = Part242.Placement.Base.x + 127cm
FEATURE [Part::Part2DObjectPython] Line017  # Draft 2D object (typed FeaturePython)
  ChamferSize = 0
  Closed = false
  End = (-48.9007,10,0)
  FilletRadius = 0
  Length = 128.901
  MakeFace = false
  Placement = pos=(80,10,0) rot=(0,0,1;0rad)
  Points = (2) [(0,0,0),(-128.901,-3.55271e-15,0)]
  Start = (80,10,0)
  Subdivisions = 0
FEATURE [Part::Part2DObjectPython] Line003  # Draft 2D object (typed FeaturePython)
  ChamferSize = 0
  Closed = false
  End = (-48.8237,-10,0)
  FilletRadius = 0
  Length = 128.824
  MakeFace = false
  Placement = pos=(80,-10,0) rot=(0,0,1;0rad)
  Points = (2) [(0,-5.32907e-15,0),(-128.824,-3.55271e-15,0)]
  Start = (80,-10,0)
  Subdivisions = 0
FEATURE [Part::Part2DObjectPython] Line071  # Draft 2D object (typed FeaturePython)
  ChamferSize = 0
  Closed = false
  End = (100,100,0)
  FilletRadius = 0
  Length = 91.7357
  MakeFace = false
  Placement = pos=(35.1355,35.1306,0) rot=(0,0,1;0rad)
  Points = (2) [(0,0,0),(64.8645,64.8694,0)]
  Start = (35.1355,35.1306,0)
  Subdivisions = 0
FEATURE [App::Part] Part174  label="contenido045"
  Group = -> [Line071,Circle059]
  Origin = -> Origin173
FEATURE [App::Part] Part173  label="interruptor_sencillo__004"
  Group = -> [InternalObjectName039,Part174,ShapeString007]
  Origin = -> Origin174
  Placement = pos=(8605,3510,0) rot=(0,0,1;3.14159rad)
  expr: Placement.Base.x = Rectangle019.Placement.Base.x + Rectangle019.Length / 2
  expr: Placement.Base.y = Rectangle019.Placement.Base.y - 50mm
FEATURE [Part::Part2DObjectPython] ShapeString001  label="rotulo_dibujo_tecnico__001"  # Draft 2D object (typed FeaturePython)
  FontFile = <path>
  Placement = pos=(0,100,0) rot=(0,0,1;0rad)
  Size = 100
  String = 1
  Tracking = 0
FEATURE [Part::Part2DObjectPython] Line073  # Draft 2D object (typed FeaturePython)
  ChamferSize = 0
  Closed = false
  End = (100,100,0)
  FilletRadius = 0
  Length = 91.7357
  MakeFace = false
  Placement = pos=(35.1355,35.1306,0) rot=(0,0,1;0rad)
  Points = (2) [(0,0,0),(64.8645,64.8694,0)]
  Start = (35.1355,35.1306,0)
  Subdivisions = 0
FEATURE [App::Part] Part178  label="contenido047"
  Group = -> [Line073,Circle061]
  Origin = -> Origin177
FEATURE [Part::Part2DObjectPython] Circle010  # Draft 2D object (typed FeaturePython)
  FirstAngle = 0
  LastAngle = 0
  MakeFace = false
  Radius = 50
FEATURE [Part::Part2DObjectPython] ShapeString015  label="rotulo_dibujo_tecnico__015"  # Draft 2D object (typed FeaturePython)
  FontFile = <path>
  Placement = pos=(0,100,0) rot=(0,0,1;0rad)
  Size = 50
  String = 32
  Tracking = 0
FEATURE [App::Part] Part021  label="luz_8in__"
  Group = -> [InternalObjectName046,Part095,ShapeString015]
  Origin = -> Origin021
  Placement = pos=(660,2760,0) rot=(0,0,1;0.785398rad)
  expr: Placement.Base.x = Rectangle.Placement.Base.x + 66cm
FEATURE [Part::Part2DObjectPython] Circle058  # Draft 2D object (typed FeaturePython)
  FirstAngle = 0
  LastAngle = 0
  MakeFace = false
  Radius = 50
FEATURE [App::Part] Part092  label="contenido001"
  Group = -> [Line066,Circle054]
  Origin = -> Origin092
FEATURE [App::Part] Part166  label="interruptor_sencillo__"
  Group = -> [InternalObjectName004,Part092,ShapeString002]
  Origin = -> Origin166
  Placement = pos=(1970,1700,0) rot=(0,0,1;0rad)
  expr: Placement.Base.x = Rectangle002.Placement.Base.x + Rectangle002.Length - 430mm
  expr: Placement.Base.y = Rectangle002.Placement.Base.y + Rectangle002.Height + 50mm
FEATURE [Part::Part2DObjectPython] Line070  # Draft 2D object (typed FeaturePython)
  ChamferSize = 0
  Closed = false
  End = (100,100,0)
  FilletRadius = 0
  Length = 91.7357
  MakeFace = false
  Placement = pos=(35.1355,35.1306,0) rot=(0,0,1;0rad)
  Points = (2) [(0,0,0),(64.8645,64.8694,0)]
  Start = (35.1355,35.1306,0)
  Subdivisions = 0
FEATURE [App::Part] Part172  label="contenido044"
  Group = -> [Line070,Circle058]
  Origin = -> Origin172
FEATURE [Part::Part2DObjectPython] Line018  # Draft 2D object (typed FeaturePython)
  ChamferSize = 0
  Closed = false
  End = (-48.8237,-10,0)
  FilletRadius = 0
  Length = 128.824
  MakeFace = false
  Placement = pos=(80,-10,0) rot=(0,0,1;0rad)
  Points = (2) [(0,-5.32907e-15,0),(-128.824,-3.55271e-15,0)]
  Start = (80,-10,0)
  Subdivisions = 0
FEATURE [Part::Part2DObjectPython] ShapeString032  label="rotulo_dibujo_tecnico__032"  # Draft 2D object (typed FeaturePython)
  FontFile = <path>
  Placement = pos=(0,100,0) rot=(0,0,1;0rad)
  Size = 50
  String = 28
  Tracking = 0
FEATURE [Part::Part2DObjectPython] Line072  # Draft 2D object (typed FeaturePython)
  ChamferSize = 0
  Closed = false
  End = (100,100,0)
  FilletRadius = 0
  Length = 91.7357
  MakeFace = false
  Placement = pos=(35.1355,35.1306,0) rot=(0,0,1;0rad)
  Points = (2) [(0,0,0),(64.8645,64.8694,0)]
  Start = (35.1355,35.1306,0)
  Subdivisions = 0
FEATURE [App::Part] Part176  label="contenido046"
  Group = -> [Line072,Circle060]
  Origin = -> Origin175
FEATURE [Part::Part2DObjectPython] ShapeString053  label="rotulo_dibujo_tecnico__053"  # Draft 2D object (typed FeaturePython)
  FontFile = <path>
  Placement = pos=(0,100,0) rot=(0,0,1;0rad)
  Size = 50
  String = 5
  Tracking = 0
FEATURE [App::Part] Part258  label="luz_8in__033"
  Group = -> [InternalObjectName084,Part259,ShapeString053]
  Origin = -> Origin258
  Placement = pos=(21000,2057,0) rot=(0,0,1;0rad)
  expr: Placement.Base.y = Part248.Placement.Base.y
  expr: Placement.Base.x = Part252.Placement.Base.x
FEATURE [Part::Part2DObjectPython] Line023  # Draft 2D object (typed FeaturePython)
  ChamferSize = 0
  Closed = false
  End = (-48.9007,10,0)
  FilletRadius = 0
  Length = 128.901
  MakeFace = false
  Placement = pos=(80,10,0) rot=(0,0,1;0rad)
  Points = (2) [(0,0,0),(-128.901,-3.55271e-15,0)]
  Start = (80,10,0)
  Subdivisions = 0
FEATURE [App::Part] Part018  label="interruptor_doble__"
  Group = -> [InternalObjectName035,Part094,ShapeString003]
  Origin = -> Origin018
  Placement = pos=(1820,1700,0) rot=(0,0,1;0rad)
  expr: Placement.Base.y = Rectangle002.Placement.Base.y + Rectangle002.Height + 50mm
FEATURE [Part::Part2DObjectPython] Circle012  # Draft 2D object (typed FeaturePython)
  FirstAngle = 0
  LastAngle = 0
  MakeFace = false
  Radius = 50
FEATURE [Part::Part2DObjectPython] Line026  # Draft 2D object (typed FeaturePython)
  ChamferSize = 0
  Closed = false
  End = (-48.8237,-10,0)
  FilletRadius = 0
  Length = 128.824
  MakeFace = false
  Placement = pos=(80,-10,0) rot=(0,0,1;0rad)
  Points = (2) [(0,-5.32907e-15,0),(-128.824,-3.55271e-15,0)]
  Start = (80,-10,0)
  Subdivisions = 0
FEATURE [Part::Part2DObjectPython] Line024  # Draft 2D object (typed FeaturePython)
  ChamferSize = 0
  Closed = false
  End = (-48.8237,-10,0)
  FilletRadius = 0
  Length = 128.824
  MakeFace = false
  Placement = pos=(80,-10,0) rot=(0,0,1;0rad)
  Points = (2) [(0,-5.32907e-15,0),(-128.824,-3.55271e-15,0)]
  Start = (80,-10,0)
  Subdivisions = 0
FEATURE [Part::Part2DObjectPython] Circle013  # Draft 2D object (typed FeaturePython)
  FirstAngle = 0
  LastAngle = 0
  MakeFace = false
  Radius = 50
FEATURE [Part::Part2DObjectPython] Circle009  # Draft 2D object (typed FeaturePython)
  FirstAngle = 0
  LastAngle = 0
  MakeFace = false
  Radius = 50
FEATURE [Part::Part2DObjectPython] Line025  # Draft 2D object (typed FeaturePython)
  ChamferSize = 0
  Closed = false
  End = (-48.9007,10,0)
  FilletRadius = 0
  Length = 128.901
  MakeFace = false
  Placement = pos=(80,10,0) rot=(0,0,1;0rad)
  Points = (2) [(0,0,0),(-128.901,-3.55271e-15,0)]
  Start = (80,10,0)
  Subdivisions = 0
FEATURE [Part::Part2DObjectPython] Wire002  # Draft 2D object (typed FeaturePython)
  ChamferSize = 0
  Closed = true
  End = (300,100,0)
  FilletRadius = 0
  Length = 716.228
  MakeFace = true
  Points = (3) [(0,0,0),(3.06162e-15,100,0),(300,100,0)]
  Start = (0,0,0)
  Subdivisions = 0
FEATURE [App::Part] Part136  label="tomacorriente__018"
  Group = -> [InternalObjectName020,Part137,ShapeString075]
  Origin = -> Origin137
  Placement = pos=(20640,5987,0) rot=(0,0,1;0rad)
  expr: Placement.Base.y = Rectangle.Placement.Base.y + Rectangle.Height - 50mm
FEATURE [Part::Part2DObjectPython] Line021  # Draft 2D object (typed FeaturePython)
  ChamferSize = 0
  Closed = false
  End = (-48.9007,10,0)
  FilletRadius = 0
  Length = 128.901
  MakeFace = false
  Placement = pos=(80,10,0) rot=(0,0,1;0rad)
  Points = (2) [(0,0,0),(-128.901,-3.55271e-15,0)]
  Start = (80,10,0)
  Subdivisions = 0
FEATURE [Part::Part2DObjectPython] Line027  # Draft 2D object (typed FeaturePython)
  ChamferSize = 0
  Closed = false
  End = (-48.9007,10,0)
  FilletRadius = 0
  Length = 128.901
  MakeFace = false
  Placement = pos=(80,10,0) rot=(0,0,1;0rad)
  Points = (2) [(0,0,0),(-128.901,-3.55271e-15,0)]
  Start = (80,10,0)
  Subdivisions = 0
FEATURE [App::Part] Part127  label="contenido022"
  Group = -> [Circle013,Line027,Line026]
  Origin = -> Origin127
FEATURE [App::Part] Part126  label="tomacorriente__013"
  Group = -> [InternalObjectName015,Part127,ShapeString070]
  Origin = -> Origin126
  Placement = pos=(13390,5983,0) rot=(0,0,1;0rad)
  expr: Placement.Base.x = Rectangle005.Placement.Base.x + Rectangle005.Length + 0.6m
FEATURE [Part::Part2DObjectPython] Line029  # Draft 2D object (typed FeaturePython)
  ChamferSize = 0
  Closed = false
  End = (-48.8237,-10,0)
  FilletRadius = 0
  Length = 128.824
  MakeFace = false
  Placement = pos=(80,-10,0) rot=(0,0,1;0rad)
  Points = (2) [(0,-5.32907e-15,0),(-128.824,-3.55271e-15,0)]
  Start = (80,-10,0)
  Subdivisions = 0
FEATURE [Part::Part2DObjectPython] Line022  # Draft 2D object (typed FeaturePython)
  ChamferSize = 0
  Closed = false
  End = (-48.8237,-10,0)
  FilletRadius = 0
  Length = 128.824
  MakeFace = false
  Placement = pos=(80,-10,0) rot=(0,0,1;0rad)
  Points = (2) [(0,-5.32907e-15,0),(-128.824,-3.55271e-15,0)]
  Start = (80,-10,0)
  Subdivisions = 0
FEATURE [Part::Part2DObjectPython] Line034  # Draft 2D object (typed FeaturePython)
  ChamferSize = 0
  Closed = false
  End = (-48.8237,-10,0)
  FilletRadius = 0
  Length = 128.824
  MakeFace = false
  Placement = pos=(80,-10,0) rot=(0,0,1;0rad)
  Points = (2) [(0,-5.32907e-15,0),(-128.824,-3.55271e-15,0)]
  Start = (80,-10,0)
  Subdivisions = 0
FEATURE [App::Part] Part135  label="contenido026"
  Group = -> [Circle017,Line035,Line034]
  Origin = -> Origin135
FEATURE [Part::Part2DObjectPython] Line038  # Draft 2D object (typed FeaturePython)
  ChamferSize = 0
  Closed = false
  End = (-48.9007,10,0)
  FilletRadius = 0
  Length = 128.901
  MakeFace = false
  Placement = pos=(80,10,0) rot=(0,0,1;0rad)
  Points = (2) [(0,0,0),(-128.901,-3.55271e-15,0)]
  Start = (80,10,0)
  Subdivisions = 0
FEATURE [App::Part] Part139  label="contenido028"
  Group = -> [Circle019,Line038,Line039]
  Origin = -> Origin138
FEATURE [App::Part] Part138  label="tomacorriente__019"
  Group = -> [InternalObjectName021,Part139,ShapeString076]
  Origin = -> Origin139
  Placement = pos=(20790,5987,0) rot=(0,0,1;0rad)
  expr: Placement.Base.y = Rectangle.Placement.Base.y + Rectangle.Height - 50mm
  expr: Placement.Base.x = Rectangle.Placement.Base.x + Rectangle.Length - 1.46m
FEATURE [Part::Part2DObjectPython] Circle008  # Draft 2D object (typed FeaturePython)
  FirstAngle = 0
  LastAngle = 0
  MakeFace = false
  Radius = 50
FEATURE [Part::Part2DObjectPython] Line019  # Draft 2D object (typed FeaturePython)
  ChamferSize = 0
  Closed = false
  End = (-48.9007,10,0)
  FilletRadius = 0
  Length = 128.901
  MakeFace = false
  Placement = pos=(80,10,0) rot=(0,0,1;0rad)
  Points = (2) [(0,0,0),(-128.901,-3.55271e-15,0)]
  Start = (80,10,0)
  Subdivisions = 0
FEATURE [App::Part] Part118  label="contenido018"
  Group = -> [Circle009,Line019,Line018]
  Origin = -> Origin118
FEATURE [Part::Part2DObjectPython] Circle011  # Draft 2D object (typed FeaturePython)
  FirstAngle = 0
  LastAngle = 0
  MakeFace = false
  Radius = 50
FEATURE [App::Part] Part122  label="contenido020"
  Group = -> [Circle011,Line023,Line022]
  Origin = -> Origin122
FEATURE [App::Part] Part123  label="tomacorriente__011"
  Group = -> [InternalObjectName013,Part122,ShapeString068]
  Origin = -> Origin123
  Placement = pos=(11460,54,0) rot=(0,0,1;0rad)
  expr: Placement.Base.x = Rectangle006.Placement.Base.x + 3.24m
FEATURE [Part::Part2DObjectPython] Line030  # Draft 2D object (typed FeaturePython)
  ChamferSize = 0
  Closed = false
  End = (-48.9007,10,0)
  FilletRadius = 0
  Length = 128.901
  MakeFace = false
  Placement = pos=(80,10,0) rot=(0,0,1;0rad)
  Points = (2) [(0,0,0),(-128.901,-3.55271e-15,0)]
  Start = (80,10,0)
  Subdivisions = 0
FEATURE [Part::Part2DObjectPython] Circle015  # Draft 2D object (typed FeaturePython)
  FirstAngle = 0
  LastAngle = 0
  MakeFace = false
  Radius = 50
FEATURE [App::Part] Part130  label="contenido024"
  Group = -> [Circle015,Line030,Line031]
  Origin = -> Origin130
FEATURE [Part::Part2DObjectPython] Circle014  # Draft 2D object (typed FeaturePython)
  FirstAngle = 0
  LastAngle = 0
  MakeFace = false
  Radius = 50
FEATURE [Part::Part2DObjectPython] Line147  # Draft 2D object (typed FeaturePython)
  ChamferSize = 0
  Closed = false
  End = (-100,3.8e-15,0)
  FilletRadius = 0
  Length = 200
  MakeFace = true
  Placement = pos=(100,1.8e-14,0) rot=(0,0,1;0rad)
  Points = (2) [(0,0,0),(-200,-1.42109e-14,0)]
  Start = (100,1.8e-14,0)
  Subdivisions = 0
FEATURE [Part::Part2DObjectPython] Line140  # Draft 2D object (typed FeaturePython)
  ChamferSize = 0
  Closed = false
  End = (0,-100,0)
  FilletRadius = 0
  Length = 200
  MakeFace = true
  Placement = pos=(0,100,0) rot=(0,0,1;0rad)
  Points = (2) [(0,0,0),(0,-200,0)]
  Start = (0,100,0)
  Subdivisions = 0
FEATURE [App::Part] Part198  label="contenido057"
  Group = -> [Circle070,Line140,Line141]
  Origin = -> Origin199
FEATURE [App::Part] Part199  label="luz_8in__004"
  Group = -> [InternalObjectName054,Part198,ShapeString019]
  Origin = -> Origin198
  Placement = pos=(5440,3260,0) rot=(0,0,1;0.785398rad)
  expr: Placement.Base.x = Rectangle.Placement.Base.x + 544cm
  expr: Placement.Base.y = Rectangle002.Placement.Base.y + Rectangle002.Height + 161cm
FEATURE [Part::Part2DObjectPython] Line151  # Draft 2D object (typed FeaturePython)
  ChamferSize = 0
  Closed = false
  End = (-100,3.8e-15,0)
  FilletRadius = 0
  Length = 200
  MakeFace = true
  Placement = pos=(100,1.8e-14,0) rot=(0,0,1;0rad)
  Points = (2) [(0,0,0),(-200,-1.42109e-14,0)]
  Start = (100,1.8e-14,0)
  Subdivisions = 0
FEATURE [Part::Part2DObjectPython] Line154  # Draft 2D object (typed FeaturePython)
  ChamferSize = 0
  Closed = false
  End = (0,-100,0)
  FilletRadius = 0
  Length = 200
  MakeFace = true
  Placement = pos=(0,100,0) rot=(0,0,1;0rad)
  Points = (2) [(0,0,0),(0,-200,0)]
  Start = (0,100,0)
  Subdivisions = 0
FEATURE [Part::Part2DObjectPython] Rectangle053  label="luz_60x60_cuerpo004"  # Draft 2D object (typed FeaturePython)
  ChamferSize = 0
  Columns = 1
  FilletRadius = 0
  Height = 600
  Length = 600
  MakeFace = true
  Rows = 1
FEATURE [App::Part] Part197  label="contenido056"
  Group = -> [Rectangle053]
  Origin = -> Origin197
FEATURE [App::Part] Part191  label="contenido"
  Group = -> [Rectangle050]
  Origin = -> Origin191
FEATURE [Part::Part2DObjectPython] Circle074  # Draft 2D object (typed FeaturePython)
  FirstAngle = 0
  LastAngle = 0
  MakeFace = true
  Radius = 100
FEATURE [Part::Part2DObjectPython] Circle078  # Draft 2D object (typed FeaturePython)
  FirstAngle = 0
  LastAngle = 0
  MakeFace = true
  Radius = 100
FEATURE [App::Part] Part213  label="contenido064"
  Group = -> [Circle077,Line154,Line155]
  Origin = -> Origin213
  Placement = pos=(0,0,0) rot=(0,0,1;0.785398rad)
FEATURE [App::Part] Part125  label="contenido021"
  Group = -> [Circle012,Line025,Line024]
  Origin = -> Origin125
FEATURE [Part::Part2DObjectPython] Circle076  # Draft 2D object (typed FeaturePython)
  FirstAngle = 0
  LastAngle = 0
  MakeFace = true
  Radius = 100
FEATURE [App::Part] Part211  label="contenido063"
  Group = -> [Circle076,Line152,Line153]
  Origin = -> Origin211
  Placement = pos=(0,0,0) rot=(0,0,1;0.785398rad)
FEATURE [App::Part] Part210  label="luz_8in__009"
  Group = -> [InternalObjectName060,Part211,ShapeString029]
  Origin = -> Origin210
  Placement = pos=(10043,810,0) rot=(0,0,1;0rad)
  expr: Placement.Base.x = Part208.Placement.Base.x + 131cm
  expr: Placement.Base.y = Rectangle.Placement.Base.y + 81cm
FEATURE [App::Part] Part205  label="contenido060"
  Group = -> [Circle073,Line146,Line147]
  Origin = -> Origin205
  Placement = pos=(0,0,0) rot=(0,0,1;0.785398rad)
FEATURE [App::Part] Part204  label="luz_8in__006"
  Group = -> [InternalObjectName057,Part205,ShapeString026]
  Origin = -> Origin204
  Placement = pos=(6360,5025,0) rot=(0,0,1;0rad)
  expr: Placement.Base.x = Rectangle015.Placement.Base.x + Rectangle015.Length + 56cm
  expr: Placement.Base.y = Rectangle017.Placement.Base.y - 89cm
FEATURE [Part::Part2DObjectPython] Line159  # Draft 2D object (typed FeaturePython)
  ChamferSize = 0
  Closed = false
  End = (-100,3.8e-15,0)
  FilletRadius = 0
  Length = 200
  MakeFace = true
  Placement = pos=(100,1.8e-14,0) rot=(0,0,1;0rad)
  Points = (2) [(0,0,0),(-200,-1.42109e-14,0)]
  Start = (100,1.8e-14,0)
  Subdivisions = 0
FEATURE [Part::Part2DObjectPython] Line150  # Draft 2D object (typed FeaturePython)
  ChamferSize = 0
  Closed = false
  End = (0,-100,0)
  FilletRadius = 0
  Length = 200
  MakeFace = true
  Placement = pos=(0,100,0) rot=(0,0,1;0rad)
  Points = (2) [(0,0,0),(0,-200,0)]
  Start = (0,100,0)
  Subdivisions = 0
FEATURE [Part::Part2DObjectPython] Circle079  # Draft 2D object (typed FeaturePython)
  FirstAngle = 0
  LastAngle = 0
  MakeFace = true
  Radius = 100
FEATURE [App::Part] Part217  label="contenido066"
  Group = -> [Circle079,Line158,Line159]
  Origin = -> Origin217
  Placement = pos=(0,0,0) rot=(0,0,1;0.785398rad)
FEATURE [App::Part] Part216  label="luz_8in__012"
  Group = -> [InternalObjectName063,Part217,ShapeString032]
  Origin = -> Origin216
  Placement = pos=(15363,810,0) rot=(0,0,1;0rad)
  expr: Placement.Base.x = Rectangle008.Placement.Base.x - 51cm
  expr: Placement.Base.y = Rectangle.Placement.Base.y + 81cm
FEATURE [App::Part] Part215  label="contenido065"
  Group = -> [Circle078,Line156,Line157]
  Origin = -> Origin215
  Placement = pos=(0,0,0) rot=(0,0,1;0.785398rad)
FEATURE [Part::Part2DObjectPython] Circle071  # Draft 2D object (typed FeaturePython)
  FirstAngle = 0
  LastAngle = 0
  MakeFace = true
  Radius = 82.5
FEATURE [Part::Part2DObjectPython] Line148  # Draft 2D object (typed FeaturePython)
  ChamferSize = 0
  Closed = false
  End = (0,-100,0)
  FilletRadius = 0
  Length = 200
  MakeFace = true
  Placement = pos=(0,100,0) rot=(0,0,1;0rad)
  Points = (2) [(0,0,0),(0,-200,0)]
  Start = (0,100,0)
  Subdivisions = 0
FEATURE [Part::Part2DObjectPython] Circle075  # Draft 2D object (typed FeaturePython)
  FirstAngle = 0
  LastAngle = 0
  MakeFace = true
  Radius = 100
FEATURE [App::Part] Part209  label="contenido062"
  Group = -> [Circle075,Line150,Line151]
  Origin = -> Origin209
  Placement = pos=(0,0,0) rot=(0,0,1;0.785398rad)
FEATURE [App::Part] Part208  label="luz_8in__008"
  Group = -> [InternalObjectName059,Part209,ShapeString028]
  Origin = -> Origin208
  Placement = pos=(8733,810,0) rot=(0,0,1;0rad)
  expr: Placement.Base.x = Rectangle006.Placement.Base.x + Rectangle006.Length + 38cm
  expr: Placement.Base.y = Rectangle.Placement.Base.y + 81cm
FEATURE [Part::Part2DObjectPython] Line143  # Draft 2D object (typed FeaturePython)
  ChamferSize = 0
  Closed = false
  End = (82.5,-6.51e-14,0)
  FilletRadius = 0
  Length = 165
  MakeFace = true
  Placement = pos=(-82.5,0,0) rot=(0,0,1;1.5708rad)
  Points = (2) [(0,0,0),(-2.84217e-14,-165,0)]
  Start = (-82.5,0,0)
  Subdivisions = 0
FEATURE [Part::Part2DObjectPython] Line142  # Draft 2D object (typed FeaturePython)
  ChamferSize = 0
  Closed = false
  End = (0,-82.5,0)
  FilletRadius = 0
  Length = 165
  MakeFace = true
  Placement = pos=(0,82.5,0) rot=(0,0,1;0rad)
  Points = (2) [(0,0,0),(0,-165,0)]
  Start = (0,82.5,0)
  Subdivisions = 0
FEATURE [App::Part] Part200  label="contenido058"
  Group = -> [Circle071,Line142,Line143]
  Origin = -> Origin201
  Placement = pos=(0,0,0) rot=(0,0,1;0.785398rad)
FEATURE [App::Part] Part201  label="luz_6.5in__"
  Group = -> [InternalObjectName055,Part200,ShapeString024]
  Origin = -> Origin200
  Placement = pos=(3875,5902.5,0) rot=(0,0,1;0rad)
  expr: Placement.Base.x = Rectangle013.Placement.Base.x - 36.5cm
  expr: Placement.Base.y = Rectangle003.Placement.Base.y + Rectangle003.Height - 82.5mm
FEATURE [Part::Part2DObjectPython] Line144  # Draft 2D object (typed FeaturePython)
  ChamferSize = 0
  Closed = false
  End = (0,-100,0)
  FilletRadius = 0
  Length = 200
  MakeFace = true
  Placement = pos=(0,100,0) rot=(0,0,1;0rad)
  Points = (2) [(0,0,0),(0,-200,0)]
  Start = (0,100,0)
  Subdivisions = 0
FEATURE [App::Part] Part203  label="contenido059"
  Group = -> [Circle072,Line144,Line145]
  Origin = -> Origin203
  Placement = pos=(0,0,0) rot=(0,0,1;0.785398rad)
FEATURE [App::Part] Part202  label="luz_8in__005"
  Group = -> [InternalObjectName056,Part203,ShapeString025]
  Origin = -> Origin202
  Placement = pos=(5000,5025,0) rot=(0,0,1;0rad)
  expr: Placement.Base.x = Rectangle015.Placement.Base.x - 63cm
  expr: Placement.Base.y = Rectangle017.Placement.Base.y - 89cm
FEATURE [App::Part] Part207  label="contenido061"
  Group = -> [Circle074,Line148,Line149]
  Origin = -> Origin207
  Placement = pos=(0,0,0) rot=(0,0,1;0.785398rad)
FEATURE [App::Part] Part206  label="luz_8in__007"
  Group = -> [InternalObjectName058,Part207,ShapeString027]
  Origin = -> Origin206
  Placement = pos=(8730,4190,0) rot=(0,0,1;0rad)
  expr: Placement.Base.x = Rectangle021.Placement.Base.x + Rectangle021.Length + 15cm
  expr: Placement.Base.y = Rectangle019.Placement.Base.y + Rectangle019.Height + 53cm
FEATURE [Part::Part2DObjectPython] ShapeString048  label="rotulo_dibujo_tecnico__048"  # Draft 2D object (typed FeaturePython)
  FontFile = <path>
  Placement = pos=(0,100,0) rot=(0,0,1;0rad)
  Size = 50
  String = 2
  Tracking = 0
FEATURE [App::Part] Part248  label="luz_8in__028"
  Group = -> [InternalObjectName079,Part249,ShapeString048]
  Origin = -> Origin248
  Placement = pos=(19730,2057,0) rot=(0,0,1;0rad)
  expr: Placement.Base.y = Part246.Placement.Base.y - 103cm
  expr: Placement.Base.x = Part246.Placement.Base.x
FEATURE [Part::Part2DObjectPython] ShapeString072  label="rotulo_dibujo_tecnico__072"  # Draft 2D object (typed FeaturePython)
  FontFile = <path>
  Placement = pos=(0,-150,0) rot=(0,0,1;0rad)
  Size = 50
  String = 6
  Tracking = 0
FEATURE [App::Part] Part131  label="tomacorriente__015"
  Group = -> [InternalObjectName017,Part130,ShapeString072]
  Origin = -> Origin131
  Placement = pos=(17392,4237,0) rot=(0,0,1;1.5708rad)
  expr: Placement.Base.y = Rectangle.Placement.Base.y + Rectangle.Height - 1.8m
  expr: Placement.Base.x = 17m
FEATURE [Part::Part2DObjectPython] ShapeString020  label="rotulo_dibujo_tecnico__020"  # Draft 2D object (typed FeaturePython)
  FontFile = <path>
  Placement = pos=(0,-100,0) rot=(0,0,1;0rad)
  Size = 50
  String = 21
  Tracking = 0
FEATURE [App::Part] Part089  label="luz_60x60__"
  Group = -> [InternalObjectName050,Part191,ShapeString020]
  Origin = -> Origin089
  Placement = pos=(3720,550,0) rot=(0,0,1;0rad)
  expr: Placement.Base.x = Rectangle006.Placement.Base.x - 30cm - 420cm
  expr: Placement.Base.y = Rectangle.Placement.Base.y - 30cm + 85cm
FEATURE [Part::Part2DObjectPython] ShapeString057  label="rotulo_dibujo_tecnico__057"  # Draft 2D object (typed FeaturePython)
  FontFile = <path>
  Placement = pos=(0,100,0) rot=(0,0,1;0rad)
  Size = 50
  String = 3
  Tracking = 0
FEATURE [App::Part] Part268  label="extractor_aire__002"
  Group = -> [Part269,InternalObjectName090,ShapeString057]
  Origin = -> Origin268
  Placement = pos=(17043,550,0) rot=(0,0,1;0rad)
  expr: Placement.Base.x = Rectangle024.Placement.Base.x - 15cm
  expr: Placement.Base.y = Rectangle.Placement.Base.y + 55cm
FEATURE [Part::Part2DObjectPython] ShapeString078  label="rotulo_dibujo_tecnico__078"  # Draft 2D object (typed FeaturePython)
  FontFile = <path>
  Placement = pos=(0,100,0) rot=(0,0,1;0rad)
  Size = 50
  String = 27
  Tracking = 0
FEATURE [App::Part] Part142  label="tomacorriente__021"
  Group = -> [InternalObjectName023,Part143,ShapeString078]
  Origin = -> Origin142
  Placement = pos=(20870,5987,0) rot=(0,0,1;0rad)
  expr: Placement.Base.y = Rectangle.Placement.Base.y + Rectangle.Height - 0.05m
  expr: Placement.Base.x = Rectangle.Placement.Base.x + Rectangle.Length - 1.38m
FEATURE [Part::Part2DObjectPython] ShapeString030  label="rotulo_dibujo_tecnico__030"  # Draft 2D object (typed FeaturePython)
  FontFile = <path>
  Placement = pos=(0,100,0) rot=(0,0,1;0rad)
  Size = 50
  String = 34
  Tracking = 0
FEATURE [App::Part] Part212  label="luz_8in__010"
  Group = -> [InternalObjectName061,Part213,ShapeString030]
  Origin = -> Origin212
  Placement = pos=(11503,810,0) rot=(0,0,1;0rad)
  expr: Placement.Base.x = Part210.Placement.Base.x + 146cm
  expr: Placement.Base.y = Rectangle.Placement.Base.y + 81cm
FEATURE [Part::Part2DObjectPython] ShapeString074  label="rotulo_dibujo_tecnico__074"  # Draft 2D object (typed FeaturePython)
  FontFile = <path>
  Placement = pos=(0,-150,0) rot=(0,0,1;0rad)
  Size = 50
  String = 1
  Tracking = 0
FEATURE [App::Part] Part134  label="tomacorriente__017"
  Group = -> [InternalObjectName019,Part135,ShapeString074]
  Origin = -> Origin134
  Placement = pos=(17392,5437,0) rot=(0,0,1;1.5708rad)
  expr: Placement.Base.y = Rectangle.Placement.Base.y + Rectangle.Height - 0.6m
  expr: Placement.Base.x = 17m
FEATURE [Part::Part2DObjectPython] ShapeString043  label="rotulo_dibujo_tecnico__043"  # Draft 2D object (typed FeaturePython)
  FontFile = <path>
  Placement = pos=(0,100,0) rot=(0,0,1;0rad)
  Size = 50
  String = 10
  Tracking = 0
FEATURE [App::Part] Part238  label="luz_8in__023"
  Group = -> [InternalObjectName074,Part239,ShapeString043]
  Origin = -> Origin238
  Placement = pos=(18010,3087,0) rot=(0,0,1;0rad)
  expr: Placement.Base.y = Part240.Placement.Base.y - 207cm
  expr: Placement.Base.x = Part236.Placement.Base.x
FEATURE [Part::Part2DObjectPython] ShapeString051  label="rotulo_dibujo_tecnico__051"  # Draft 2D object (typed FeaturePython)
  FontFile = <path>
  Placement = pos=(0,100,0) rot=(0,0,1;0rad)
  Size = 50
  String = 14
  Tracking = 0
FEATURE [App::Part] Part254  label="luz_8in__031"
  Group = -> [InternalObjectName082,Part255,ShapeString051]
  Origin = -> Origin254
  Placement = pos=(21000,4147,0) rot=(0,0,1;0rad)
  expr: Placement.Base.y = Part244.Placement.Base.y
  expr: Placement.Base.x = Part252.Placement.Base.x
FEATURE [Part::Part2DObjectPython] ShapeString038  label="rotulo_dibujo_tecnico__038"  # Draft 2D object (typed FeaturePython)
  FontFile = <path>
  Placement = pos=(0,100,0) rot=(0,0,1;0rad)
  Size = 50
  String = 6
  Tracking = 0
FEATURE [App::Part] Part228  label="luz_8in__018"
  Group = -> [InternalObjectName069,Part229,ShapeString038]
  Origin = -> Origin228
  Placement = pos=(14840,4867,0) rot=(0,0,1;0rad)
  expr: Placement.Base.x = Part226.Placement.Base.x + 116cm
  expr: Placement.Base.y = Part226.Placement.Base.y
FEATURE [Part::Part2DObjectPython] ShapeString058  label="rotulo_dibujo_tecnico__058"  # Draft 2D object (typed FeaturePython)
  FontFile = <path>
  Placement = pos=(-100,100,0) rot=(0,0,1;0rad)
  Size = 50
  String = 18
  Tracking = 0
FEATURE [Part::Part2DObjectPython] ShapeString023  label="rotulo_dibujo_tecnico__023"  # Draft 2D object (typed FeaturePython)
  FontFile = <path>
  Placement = pos=(0,-100,0) rot=(0,0,1;0rad)
  Size = 50
  String = 38
  Tracking = 0
FEATURE [App::Part] Part196  label="luz_60x60__003"
  Group = -> [InternalObjectName053,Part197,ShapeString023]
  Origin = -> Origin196
  Placement = pos=(6570,2050,0) rot=(0,0,1;0rad)
  expr: Placement.Base.y = Rectangle.Placement.Base.y - 30cm + 235cm
  expr: Placement.Base.x = Rectangle006.Placement.Base.x - 30cm - 135cm
FEATURE [Part::Part2DObjectPython] ShapeString008  label="rotulo_dibujo_tecnico__008"  # Draft 2D object (typed FeaturePython)
  FontFile = <path>
  Placement = pos=(0,100,0) rot=(0,0,1;0rad)
  Size = 50
  String = 11
  Tracking = 0
FEATURE [App::Part] Part175  label="interruptor_sencillo__005"
  Group = -> [InternalObjectName040,Part176,ShapeString008]
  Origin = -> Origin176
  Placement = pos=(9980,50,0) rot=(0,0,1;0rad)
  expr: Placement.Base.x = Rectangle006.Placement.Base.x + 1.76m
  expr: Placement.Base.y = Rectangle.Placement.Base.x + 50mm
FEATURE [Part::Part2DObjectPython] ShapeString021  label="rotulo_dibujo_tecnico__021"  # Draft 2D object (typed FeaturePython)
  FontFile = <path>
  Placement = pos=(0,-100,0) rot=(0,0,1;0rad)
  Size = 50
  String = 23
  Tracking = 0
FEATURE [App::Part] Part192  label="luz_60x60__001"
  Group = -> [InternalObjectName051,Part193,ShapeString021]
  Origin = -> Origin192
  Placement = pos=(6570,550,0) rot=(0,0,1;0rad)
  expr: Placement.Base.y = Rectangle.Placement.Base.y - 30cm + 85cm
  expr: Placement.Base.x = Rectangle006.Placement.Base.x - 30cm - 135cm
FEATURE [Part::Part2DObjectPython] ShapeString071  label="rotulo_dibujo_tecnico__071"  # Draft 2D object (typed FeaturePython)
  FontFile = <path>
  Placement = pos=(0,100,0) rot=(0,0,1;0rad)
  Size = 50
  String = 2
  Tracking = 0
FEATURE [Part::Part2DObjectPython] ShapeString013  label="rotulo_dibujo_tecnico__013"  # Draft 2D object (typed FeaturePython)
  FontFile = <path>
  Placement = pos=(250,-100,0) rot=(0,0,1;3.14159rad)
  Size = 50
  String = 8
  Tracking = 0
FEATURE [App::Part] Part183  label="interruptor_sencillo__009"
  Group = -> [InternalObjectName045,Part184,ShapeString013]
  Origin = -> Origin184
  Placement = pos=(22200,4617,0) rot=(0,0,1;3.14159rad)
  expr: Placement.Base.y = Rectangle.Placement.Base.y + Rectangle.Height - 1420mm
  expr: Placement.Base.x = Rectangle.Placement.Base.x + Rectangle.Length - 50mm
FEATURE [Part::Part2DObjectPython] ShapeString039  label="rotulo_dibujo_tecnico__039"  # Draft 2D object (typed FeaturePython)
  FontFile = <path>
  Placement = pos=(0,100,0) rot=(0,0,1;0rad)
  Size = 50
  String = 26
  Tracking = 0
FEATURE [App::Part] Part230  label="luz_8in__019"
  Group = -> [InternalObjectName070,Part231,ShapeString039]
  Origin = -> Origin230
  Placement = pos=(16480,4867,0) rot=(0,0,1;0rad)
  expr: Placement.Base.x = Part228.Placement.Base.x + 164cm
  expr: Placement.Base.y = Part226.Placement.Base.y
FEATURE [Part::Part2DObjectPython] ShapeString041  label="rotulo_dibujo_tecnico__041"  # Draft 2D object (typed FeaturePython)
  FontFile = <path>
  Placement = pos=(0,100,0) rot=(0,0,1;0rad)
  Size = 50
  String = 25
  Tracking = 0
FEATURE [App::Part] Part234  label="luz_8in__021"
  Group = -> [InternalObjectName072,Part235,ShapeString041]
  Origin = -> Origin234
  Placement = pos=(16593,540,0) rot=(0,0,1;0rad)
  expr: Placement.Base.y = Rectangle.Placement.Base.x + 54cm
  expr: Placement.Base.x = Rectangle024.Placement.Base.x - 60cm
FEATURE [Part::Part2DObjectPython] ShapeString009  label="rotulo_dibujo_tecnico__009"  # Draft 2D object (typed FeaturePython)
  FontFile = <path>
  Placement = pos=(0,100,0) rot=(0,0,1;0rad)
  Size = 50
  String = 6
  Tracking = 0
FEATURE [App::Part] Part177  label="interruptor_sencillo__006"
  Group = -> [InternalObjectName041,Part178,ShapeString009]
  Origin = -> Origin178
  Placement = pos=(12840,4920,0) rot=(0,0,1;0rad)
  expr: Placement.Base.y = Rectangle005.Placement.Base.y + 1350mm
  expr: Placement.Base.x = Rectangle005.Placement.Base.x + Rectangle005.Length + 50mm
FEATURE [Part::Part2DObjectPython] ShapeString005  label="rotulo_dibujo_tecnico__005"  # Draft 2D object (typed FeaturePython)
  FontFile = <path>
  Placement = pos=(0,100,0) rot=(0,0,1;0rad)
  Size = 50
  String = 9
  Tracking = 0
FEATURE [App::Part] Part169  label="interruptor_sencillo__002"
  Group = -> [InternalObjectName037,Part170,ShapeString005]
  Origin = -> Origin169
  Placement = pos=(5490,4550,0) rot=(0,0,1;0rad)
  expr: Placement.Base.y = Rectangle016.Placement.Base.y + Rectangle016.Height + 50mm
FEATURE [Part::Part2DObjectPython] ShapeString033  label="rotulo_dibujo_tecnico__033"  # Draft 2D object (typed FeaturePython)
  FontFile = <path>
  Placement = pos=(0,100,0) rot=(0,0,1;0rad)
  Size = 50
  String = 17
  Tracking = 0
FEATURE [App::Part] Part218  label="luz_8in__013"
  Group = -> [InternalObjectName064,Part219,ShapeString033]
  Origin = -> Origin218
  Placement = pos=(8733,2960,0) rot=(0,0,1;0rad)
  expr: Placement.Base.y = Rectangle004.Placement.Base.y - 60cm
  expr: Placement.Base.x = Part208.Placement.Base.x
FEATURE [Part::Part2DObjectPython] ShapeString044  label="rotulo_dibujo_tecnico__044"  # Draft 2D object (typed FeaturePython)
  FontFile = <path>
  Placement = pos=(0,100,0) rot=(0,0,1;0rad)
  Size = 50
  String = 3
  Tracking = 0
FEATURE [App::Part] Part240  label="luz_8in__024"
  Group = -> [InternalObjectName075,Part241,ShapeString044]
  Origin = -> Origin240
  Placement = pos=(18010,5157,0) rot=(0,0,1;0rad)
  expr: Placement.Base.y = Rectangle.Placement.Base.x + Rectangle.Height - 0.88m
  expr: Placement.Base.x = Part236.Placement.Base.x
FEATURE [Part::Part2DObjectPython] ShapeString056  label="rotulo_dibujo_tecnico__056"  # Draft 2D object (typed FeaturePython)
  FontFile = <path>
  Placement = pos=(0,100,0) rot=(0,0,1;0rad)
  Size = 50
  String = 1
  Tracking = 0
FEATURE [App::Part] Part266  label="extractor_aire__001"
  Group = -> [Part267,InternalObjectName089,ShapeString056]
  Origin = -> Origin266
  Placement = pos=(6000,5555,0) rot=(0,0,1;0rad)
  expr: Placement.Base.x = Rectangle015.Placement.Base.x + Rectangle015.Length + 20cm
  expr: Placement.Base.y = Rectangle017.Placement.Base.y - 36cm
FEATURE [Part::Part2DObjectPython] ShapeString022  label="rotulo_dibujo_tecnico__022"  # Draft 2D object (typed FeaturePython)
  FontFile = <path>
  Placement = pos=(0,-100,0) rot=(0,0,1;0rad)
  Size = 50
  String = 39
  Tracking = 0
FEATURE [App::Part] Part194  label="luz_60x60__002"
  Group = -> [InternalObjectName052,Part195,ShapeString022]
  Origin = -> Origin194
  Placement = pos=(3720,2050,0) rot=(0,0,1;0rad)
  expr: Placement.Base.y = Rectangle.Placement.Base.y - 30cm + 235cm
  expr: Placement.Base.x = Rectangle006.Placement.Base.x - 30cm - 420cm
FEATURE [Part::Part2DObjectPython] ShapeString047  label="rotulo_dibujo_tecnico__047"  # Draft 2D object (typed FeaturePython)
  FontFile = <path>
  Placement = pos=(0,100,0) rot=(0,0,1;0rad)
  Size = 50
  String = 8
  Tracking = 0
FEATURE [App::Part] Part246  label="luz_8in__027"
  Group = -> [InternalObjectName078,Part247,ShapeString047]
  Origin = -> Origin246
  Placement = pos=(19730,3087,0) rot=(0,0,1;0rad)
  expr: Placement.Base.x = Part238.Placement.Base.x + 172cm
  expr: Placement.Base.y = Part238.Placement.Base.y
FEATURE [Part::Part2DObjectPython] ShapeString082  label="rotulo_dibujo_tecnico__082"  # Draft 2D object (typed FeaturePython)
  FontFile = <path>
  Placement = pos=(0,100,0) rot=(0,0,1;0rad)
  Size = 50
  String = 24
  Tracking = 0
FEATURE [App::Part] Part151  label="tomacorriente__025"
  Group = -> [InternalObjectName027,Part150,ShapeString082]
  Origin = -> Origin150
  Placement = pos=(20570,50,0) rot=(0,0,1;0rad)
  expr: Placement.Base.y = Rectangle.Placement.Base.y + 0.05m
  expr: Placement.Base.x = Rectangle.Placement.Base.x + Rectangle.Length - 1.68m
FEATURE [Part::Part2DObjectPython] ShapeString081  label="rotulo_dibujo_tecnico__081"  # Draft 2D object (typed FeaturePython)
  FontFile = <path>
  Placement = pos=(0,-150,0) rot=(0,0,1;0rad)
  Size = 50
  String = 23
  Tracking = 0
FEATURE [App::Part] Part148  label="tomacorriente__024"
  Group = -> [InternalObjectName026,Part149,ShapeString081]
  Origin = -> Origin148
  Placement = pos=(20720,50,0) rot=(0,0,1;0rad)
  expr: Placement.Base.y = Rectangle.Placement.Base.y + 0.05m
  expr: Placement.Base.x = Rectangle.Placement.Base.x + Rectangle.Length - 1.53m
FEATURE [Part::Part2DObjectPython] ShapeString060  label="rotulo_dibujo_tecnico__060"  # Draft 2D object (typed FeaturePython)
  FontFile = <path>
  Placement = pos=(100,100,0) rot=(0,0,1;0rad)
  Size = 50
  String = 16
  Tracking = 0
FEATURE [Part::Part2DObjectPython] ShapeString061  label="rotulo_dibujo_tecnico__061"  # Draft 2D object (typed FeaturePython)
  FontFile = <path>
  Placement = pos=(0,150,0) rot=(0,0,1;3.14159rad)
  Size = 50
  String = 13
  Tracking = 0
FEATURE [Part::Part2DObjectPython] ShapeString077  label="rotulo_dibujo_tecnico__077"  # Draft 2D object (typed FeaturePython)
  FontFile = <path>
  Placement = pos=(0,-150,0) rot=(0,0,1;0rad)
  Size = 50
  String = 21
  Tracking = 0
FEATURE [App::Part] Part140  label="tomacorriente__020"
  Group = -> [InternalObjectName022,Part141,ShapeString077]
  Origin = -> Origin140
  Placement = pos=(19263,5867,0) rot=(0,0,1;1.5708rad)
  expr: Placement.Base.y = Rectangle.Placement.Base.y + Rectangle.Height - 0.17m
  expr: Placement.Base.x = Rectangle023.Placement.Base.x + Rectangle023.Length + 50mm
FEATURE [Part::Part2DObjectPython] ShapeString063  label="rotulo_dibujo_tecnico__063"  # Draft 2D object (typed FeaturePython)
  FontFile = <path>
  Placement = pos=(0,100,0) rot=(0,0,1;0rad)
  Size = 50
  String = 11
  Tracking = 0
FEATURE [Part::Part2DObjectPython] ShapeString059  label="rotulo_dibujo_tecnico__059"  # Draft 2D object (typed FeaturePython)
  FontFile = <path>
  Placement = pos=(0,100,0) rot=(0,0,1;0rad)
  Size = 50
  String = 14
  Tracking = 0
FEATURE [Part::Part2DObjectPython] ShapeString080  label="rotulo_dibujo_tecnico__080"  # Draft 2D object (typed FeaturePython)
  FontFile = <path>
  Placement = pos=(0,100,0) rot=(0,0,1;0rad)
  Size = 50
  String = 29
  Tracking = 0
FEATURE [App::Part] Part146  label="tomacorriente__023"
  Group = -> [InternalObjectName025,Part147,ShapeString080]
  Origin = -> Origin146
  Placement = pos=(22200,4327,0) rot=(0,0,1;1.5708rad)
  expr: Placement.Base.y = Rectangle.Placement.Base.y + Rectangle.Height - 1.71m
  expr: Placement.Base.x = Rectangle.Placement.Base.x + Rectangle.Length - 0.05m
FEATURE [Part::Part2DObjectPython] ShapeString086  label="rotulo_dibujo_tecnico__086"  # Draft 2D object (typed FeaturePython)
  FontFile = <path>
  Placement = pos=(-100,100,0) rot=(0,0,1;0rad)
  Size = 50
  String = 20
  Tracking = 0
FEATURE [Part::Part2DObjectPython] Line016  # Draft 2D object (typed FeaturePython)
  ChamferSize = 0
  Closed = false
  End = (-48.8237,-10,0)
  FilletRadius = 0
  Length = 128.824
  MakeFace = false
  Placement = pos=(80,-10,0) rot=(0,0,1;0rad)
  Points = (2) [(0,-5.32907e-15,0),(-128.824,-3.55271e-15,0)]
  Start = (80,-10,0)
  Subdivisions = 0
FEATURE [App::Part] Part117  label="contenido017"
  Group = -> [Circle008,Line017,Line016]
  Origin = -> Origin116
FEATURE [App::Part] Part116  label="tomacorriente__008"
  Group = -> [InternalObjectName010,Part117,ShapeString065]
  Origin = -> Origin117
  Placement = pos=(8167,1300,0) rot=(0,0,1;1.5708rad)
  expr: Placement.Base.y = Rectangle.Placement.Base.y + 1.3m
FEATURE [Part::Part2DObjectPython] Line028  # Draft 2D object (typed FeaturePython)
  ChamferSize = 0
  Closed = false
  End = (-48.9007,10,0)
  FilletRadius = 0
  Length = 128.901
  MakeFace = false
  Placement = pos=(80,10,0) rot=(0,0,1;0rad)
  Points = (2) [(0,0,0),(-128.901,-3.55271e-15,0)]
  Start = (80,10,0)
  Subdivisions = 0
FEATURE [App::Part] Part128  label="contenido023"
  Group = -> [Circle014,Line028,Line029]
  Origin = -> Origin128
FEATURE [App::Part] Part129  label="tomacorriente__014"
  Group = -> [InternalObjectName016,Part128,ShapeString071]
  Origin = -> Origin129
  Placement = pos=(17169,3727,0) rot=(0,0,1;1.5708rad)
  expr: Placement.Base.y = Rectangle.Placement.Base.y + Rectangle.Height - 2.31m
  expr: Placement.Base.x = 17m
FEATURE [Part::Part2DObjectPython] Line020  # Draft 2D object (typed FeaturePython)
  ChamferSize = 0
  Closed = false
  End = (-48.8237,-10,0)
  FilletRadius = 0
  Length = 128.824
  MakeFace = false
  Placement = pos=(80,-10,0) rot=(0,0,1;0rad)
  Points = (2) [(0,-5.32907e-15,0),(-128.824,-3.55271e-15,0)]
  Start = (80,-10,0)
  Subdivisions = 0
FEATURE [Part::Part2DObjectPython] ShapeString055  label="rotulo_dibujo_tecnico__055"  # Draft 2D object (typed FeaturePython)
  FontFile = <path>
  Placement = pos=(0,100,0) rot=(0,0,1;0rad)
  Size = 50
  String = 2
  Tracking = 0
FEATURE [App::Part] Part264  label="extractor_aire__"
  Group = -> [Part265,InternalObjectName088,ShapeString055]
  Origin = -> Origin264
  Placement = pos=(5390,5545,0) rot=(0,0,1;0rad)
  expr: Placement.Base.y = Rectangle017.Placement.Base.y - 37cm
  expr: Placement.Base.x = Rectangle015.Placement.Base.x - 24cm
FEATURE [App::DocumentObjectGroup] Group018  label="piso1_extras"
  Group = -> [Part264,Part266,Part268]
FEATURE [Part::Part2DObjectPython] ShapeString031  label="rotulo_dibujo_tecnico__031"  # Draft 2D object (typed FeaturePython)
  FontFile = <path>
  Placement = pos=(0,100,0) rot=(0,0,1;0rad)
  Size = 50
  String = 24
  Tracking = 0
FEATURE [App::Part] Part214  label="luz_8in__011"
  Group = -> [InternalObjectName062,Part215,ShapeString031]
  Origin = -> Origin214
  Placement = pos=(13093,810,0) rot=(0,0,1;0rad)
  expr: Placement.Base.x = Part212.Placement.Base.x + 159cm
  expr: Placement.Base.y = Rectangle.Placement.Base.y + 81cm
FEATURE [Part::Part2DObjectPython] ShapeString066  label="rotulo_dibujo_tecnico__066"  # Draft 2D object (typed FeaturePython)
  FontFile = <path>
  Placement = pos=(0,-150,0) rot=(0,0,1;0rad)
  Size = 50
  String = 19
  Tracking = 0
FEATURE [App::Part] Part119  label="tomacorriente__009"
  Group = -> [InternalObjectName011,Part118,ShapeString066]
  Origin = -> Origin119
  Placement = pos=(8404,1040,0) rot=(0,0,1;1.5708rad)
  expr: Placement.Base.y = Rectangle006.Placement.Base.y + 1.04m
FEATURE [Part::Part2DObjectPython] ShapeString017  label="rotulo_dibujo_tecnico__017"  # Draft 2D object (typed FeaturePython)
  FontFile = <path>
  Placement = pos=(0,100,0) rot=(0,0,1;0rad)
  Size = 50
  String = 19
  Tracking = 0
FEATURE [App::Part] Part188  label="luz_8in__002"
  Group = -> [InternalObjectName048,Part187,ShapeString017]
  Origin = -> Origin187
  Placement = pos=(2330,3260,0) rot=(0,0,1;0.785398rad)
  expr: Placement.Base.x = Rectangle.Placement.Base.x + 233cm
  expr: Placement.Base.y = Rectangle002.Placement.Base.y + Rectangle002.Height + 161cm
FEATURE [App::Part] Part121  label="contenido019"
  Group = -> [Circle010,Line021,Line020]
  Origin = -> Origin120
FEATURE [App::Part] Part120  label="tomacorriente__010"
  Group = -> [InternalObjectName012,Part121,ShapeString067]
  Origin = -> Origin121
  Placement = pos=(9420,54,0) rot=(0,0,1;0rad)
  expr: Placement.Base.x = Rectangle006.Placement.Base.x + 1.2m
FEATURE [Part::Part2DObjectPython] ShapeString083  label="rotulo_dibujo_tecnico__083"  # Draft 2D object (typed FeaturePython)
  FontFile = <path>
  Placement = pos=(0,-150,0) rot=(0,0,1;0rad)
  Size = 50
  String = 26
  Tracking = 0
FEATURE [App::Part] Part152  label="tomacorriente__026"
  Group = -> [InternalObjectName028,Part153,ShapeString083]
  Origin = -> Origin153
  Placement = pos=(19103,50,0) rot=(0,0,1;0rad)
  expr: Placement.Base.y = Rectangle.Placement.Base.y + 0.05m
  expr: Placement.Base.x = Rectangle010.Placement.Base.x + Rectangle010.Length + 1.8m
FEATURE [Part::Part2DObjectPython] ShapeString084  label="rotulo_dibujo_tecnico__084"  # Draft 2D object (typed FeaturePython)
  FontFile = <path>
  Placement = pos=(0,100,0) rot=(0,0,1;0rad)
  Size = 50
  String = 25
  Tracking = 0
FEATURE [App::Part] Part155  label="tomacorriente__027"
  Group = -> [InternalObjectName029,Part154,ShapeString084]
  Origin = -> Origin154
  Placement = pos=(18963,50,0) rot=(0,0,1;0rad)
  expr: Placement.Base.y = Rectangle.Placement.Base.y + 0.05m
  expr: Placement.Base.x = Rectangle010.Placement.Base.x + Rectangle010.Length + 1.66m
FEATURE [Part::Part2DObjectPython] ShapeString006  label="rotulo_dibujo_tecnico__006"  # Draft 2D object (typed FeaturePython)
  FontFile = <path>
  Placement = pos=(0,100,0) rot=(0,0,1;0rad)
  Size = 50
  String = 2
  Tracking = 0
FEATURE [App::Part] Part171  label="interruptor_sencillo__003"
  Group = -> [InternalObjectName038,Part172,ShapeString006]
  Origin = -> Origin171
  Placement = pos=(5950,4550,0) rot=(0,0,1;0rad)
  expr: Placement.Base.x = Rectangle015.Placement.Base.x + Rectangle015.Length + 0.15m
  expr: Placement.Base.y = Rectangle016.Placement.Base.y + Rectangle016.Height + 50mm
FEATURE [Part::Part2DObjectPython] ShapeString069  label="rotulo_dibujo_tecnico__069"  # Draft 2D object (typed FeaturePython)
  FontFile = <path>
  Placement = pos=(0,100,0) rot=(0,0,1;0rad)
  Size = 50
  String = 3
  Tracking = 0
FEATURE [App::Part] Part124  label="tomacorriente__012"
  Group = -> [InternalObjectName014,Part125,ShapeString069]
  Origin = -> Origin124
  Placement = pos=(13050,54,0) rot=(0,0,1;0rad)
  expr: Placement.Base.x = Part123.Placement.Base.x + 1.59m
FEATURE [Part::Part2DObjectPython] ShapeString010  label="rotulo_dibujo_tecnico__010"  # Draft 2D object (typed FeaturePython)
  FontFile = <path>
  Placement = pos=(250,-100,0) rot=(0,0,1;3.14159rad)
  Size = 50
  String = 7
  Tracking = 0
FEATURE [App::Part] Part179  label="interruptor_sencillo__007"
  Group = -> [InternalObjectName042,Part180,ShapeString010]
  Origin = -> Origin180
  Placement = pos=(15823,650,0) rot=(0,0,1;3.14159rad)
  expr: Placement.Base.y = Rectangle008.Placement.Base.y + 650mm
  expr: Placement.Base.x = Rectangle008.Placement.Base.x - 50mm
FEATURE [Part::Part2DObjectPython] ShapeString011  label="rotulo_dibujo_tecnico__011"  # Draft 2D object (typed FeaturePython)
  FontFile = <path>
  Placement = pos=(250,-100,0) rot=(0,0,1;3.14159rad)
  Size = 50
  String = 4
  Tracking = 0
FEATURE [App::Part] Part181  label="interruptor_sencillo__008"
  Group = -> [InternalObjectName043,Part182,ShapeString011]
  Origin = -> Origin182
  Placement = pos=(17143,865,0) rot=(0,0,1;3.14159rad)
  expr: Placement.Base.y = Rectangle024.Placement.Base.y + 865mm
  expr: Placement.Base.x = Rectangle024.Placement.Base.x - 50mm
FEATURE [App::DocumentObjectGroup] Group006  label="piso1_int"
  Group = -> [Part166,Part018,Part167,Part169,Part171,Part173,Part175,Part177,Part179,Part181,Part090,Part183,Part262]
FEATURE [Part::Part2DObjectPython] ShapeString087  label="rotulo_dibujo_tecnico__087"  # Draft 2D object (typed FeaturePython)
  FontFile = <path>
  Placement = pos=(0,100,0) rot=(0,0,1;0rad)
  Size = 50
  String = 31
  Tracking = 0
FEATURE [Part::Part2DObjectPython] ShapeString073  label="rotulo_dibujo_tecnico__073"  # Draft 2D object (typed FeaturePython)
  FontFile = <path>
  Placement = pos=(0,-150,0) rot=(0,0,1;0rad)
  Size = 50
  String = 7
  Tracking = 0
FEATURE [App::Part] Part132  label="tomacorriente__016"
  Group = -> [InternalObjectName018,Part133,ShapeString073]
  Origin = -> Origin132
  Placement = pos=(17392,5307,0) rot=(0,0,1;1.5708rad)
  expr: Placement.Base.y = Rectangle.Placement.Base.y + Rectangle.Height - 0.73m
  expr: Placement.Base.x = 17m
FEATURE [Part::Part2DObjectPython] ShapeString054  label="rotulo_dibujo_tecnico__054"  # Draft 2D object (typed FeaturePython)
  FontFile = <path>
  Placement = pos=(0,100,0) rot=(0,0,1;0rad)
  Size = 50
  String = 13
  Tracking = 0
FEATURE [App::Part] Part260  label="luz_8in__034"
  Group = -> [InternalObjectName085,Part261,ShapeString054]
  Origin = -> Origin260
  Placement = pos=(21000,1020,0) rot=(0,0,1;0rad)
  expr: Placement.Base.y = Part250.Placement.Base.y
  expr: Placement.Base.x = Part252.Placement.Base.x
FEATURE [App::DocumentObjectGroup] Group017  label="piso1_luz"
  Group = -> [Part021,Part186,Part188,Part190,Part199,Part089,Part192,Part194,Part196,Part201,Part202,Part204,Part206,Part208,Part210,Part212,Part214,Part216,Part218,Part220,Part222,Part224,Part226,Part228,Part230,Part232,Part234,Part236,Part238,Part240,Part242,Part244,Part246,Part248,Part250,Part252,Part254,Part256,Part258,Part260]
FEATURE [Part::Part2DObjectPython] ShapeString089  label="rotulo_dibujo_tecnico__089"  # Draft 2D object (typed FeaturePython)
  FontFile = <path>
  Placement = pos=(0,100,0) rot=(0,0,1;0rad)
  Size = 50
  String = 30
  Tracking = 0
FEATURE [App::Part] Part165  label="tomacorriente__032"
  Group = -> [InternalObjectName034,Part164,ShapeString089]
  Origin = -> Origin164
  Placement = pos=(21070,50,0) rot=(0,0,1;0rad)
  expr: Placement.Base.y = Rectangle.Placement.Base.y + 0.05m
  expr: Placement.Base.x = Rectangle.Placement.Base.x + Rectangle.Length - 1.18m
FEATURE [Part::Part2DObjectPython] Circle004  # Draft 2D object (typed FeaturePython)
  FirstAngle = 0
  LastAngle = 0
  MakeFace = false
  Radius = 50
FEATURE [Part::Part2DObjectPython] Line002  # Draft 2D object (typed FeaturePython)
  ChamferSize = 0
  Closed = false
  End = (-48.9007,10,0)
  FilletRadius = 0
  Length = 128.901
  MakeFace = false
  Placement = pos=(80,10,0) rot=(0,0,1;0rad)
  Points = (2) [(0,0,0),(-128.901,-3.55271e-15,0)]
  Start = (80,10,0)
  Subdivisions = 0
FEATURE [Part::Part2DObjectPython] Line056  # Draft 2D object (typed FeaturePython)
  ChamferSize = 0
  Closed = false
  End = (-48.9007,10,0)
  FilletRadius = 0
  Length = 128.901
  MakeFace = false
  Placement = pos=(80,10,0) rot=(0,0,1;0rad)
  Points = (2) [(0,0,0),(-128.901,-3.55271e-15,0)]
  Start = (80,10,0)
  Subdivisions = 0
FEATURE [Part::Part2DObjectPython] Rectangle012  # Draft 2D object (typed FeaturePython)
  ChamferSize = 0
  Columns = 1
  FilletRadius = 0
  Height = 585
  Length = 100
  MakeFace = true
  Placement = pos=(3200,5400,0) rot=(0,0,1;0rad)
  Rows = 1
FEATURE [Part::Part2DObjectPython] Line060  # Draft 2D object (typed FeaturePython)
  ChamferSize = 0
  Closed = false
  End = (-48.9007,10,0)
  FilletRadius = 0
  Length = 128.901
  MakeFace = false
  Placement = pos=(80,10,0) rot=(0,0,1;0rad)
  Points = (2) [(0,0,0),(-128.901,-3.55271e-15,0)]
  Start = (80,10,0)
  Subdivisions = 0
FEATURE [Part::Part2DObjectPython] Line063  # Draft 2D object (typed FeaturePython)
  ChamferSize = 0
  Closed = false
  End = (-48.9007,10,0)
  FilletRadius = 0
  Length = 128.901
  MakeFace = false
  Placement = pos=(80,10,0) rot=(0,0,1;0rad)
  Points = (2) [(0,0,0),(-128.901,-3.55271e-15,0)]
  Start = (80,10,0)
  Subdivisions = 0
FEATURE [App::Part] Part162  label="contenido040"
  Group = -> [Circle031,Line063,Line062]
  Origin = -> Origin162
FEATURE [Part::Part2DObjectPython] Line008  # Draft 2D object (typed FeaturePython)
  ChamferSize = 0
  Closed = false
  End = (-48.9007,10,0)
  FilletRadius = 0
  Length = 128.901
  MakeFace = false
  Placement = pos=(80,10,0) rot=(0,0,1;0rad)
  Points = (2) [(0,0,0),(-128.901,-3.55271e-15,0)]
  Start = (80,10,0)
  Subdivisions = 0
FEATURE [Part::Part2DObjectPython] Line010  # Draft 2D object (typed FeaturePython)
  ChamferSize = 0
  Closed = false
  End = (-48.8237,-10,0)
  FilletRadius = 0
  Length = 128.824
  MakeFace = false
  Placement = pos=(80,-10,0) rot=(0,0,1;0rad)
  Points = (2) [(0,-5.32907e-15,0),(-128.824,-3.55271e-15,0)]
  Start = (80,-10,0)
  Subdivisions = 0
FEATURE [Part::Part2DObjectPython] Circle001  # Draft 2D object (typed FeaturePython)
  FirstAngle = 0
  LastAngle = 0
  MakeFace = false
  Radius = 50
FEATURE [Part::Part2DObjectPython] Rectangle016  # Draft 2D object (typed FeaturePython)
  ChamferSize = 0
  Columns = 1
  FilletRadius = 0
  Height = 170
  Length = 850
  MakeFace = true
  Placement = pos=(5300,4330,0) rot=(0,0,1;0rad)
  Rows = 1
  expr: Placement.Base.y = Rectangle003.Placement.Base.y
  expr: Placement.Base.x = Dimension036.End.x
FEATURE [Part::Part2DObjectPython] Rectangle017  # Draft 2D object (typed FeaturePython)
  ChamferSize = 0
  Columns = 1
  FilletRadius = 0
  Height = 70
  Length = 7080
  MakeFace = true
  Placement = pos=(4370,5915,0) rot=(0,0,1;0rad)
  Rows = 1
  Support = -> [Rectangle016]
  expr: Length = Rectangle003.Placement.Base.x + Rectangle003.Length
  expr: Placement.Base.x = Rectangle013.Placement.Base.x + Rectangle013.Length
  expr: Placement.Base.y = Rectangle003.Placement.Base.y + Rectangle003.Height - Rectangle017.Height
FEATURE [App::Part] Part111  label="contenido014"
  Group = -> [Circle005,Line011,Line010]
  Origin = -> Origin110
FEATURE [Part::Part2DObjectPython] Circle006  # Draft 2D object (typed FeaturePython)
  FirstAngle = 0
  LastAngle = 0
  MakeFace = false
  Radius = 50
FEATURE [Part::Part2DObjectPython] ShapeString088  label="rotulo_dibujo_tecnico__088"  # Draft 2D object (typed FeaturePython)
  FontFile = <path>
  Placement = pos=(0,-150,0) rot=(0,0,1;0rad)
  Size = 50
  String = 32
  Tracking = 0
FEATURE [App::Part] Part163  label="tomacorriente__031"
  Group = -> [InternalObjectName033,Part162,ShapeString088]
  Origin = -> Origin163
  Placement = pos=(16183,1070,0) rot=(0,0,1;0rad)
  expr: Placement.Base.y = Rectangle025.Placement.Base.y - 0.05m
  expr: Placement.Base.x = Rectangle008.Placement.Base.x + Rectangle008.Length + 0.18m
FEATURE [App::Part] Part102  label="contenido010"
  Group = -> [Circle001,Line002,Line003]
  Origin = -> Origin103
FEATURE [App::Part] Part103  label="tomacorriente__001"
  Group = -> [InternalObjectName003,Part102,ShapeString059]
  Origin = -> Origin102
  Placement = pos=(1810,1700,0) rot=(0,0,1;0rad)
  expr: Placement.Base.x = Part101.Placement.Base.x + 0.15m
FEATURE [Part::Part2DObjectPython] Line007  # Draft 2D object (typed FeaturePython)
  ChamferSize = 0
  Closed = false
  End = (-48.9007,10,0)
  FilletRadius = 0
  Length = 128.901
  MakeFace = false
  Placement = pos=(80,10,0) rot=(0,0,1;0rad)
  Points = (2) [(0,0,0),(-128.901,-3.55271e-15,0)]
  Start = (80,10,0)
  Subdivisions = 0
FEATURE [App::Part] Part107  label="contenido012"
  Group = -> [Circle003,Line007,Line006]
  Origin = -> Origin106
FEATURE [App::Part] Part106  label="tomacorriente__003"
  Group = -> [InternalObjectName005,Part107,ShapeString060]
  Origin = -> Origin107
  Placement = pos=(1960,1700,0) rot=(0,0,1;0rad)
  expr: Placement.Base.x = Part101.Placement.Base.x + 0.3m
FEATURE [App::Part] Part100  label="contenido009"
  Group = -> [Wire002,Wire001]
  Origin = -> Origin100
FEATURE [App::Part] Part004  label="tablero_distribucion__"
  Group = -> [Part100,InternalObjectName002,Part104,Part270,Part271,Part272,Part273,Part274,Part275,Part276,Part277,Part278,Part279,Part280,Part281,Part282,Part283,Part284,Part285,Part286,Part287,Part288,Part289,Part290,Part105,Part291,Part292,Part293,Part294,ShapeString001]
  Origin = -> Origin004
  Placement = pos=(2395,611,0) rot=(0,0,1;4.71239rad)
FEATURE [App::Part] Part110  label="tomacorriente__005"
  Group = -> [InternalObjectName007,Part111,ShapeString062]
  Origin = -> Origin111
  Placement = pos=(7540,54,0) rot=(0,0,1;0rad)
  expr: Placement.Base.x = Rectangle006.Placement.Base.x - 0.68m
FEATURE [Part::Part2DObjectPython] Line012  # Draft 2D object (typed FeaturePython)
  ChamferSize = 0
  Closed = false
  End = (-48.8237,-10,0)
  FilletRadius = 0
  Length = 128.824
  MakeFace = false
  Placement = pos=(80,-10,0) rot=(0,0,1;0rad)
  Points = (2) [(0,-5.32907e-15,0),(-128.824,-3.55271e-15,0)]
  Start = (80,-10,0)
  Subdivisions = 0
FEATURE [App::Part] Part113  label="contenido015"
  Group = -> [Circle006,Line013,Line012]
  Origin = -> Origin112
FEATURE [App::Part] Part112  label="tomacorriente__006"
  Group = -> [InternalObjectName008,Part113,ShapeString063]
  Origin = -> Origin113
  Placement = pos=(4840,54,0) rot=(0,0,1;0rad)
  expr: Placement.Base.x = Rectangle002.Placement.Base.x + Rectangle002.Length + 2.44m
FEATURE [Part::Part2DObjectPython] Rectangle014  # Draft 2D object (typed FeaturePython)
  ChamferSize = 0
  Columns = 1
  FilletRadius = 0
  Height = 100
  Length = 1040
  MakeFace = true
  Placement = pos=(3200,4925,0) rot=(0,0,1;0rad)
  Rows = 1
  expr: Placement.Base.y = Rectangle003.Placement.Base.y + Rectangle003.Height - Rectangle014.Height - 0.96m
  expr: Length = Rectangle013.Placement.Base.x - Rectangle003.Placement.Base.x
FEATURE [App::DocumentObjectGroup] Group003  label="piso1_arq_div"
  Group = -> [Rectangle012,Rectangle013,Rectangle014,Group004,Rectangle015,Rectangle016,Rectangle017,Rectangle019,Rectangle020,Rectangle021,Rectangle022,Rectangle023,Rectangle024,Rectangle025]
FEATURE [Part::Part2DObjectPython] Line009  # Draft 2D object (typed FeaturePython)
  ChamferSize = 0
  Closed = false
  End = (-48.8237,-10,0)
  FilletRadius = 0
  Length = 128.824
  MakeFace = false
  Placement = pos=(80,-10,0) rot=(0,0,1;0rad)
  Points = (2) [(0,-5.32907e-15,0),(-128.824,-3.55271e-15,0)]
  Start = (80,-10,0)
  Subdivisions = 0
FEATURE [App::Part] Part108  label="contenido013"
  Group = -> [Circle004,Line008,Line009]
  Origin = -> Origin109
FEATURE [App::Part] Part109  label="tomacorriente__004"
  Group = -> [InternalObjectName006,Part108,ShapeString061]
  Origin = -> Origin108
  Placement = pos=(5720,4275,0) rot=(0,0,1;3.14159rad)
  expr: Placement.Base.x = Rectangle004.Placement.Base.x - 1.36m
FEATURE [Part::Part2DObjectPython] Line  # Draft 2D object (typed FeaturePython)
  ChamferSize = 0
  Closed = false
  End = (-48.9007,10,0)
  FilletRadius = 0
  Length = 128.901
  MakeFace = false
  Placement = pos=(80,10,0) rot=(0,0,1;0rad)
  Points = (2) [(0,0,0),(-128.901,-3.55271e-15,0)]
  Start = (80,10,0)
  Subdivisions = 0
FEATURE [Part::Part2DObjectPython] Line001  # Draft 2D object (typed FeaturePython)
  ChamferSize = 0
  Closed = false
  End = (-48.8237,-10,0)
  FilletRadius = 0
  Length = 128.824
  MakeFace = false
  Placement = pos=(80,-10,0) rot=(0,0,1;0rad)
  Points = (2) [(0,-5.32907e-15,0),(-128.824,-3.55271e-15,0)]
  Start = (80,-10,0)
  Subdivisions = 0
FEATURE [App::Part] Part099  label="contenido008"
  Group = -> [Circle,Line,Line001]
  Origin = -> Origin099
FEATURE [App::Part] Part101  label="tomacorriente__"
  Group = -> [InternalObjectName,Part099,ShapeString058]
  Origin = -> Origin101
  Placement = pos=(1660,1700,0) rot=(0,0,1;0rad)
  expr: Placement.Base.x = Rectangle.Placement.Base.x + 1.66m
FEATURE [App::Part] Part159  label="contenido038"
  Group = -> [Circle029,Line058,Line059]
  Origin = -> Origin158
FEATURE [App::Part] Part158  label="tomacorriente__029"
  Group = -> [InternalObjectName031,Part159,ShapeString086]
  Origin = -> Origin159
  Placement = pos=(17353,840,0) rot=(0,0,1;4.71239rad)
  expr: Placement.Base.y = Rectangle.Placement.Base.y + 0.84m
  expr: Placement.Base.x = Rectangle010.Placement.Base.x + Rectangle010.Length + 0.05m
FEATURE [Part::Part2DObjectPython] Line057  # Draft 2D object (typed FeaturePython)
  ChamferSize = 0
  Closed = false
  End = (-48.8237,-10,0)
  FilletRadius = 0
  Length = 128.824
  MakeFace = false
  Placement = pos=(80,-10,0) rot=(0,0,1;0rad)
  Points = (2) [(0,-5.32907e-15,0),(-128.824,-3.55271e-15,0)]
  Start = (80,-10,0)
  Subdivisions = 0
FEATURE [App::Part] Part157  label="contenido037"
  Group = -> [Circle028,Line056,Line057]
  Origin = -> Origin156
FEATURE [App::Part] Part156  label="tomacorriente__028"
  Group = -> [InternalObjectName030,Part157,ShapeString085]
  Origin = -> Origin157
  Placement = pos=(17353,680,0) rot=(0,0,1;4.71239rad)
  expr: Placement.Base.y = Rectangle.Placement.Base.y + 0.68m
  expr: Placement.Base.x = Rectangle010.Placement.Base.x + Rectangle010.Length + 0.05m
FEATURE [Part::Part2DObjectPython] Circle030  # Draft 2D object (typed FeaturePython)
  FirstAngle = 0
  LastAngle = 0
  MakeFace = false
  Radius = 50
FEATURE [App::Part] Part161  label="contenido039"
  Group = -> [Circle030,Line060,Line061]
  Origin = -> Origin160
FEATURE [App::Part] Part160  label="tomacorriente__030"
  Group = -> [InternalObjectName032,Part161,ShapeString087]
  Origin = -> Origin161
  Placement = pos=(17468,50,0) rot=(0,0,1;0rad)
  expr: Placement.Base.y = Rectangle.Placement.Base.y + 0.05m
  expr: Placement.Base.x = Rectangle010.Placement.Base.x + Rectangle010.Length + 0.165m
FEATURE [App::DocumentObjectGroup] Group005  label="piso1_tc"
  Group = -> [Part101,Part103,Part106,Part109,Part110,Part112,Part114,Part116,Part119,Part120,Part123,Part124,Part126,Part129,Part131,Part132,Part134,Part136,Part138,Part140,Part142,Part144,Part146,Part148,Part151,Part152,Part155,Part156,Part158,Part160,Part163,Part165]
FEATURE [App::DocumentObjectGroup] Group002  label="piso1_electronicos"
  Group = -> [Part004,Group005]
FEATURE [App::Part] Part  label="_piso1"
  Group = -> [Rectangle002,Rectangle003,Rectangle004,Rectangle005,Dimension005,Dimension006,Dimension009,Dimension010,Dimension011,Rectangle006,Dimension012,Dimension013,Dimension014,Dimension015,Dimension016,Dimension017,Dimension018,Rectangle007,Dimension019,Rectangle008,Dimension020,Dimension021,Rectangle010,Dimension022,Dimension023,Dimension026,Dimension027,Dimension028,Group,Dimension029,Rectangle011,+67 more]
  Origin = -> Origin
note: 89 file-system paths scrubbed to <path> (originals preserved in the JSON sidecar)
